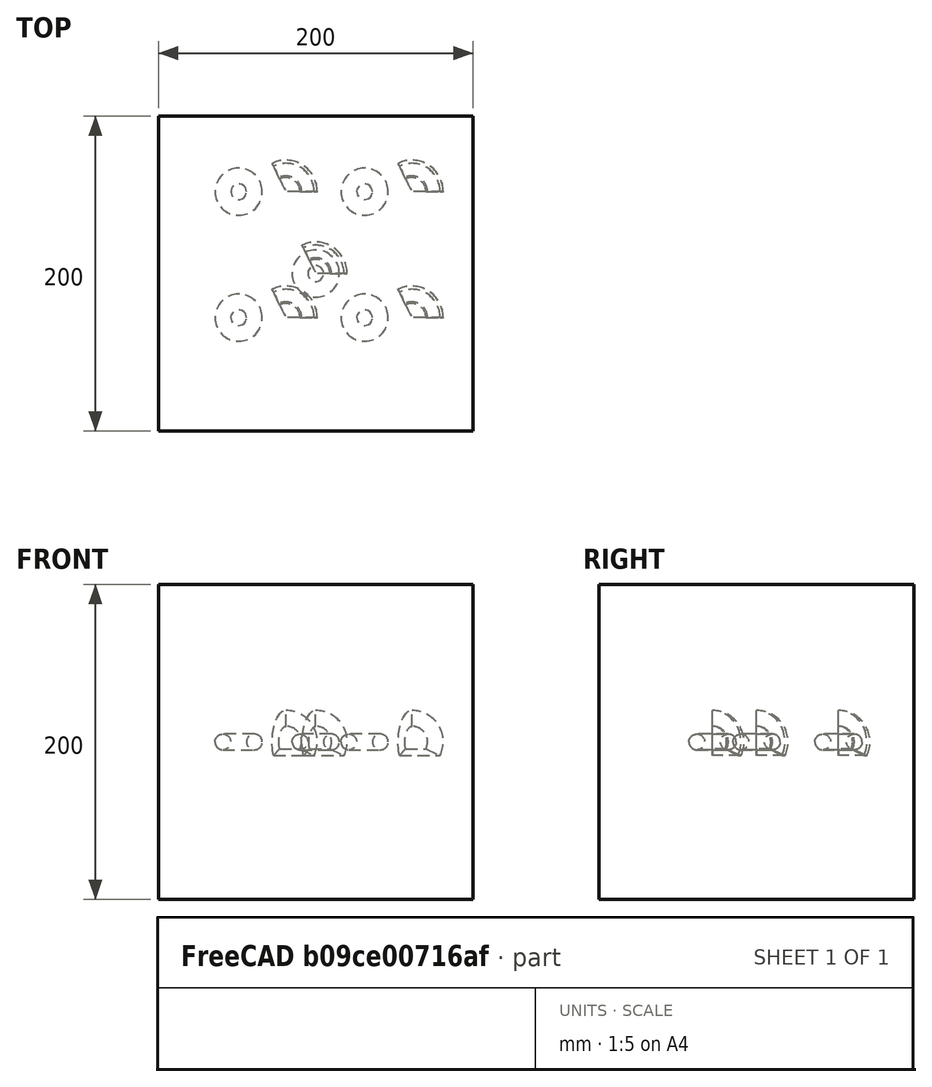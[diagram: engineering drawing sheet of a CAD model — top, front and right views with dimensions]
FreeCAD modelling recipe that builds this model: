
FCSTD DOCUMENT  (FreeCAD 1.0R39109 (Git))
Label: arrayTest-5
License: All rights reserved
LicenseURL: http://en.wikipedia.org/wiki/All_rights_reserved
objects: App::DocumentObjectGroupPython×1248, App::Part×5, Part::FeaturePython×4
note: 4 computed .brp shape members not serialized (recipe doc carries the construction recipe); baked Part::Feature solids carry a one-line shape summary decoded from their .brp

FEATURE [App::DocumentObjectGroupPython] HALFPI  # scripted group (container) (typed FeaturePython)
  name = HALFPI
  value = pi/2.
FEATURE [App::DocumentObjectGroupPython] PI  # scripted group (container) (typed FeaturePython)
  name = PI
  value = 1.*pi
FEATURE [App::DocumentObjectGroupPython] TWOPI  # scripted group (container) (typed FeaturePython)
  name = TWOPI
  value = 2.*pi
FEATURE [App::DocumentObjectGroupPython] Constants  # scripted group (container) (typed FeaturePython)
  Group = -> [HALFPI,PI,TWOPI]
FEATURE [App::DocumentObjectGroupPython] Variables  # scripted group (container) (typed FeaturePython)
FEATURE [App::DocumentObjectGroupPython] Quantities  # scripted group (container) (typed FeaturePython)
FEATURE [App::DocumentObjectGroupPython] Isotopes  # scripted group (container) (typed FeaturePython)
FEATURE [App::DocumentObjectGroupPython] Elements  # scripted group (container) (typed FeaturePython)
FEATURE [App::DocumentObjectGroupPython] G4Isotopes  # scripted group (container) (typed FeaturePython)
FEATURE [App::DocumentObjectGroupPython] H_element  # scripted group (container) (typed FeaturePython)
  Z = 1
  atom_value = 1.008
  formula = H
  name = H_element
FEATURE [App::DocumentObjectGroupPython] He_element  # scripted group (container) (typed FeaturePython)
  Z = 2
  atom_value = 4.0026
  formula = He
  name = He_element
FEATURE [App::DocumentObjectGroupPython] Li_element  # scripted group (container) (typed FeaturePython)
  Z = 3
  atom_value = 6.94
  formula = Li
  name = Li_element
FEATURE [App::DocumentObjectGroupPython] Be_element  # scripted group (container) (typed FeaturePython)
  Z = 4
  atom_value = 9.01218
  formula = Be
  name = Be_element
FEATURE [App::DocumentObjectGroupPython] B_element  # scripted group (container) (typed FeaturePython)
  Z = 5
  atom_value = 10.81
  formula = B
  name = B_element
FEATURE [App::DocumentObjectGroupPython] C_element  # scripted group (container) (typed FeaturePython)
  Z = 6
  atom_value = 12.011
  formula = C
  name = C_element
FEATURE [App::DocumentObjectGroupPython] N_element  # scripted group (container) (typed FeaturePython)
  Z = 7
  atom_value = 14.007
  formula = N
  name = N_element
FEATURE [App::DocumentObjectGroupPython] O_element  # scripted group (container) (typed FeaturePython)
  Z = 8
  atom_value = 15.999
  formula = O
  name = O_element
FEATURE [App::DocumentObjectGroupPython] F_element  # scripted group (container) (typed FeaturePython)
  Z = 9
  atom_value = 18.9984
  formula = F
  name = F_element
FEATURE [App::DocumentObjectGroupPython] Ne_element  # scripted group (container) (typed FeaturePython)
  Z = 10
  atom_value = 20.1797
  formula = Ne
  name = Ne_element
FEATURE [App::DocumentObjectGroupPython] Na_element  # scripted group (container) (typed FeaturePython)
  Z = 11
  atom_value = 22.9898
  formula = Na
  name = Na_element
FEATURE [App::DocumentObjectGroupPython] Mg_element  # scripted group (container) (typed FeaturePython)
  Z = 12
  atom_value = 24.305
  formula = Mg
  name = Mg_element
FEATURE [App::DocumentObjectGroupPython] Al_element  # scripted group (container) (typed FeaturePython)
  Z = 13
  atom_value = 26.9815
  formula = Al
  name = Al_element
FEATURE [App::DocumentObjectGroupPython] Si_element  # scripted group (container) (typed FeaturePython)
  Z = 14
  atom_value = 28.085
  formula = Si
  name = Si_element
FEATURE [App::DocumentObjectGroupPython] P_element  # scripted group (container) (typed FeaturePython)
  Z = 15
  atom_value = 30.9738
  formula = P
  name = P_element
FEATURE [App::DocumentObjectGroupPython] S_element  # scripted group (container) (typed FeaturePython)
  Z = 16
  atom_value = 32.06
  formula = S
  name = S_element
FEATURE [App::DocumentObjectGroupPython] Cl_element  # scripted group (container) (typed FeaturePython)
  Z = 17
  atom_value = 35.45
  formula = Cl
  name = Cl_element
FEATURE [App::DocumentObjectGroupPython] Ar_element  # scripted group (container) (typed FeaturePython)
  Z = 18
  atom_value = 39.95
  formula = Ar
  name = Ar_element
FEATURE [App::DocumentObjectGroupPython] K_element  # scripted group (container) (typed FeaturePython)
  Z = 19
  atom_value = 39.0983
  formula = K
  name = K_element
FEATURE [App::DocumentObjectGroupPython] Ca_element  # scripted group (container) (typed FeaturePython)
  Z = 20
  atom_value = 40.078
  formula = Ca
  name = Ca_element
FEATURE [App::DocumentObjectGroupPython] Sc_element  # scripted group (container) (typed FeaturePython)
  Z = 21
  atom_value = 44.9559
  formula = Sc
  name = Sc_element
FEATURE [App::DocumentObjectGroupPython] Ti_element  # scripted group (container) (typed FeaturePython)
  Z = 22
  atom_value = 47.867
  formula = Ti
  name = Ti_element
FEATURE [App::DocumentObjectGroupPython] V_element  # scripted group (container) (typed FeaturePython)
  Z = 23
  atom_value = 50.9415
  formula = V
  name = V_element
FEATURE [App::DocumentObjectGroupPython] Cr_element  # scripted group (container) (typed FeaturePython)
  Z = 24
  atom_value = 51.9961
  formula = Cr
  name = Cr_element
FEATURE [App::DocumentObjectGroupPython] Mn_element  # scripted group (container) (typed FeaturePython)
  Z = 25
  atom_value = 54.938
  formula = Mn
  name = Mn_element
FEATURE [App::DocumentObjectGroupPython] Fe_element  # scripted group (container) (typed FeaturePython)
  Z = 26
  atom_value = 55.845
  formula = Fe
  name = Fe_element
FEATURE [App::DocumentObjectGroupPython] Co_element  # scripted group (container) (typed FeaturePython)
  Z = 27
  atom_value = 58.9332
  formula = Co
  name = Co_element
FEATURE [App::DocumentObjectGroupPython] Ni_element  # scripted group (container) (typed FeaturePython)
  Z = 28
  atom_value = 58.6934
  formula = Ni
  name = Ni_element
FEATURE [App::DocumentObjectGroupPython] Cu_element  # scripted group (container) (typed FeaturePython)
  Z = 29
  atom_value = 63.546
  formula = Cu
  name = Cu_element
FEATURE [App::DocumentObjectGroupPython] Zn_element  # scripted group (container) (typed FeaturePython)
  Z = 30
  atom_value = 65.38
  formula = Zn
  name = Zn_element
FEATURE [App::DocumentObjectGroupPython] Ga_element  # scripted group (container) (typed FeaturePython)
  Z = 31
  atom_value = 69.723
  formula = Ga
  name = Ga_element
FEATURE [App::DocumentObjectGroupPython] Ge_element  # scripted group (container) (typed FeaturePython)
  Z = 32
  atom_value = 72.63
  formula = Ge
  name = Ge_element
FEATURE [App::DocumentObjectGroupPython] As_element  # scripted group (container) (typed FeaturePython)
  Z = 33
  atom_value = 74.9216
  formula = As
  name = As_element
FEATURE [App::DocumentObjectGroupPython] Se_element  # scripted group (container) (typed FeaturePython)
  Z = 34
  atom_value = 78.971
  formula = Se
  name = Se_element
FEATURE [App::DocumentObjectGroupPython] Br_element  # scripted group (container) (typed FeaturePython)
  Z = 35
  atom_value = 79.904
  formula = Br
  name = Br_element
FEATURE [App::DocumentObjectGroupPython] Kr_element  # scripted group (container) (typed FeaturePython)
  Z = 36
  atom_value = 83.798
  formula = Kr
  name = Kr_element
FEATURE [App::DocumentObjectGroupPython] Rb_element  # scripted group (container) (typed FeaturePython)
  Z = 37
  atom_value = 85.4678
  formula = Rb
  name = Rb_element
FEATURE [App::DocumentObjectGroupPython] Sr_element  # scripted group (container) (typed FeaturePython)
  Z = 38
  atom_value = 87.62
  formula = Sr
  name = Sr_element
FEATURE [App::DocumentObjectGroupPython] Y_element  # scripted group (container) (typed FeaturePython)
  Z = 39
  atom_value = 88.9058
  formula = Y
  name = Y_element
FEATURE [App::DocumentObjectGroupPython] Zr_element  # scripted group (container) (typed FeaturePython)
  Z = 40
  atom_value = 91.224
  formula = Zr
  name = Zr_element
FEATURE [App::DocumentObjectGroupPython] Nb_element  # scripted group (container) (typed FeaturePython)
  Z = 41
  atom_value = 92.9064
  formula = Nb
  name = Nb_element
FEATURE [App::DocumentObjectGroupPython] Mo_element  # scripted group (container) (typed FeaturePython)
  Z = 42
  atom_value = 95.95
  formula = Mo
  name = Mo_element
FEATURE [App::DocumentObjectGroupPython] Tc_element  # scripted group (container) (typed FeaturePython)
  Z = 43
  atom_value = 97
  formula = Tc
  name = Tc_element
FEATURE [App::DocumentObjectGroupPython] Ru_element  # scripted group (container) (typed FeaturePython)
  Z = 44
  atom_value = 101.07
  formula = Ru
  name = Ru_element
FEATURE [App::DocumentObjectGroupPython] Rh_element  # scripted group (container) (typed FeaturePython)
  Z = 45
  atom_value = 102.905
  formula = Rh
  name = Rh_element
FEATURE [App::DocumentObjectGroupPython] Pd_element  # scripted group (container) (typed FeaturePython)
  Z = 46
  atom_value = 106.42
  formula = Pd
  name = Pd_element
FEATURE [App::DocumentObjectGroupPython] Ag_element  # scripted group (container) (typed FeaturePython)
  Z = 47
  atom_value = 107.868
  formula = Ag
  name = Ag_element
FEATURE [App::DocumentObjectGroupPython] Cd_element  # scripted group (container) (typed FeaturePython)
  Z = 48
  atom_value = 112.414
  formula = Cd
  name = Cd_element
FEATURE [App::DocumentObjectGroupPython] In_element  # scripted group (container) (typed FeaturePython)
  Z = 49
  atom_value = 114.818
  formula = In
  name = In_element
FEATURE [App::DocumentObjectGroupPython] Sn_element  # scripted group (container) (typed FeaturePython)
  Z = 50
  atom_value = 118.71
  formula = Sn
  name = Sn_element
FEATURE [App::DocumentObjectGroupPython] Sb_element  # scripted group (container) (typed FeaturePython)
  Z = 51
  atom_value = 121.76
  formula = Sb
  name = Sb_element
FEATURE [App::DocumentObjectGroupPython] Te_element  # scripted group (container) (typed FeaturePython)
  Z = 52
  atom_value = 127.6
  formula = Te
  name = Te_element
FEATURE [App::DocumentObjectGroupPython] I_element  # scripted group (container) (typed FeaturePython)
  Z = 53
  atom_value = 126.904
  formula = I
  name = I_element
FEATURE [App::DocumentObjectGroupPython] Xe_element  # scripted group (container) (typed FeaturePython)
  Z = 54
  atom_value = 131.293
  formula = Xe
  name = Xe_element
FEATURE [App::DocumentObjectGroupPython] Cs_element  # scripted group (container) (typed FeaturePython)
  Z = 55
  atom_value = 132.905
  formula = Cs
  name = Cs_element
FEATURE [App::DocumentObjectGroupPython] Ba_element  # scripted group (container) (typed FeaturePython)
  Z = 56
  atom_value = 137.327
  formula = Ba
  name = Ba_element
FEATURE [App::DocumentObjectGroupPython] La_element  # scripted group (container) (typed FeaturePython)
  Z = 57
  atom_value = 138.905
  formula = La
  name = La_element
FEATURE [App::DocumentObjectGroupPython] Ce_element  # scripted group (container) (typed FeaturePython)
  Z = 58
  atom_value = 140.116
  formula = Ce
  name = Ce_element
FEATURE [App::DocumentObjectGroupPython] Pr_element  # scripted group (container) (typed FeaturePython)
  Z = 59
  atom_value = 140.908
  formula = Pr
  name = Pr_element
FEATURE [App::DocumentObjectGroupPython] Nd_element  # scripted group (container) (typed FeaturePython)
  Z = 60
  atom_value = 144.242
  formula = Nd
  name = Nd_element
FEATURE [App::DocumentObjectGroupPython] Pm_element  # scripted group (container) (typed FeaturePython)
  Z = 61
  atom_value = 145
  formula = Pm
  name = Pm_element
FEATURE [App::DocumentObjectGroupPython] Sm_element  # scripted group (container) (typed FeaturePython)
  Z = 62
  atom_value = 150.36
  formula = Sm
  name = Sm_element
FEATURE [App::DocumentObjectGroupPython] Eu_element  # scripted group (container) (typed FeaturePython)
  Z = 63
  atom_value = 151.964
  formula = Eu
  name = Eu_element
FEATURE [App::DocumentObjectGroupPython] Gd_element  # scripted group (container) (typed FeaturePython)
  Z = 64
  atom_value = 157.25
  formula = Gd
  name = Gd_element
FEATURE [App::DocumentObjectGroupPython] Tb_element  # scripted group (container) (typed FeaturePython)
  Z = 65
  atom_value = 158.925
  formula = Tb
  name = Tb_element
FEATURE [App::DocumentObjectGroupPython] Dy_element  # scripted group (container) (typed FeaturePython)
  Z = 66
  atom_value = 162.5
  formula = Dy
  name = Dy_element
FEATURE [App::DocumentObjectGroupPython] Ho_element  # scripted group (container) (typed FeaturePython)
  Z = 67
  atom_value = 164.93
  formula = Ho
  name = Ho_element
FEATURE [App::DocumentObjectGroupPython] Er_element  # scripted group (container) (typed FeaturePython)
  Z = 68
  atom_value = 167.259
  formula = Er
  name = Er_element
FEATURE [App::DocumentObjectGroupPython] Tm_element  # scripted group (container) (typed FeaturePython)
  Z = 69
  atom_value = 168.934
  formula = Tm
  name = Tm_element
FEATURE [App::DocumentObjectGroupPython] Yb_element  # scripted group (container) (typed FeaturePython)
  Z = 70
  atom_value = 173.045
  formula = Yb
  name = Yb_element
FEATURE [App::DocumentObjectGroupPython] Lu_element  # scripted group (container) (typed FeaturePython)
  Z = 71
  atom_value = 174.967
  formula = Lu
  name = Lu_element
FEATURE [App::DocumentObjectGroupPython] Hf_element  # scripted group (container) (typed FeaturePython)
  Z = 72
  atom_value = 178.49
  formula = Hf
  name = Hf_element
FEATURE [App::DocumentObjectGroupPython] Ta_element  # scripted group (container) (typed FeaturePython)
  Z = 73
  atom_value = 180.948
  formula = Ta
  name = Ta_element
FEATURE [App::DocumentObjectGroupPython] W_element  # scripted group (container) (typed FeaturePython)
  Z = 74
  atom_value = 183.84
  formula = W
  name = W_element
FEATURE [App::DocumentObjectGroupPython] Re_element  # scripted group (container) (typed FeaturePython)
  Z = 75
  atom_value = 186.207
  formula = Re
  name = Re_element
FEATURE [App::DocumentObjectGroupPython] Os_element  # scripted group (container) (typed FeaturePython)
  Z = 76
  atom_value = 190.23
  formula = Os
  name = Os_element
FEATURE [App::DocumentObjectGroupPython] Ir_element  # scripted group (container) (typed FeaturePython)
  Z = 77
  atom_value = 192.217
  formula = Ir
  name = Ir_element
FEATURE [App::DocumentObjectGroupPython] Pt_element  # scripted group (container) (typed FeaturePython)
  Z = 78
  atom_value = 195.084
  formula = Pt
  name = Pt_element
FEATURE [App::DocumentObjectGroupPython] Au_element  # scripted group (container) (typed FeaturePython)
  Z = 79
  atom_value = 196.967
  formula = Au
  name = Au_element
FEATURE [App::DocumentObjectGroupPython] Hg_element  # scripted group (container) (typed FeaturePython)
  Z = 80
  atom_value = 200.592
  formula = Hg
  name = Hg_element
FEATURE [App::DocumentObjectGroupPython] Tl_element  # scripted group (container) (typed FeaturePython)
  Z = 81
  atom_value = 204.38
  formula = Tl
  name = Tl_element
FEATURE [App::DocumentObjectGroupPython] Pb_element  # scripted group (container) (typed FeaturePython)
  Z = 82
  atom_value = 207.2
  formula = Pb
  name = Pb_element
FEATURE [App::DocumentObjectGroupPython] Bi_element  # scripted group (container) (typed FeaturePython)
  Z = 83
  atom_value = 208.98
  formula = Bi
  name = Bi_element
FEATURE [App::DocumentObjectGroupPython] Po_element  # scripted group (container) (typed FeaturePython)
  Z = 84
  atom_value = 209
  formula = Po
  name = Po_element
FEATURE [App::DocumentObjectGroupPython] At_element  # scripted group (container) (typed FeaturePython)
  Z = 85
  atom_value = 210
  formula = At
  name = At_element
FEATURE [App::DocumentObjectGroupPython] Rn_element  # scripted group (container) (typed FeaturePython)
  Z = 86
  atom_value = 222
  formula = Rn
  name = Rn_element
FEATURE [App::DocumentObjectGroupPython] Fr_element  # scripted group (container) (typed FeaturePython)
  Z = 87
  atom_value = 223
  formula = Fr
  name = Fr_element
FEATURE [App::DocumentObjectGroupPython] Ra_element  # scripted group (container) (typed FeaturePython)
  Z = 88
  atom_value = 226
  formula = Ra
  name = Ra_element
FEATURE [App::DocumentObjectGroupPython] Ac_element  # scripted group (container) (typed FeaturePython)
  Z = 89
  atom_value = 227
  formula = Ac
  name = Ac_element
FEATURE [App::DocumentObjectGroupPython] Th_element  # scripted group (container) (typed FeaturePython)
  Z = 90
  atom_value = 232.038
  formula = Th
  name = Th_element
FEATURE [App::DocumentObjectGroupPython] Pa_element  # scripted group (container) (typed FeaturePython)
  Z = 91
  atom_value = 231.036
  formula = Pa
  name = Pa_element
FEATURE [App::DocumentObjectGroupPython] U_element  # scripted group (container) (typed FeaturePython)
  Z = 92
  atom_value = 238.029
  formula = U
  name = U_element
FEATURE [App::DocumentObjectGroupPython] Np_element  # scripted group (container) (typed FeaturePython)
  Z = 93
  atom_value = 237
  formula = Np
  name = Np_element
FEATURE [App::DocumentObjectGroupPython] Pu_element  # scripted group (container) (typed FeaturePython)
  Z = 94
  atom_value = 244
  formula = Pu
  name = Pu_element
FEATURE [App::DocumentObjectGroupPython] Am_element  # scripted group (container) (typed FeaturePython)
  Z = 95
  atom_value = 243
  formula = Am
  name = Am_element
FEATURE [App::DocumentObjectGroupPython] Cm_element  # scripted group (container) (typed FeaturePython)
  Z = 96
  atom_value = 247
  formula = Cm
  name = Cm_element
FEATURE [App::DocumentObjectGroupPython] Bk_element  # scripted group (container) (typed FeaturePython)
  Z = 97
  atom_value = 247
  formula = Bk
  name = Bk_element
FEATURE [App::DocumentObjectGroupPython] Cf_element  # scripted group (container) (typed FeaturePython)
  Z = 98
  atom_value = 251
  formula = Cf
  name = Cf_element
FEATURE [App::DocumentObjectGroupPython] G4Elements  # scripted group (container) (typed FeaturePython)
  Group = -> [H_element,He_element,Li_element,Be_element,B_element,C_element,N_element,O_element,F_element,Ne_element,Na_element,Mg_element,Al_element,Si_element,P_element,S_element,Cl_element,Ar_element,K_element,Ca_element,Sc_element,Ti_element,V_element,Cr_element,Mn_element,Fe_element,Co_element,Ni_element,Cu_element,Zn_element,Ga_element,Ge_element,As_element,Se_element,Br_element,Kr_element,Rb_element,+61 more]
FEATURE [App::DocumentObjectGroupPython] H_element001  label="H_element : 0.101"  # scripted group (container) (typed FeaturePython)
  n = 0.101327
FEATURE [App::DocumentObjectGroupPython] C_element001  label="C_element : 0.775"  # scripted group (container) (typed FeaturePython)
  n = 0.7755
FEATURE [App::DocumentObjectGroupPython] N_element001  label="N_element : 0.035"  # scripted group (container) (typed FeaturePython)
  n = 0.035057
FEATURE [App::DocumentObjectGroupPython] O_element001  label="O_element : 0.052"  # scripted group (container) (typed FeaturePython)
  n = 0.0523159
FEATURE [App::DocumentObjectGroupPython] F_element001  label="F_element : 0.017"  # scripted group (container) (typed FeaturePython)
  n = 0.017422
FEATURE [App::DocumentObjectGroupPython] Ca_element001  label="Ca_element : 0.018"  # scripted group (container) (typed FeaturePython)
  n = 0.018378
FEATURE [App::DocumentObjectGroupPython] G4_A_150_TISSUE  label="G4_A-150_TISSUE"  # scripted group (container) (typed FeaturePython)
  Dunit = g/cm3
  Dvalue = 1.127
  Group = -> [H_element001,C_element001,N_element001,O_element001,F_element001,Ca_element001]
  conduct = 2
  density = 1
  expand = 3
  formula = G4_A-150_TISSUE
  name = G4_A-150_TISSUE
  specific = 4
FEATURE [App::DocumentObjectGroupPython] C_element002  label="C_element : 3"  # scripted group (container) (typed FeaturePython)
  n = 3
  ref = C_element
FEATURE [App::DocumentObjectGroupPython] H_element002  label="H_element : 6"  # scripted group (container) (typed FeaturePython)
  n = 6
  ref = H_element
FEATURE [App::DocumentObjectGroupPython] O_element002  label="O_element : 1"  # scripted group (container) (typed FeaturePython)
  n = 1
  ref = O_element
FEATURE [App::DocumentObjectGroupPython] G4_ACETONE  # scripted group (container) (typed FeaturePython)
  Dunit = g/cm3
  Dvalue = 0.7899
  Group = -> [C_element002,H_element002,O_element002]
  conduct = 2
  density = 1
  expand = 3
  formula = G4_ACETONE
  name = G4_ACETONE
  specific = 4
FEATURE [App::DocumentObjectGroupPython] C_element003  label="C_element : 2"  # scripted group (container) (typed FeaturePython)
  n = 2
  ref = C_element
FEATURE [App::DocumentObjectGroupPython] H_element003  label="H_element : 2"  # scripted group (container) (typed FeaturePython)
  n = 2
  ref = H_element
FEATURE [App::DocumentObjectGroupPython] G4_ACETYLENE  # scripted group (container) (typed FeaturePython)
  Dunit = g/cm3
  Dvalue = 0.0010967
  Group = -> [C_element003,H_element003]
  conduct = 2
  density = 1
  expand = 3
  formula = G4_ACETYLENE
  name = G4_ACETYLENE
  specific = 4
FEATURE [App::DocumentObjectGroupPython] C_element004  label="C_element : 5"  # scripted group (container) (typed FeaturePython)
  n = 5
  ref = C_element
FEATURE [App::DocumentObjectGroupPython] H_element004  label="H_element : 5"  # scripted group (container) (typed FeaturePython)
  n = 5
  ref = H_element
FEATURE [App::DocumentObjectGroupPython] N_element002  label="N_element : 5"  # scripted group (container) (typed FeaturePython)
  n = 5
  ref = N_element
FEATURE [App::DocumentObjectGroupPython] G4_ADENINE  # scripted group (container) (typed FeaturePython)
  Dunit = g/cm3
  Dvalue = 1.6
  Group = -> [C_element004,H_element004,N_element002]
  conduct = 2
  density = 1
  expand = 3
  formula = G4_ADENINE
  name = G4_ADENINE
  specific = 4
FEATURE [App::DocumentObjectGroupPython] H_element005  label="H_element : 0.114"  # scripted group (container) (typed FeaturePython)
  n = 0.114
FEATURE [App::DocumentObjectGroupPython] C_element005  label="C_element : 0.598"  # scripted group (container) (typed FeaturePython)
  n = 0.598
FEATURE [App::DocumentObjectGroupPython] N_element003  label="N_element : 0.007"  # scripted group (container) (typed FeaturePython)
  n = 0.007
FEATURE [App::DocumentObjectGroupPython] O_element003  label="O_element : 0.278"  # scripted group (container) (typed FeaturePython)
  n = 0.278
FEATURE [App::DocumentObjectGroupPython] Na_element001  label="Na_element : 0.001"  # scripted group (container) (typed FeaturePython)
  n = 0.001
FEATURE [App::DocumentObjectGroupPython] S_element001  label="S_element : 0.001"  # scripted group (container) (typed FeaturePython)
  n = 0.001
FEATURE [App::DocumentObjectGroupPython] Cl_element001  label="Cl_element : 0.001"  # scripted group (container) (typed FeaturePython)
  n = 0.001
FEATURE [App::DocumentObjectGroupPython] G4_ADIPOSE_TISSUE_ICRP  # scripted group (container) (typed FeaturePython)
  Dunit = g/cm3
  Dvalue = 0.95
  Group = -> [H_element005,C_element005,N_element003,O_element003,Na_element001,S_element001,Cl_element001]
  conduct = 2
  density = 1
  expand = 3
  formula = G4_ADIPOSE_TISSUE_ICRP
  name = G4_ADIPOSE_TISSUE_ICRP
  specific = 4
FEATURE [App::DocumentObjectGroupPython] C_element006  label="C_element : 0.000"  # scripted group (container) (typed FeaturePython)
  n = 0.000124
FEATURE [App::DocumentObjectGroupPython] N_element004  label="N_element : 0.755"  # scripted group (container) (typed FeaturePython)
  n = 0.755268
FEATURE [App::DocumentObjectGroupPython] O_element004  label="O_element : 0.232"  # scripted group (container) (typed FeaturePython)
  n = 0.231781
FEATURE [App::DocumentObjectGroupPython] Ar_element001  label="Ar_element : 0.013"  # scripted group (container) (typed FeaturePython)
  n = 0.012827
FEATURE [App::DocumentObjectGroupPython] G4_AIR  # scripted group (container) (typed FeaturePython)
  Dunit = g/cm3
  Dvalue = 0.00120479
  Group = -> [C_element006,N_element004,O_element004,Ar_element001]
  conduct = 2
  density = 1
  expand = 3
  formula = G4_AIR
  name = G4_AIR
  specific = 4
FEATURE [App::DocumentObjectGroupPython] C_element007  label="C_element : 006"  # scripted group (container) (typed FeaturePython)
  n = 3
  ref = C_element
FEATURE [App::DocumentObjectGroupPython] H_element006  label="H_element : 7"  # scripted group (container) (typed FeaturePython)
  n = 7
  ref = H_element
FEATURE [App::DocumentObjectGroupPython] N_element005  label="N_element : 1"  # scripted group (container) (typed FeaturePython)
  n = 1
  ref = N_element
FEATURE [App::DocumentObjectGroupPython] O_element005  label="O_element : 2"  # scripted group (container) (typed FeaturePython)
  n = 2
  ref = O_element
FEATURE [App::DocumentObjectGroupPython] G4_ALANINE  # scripted group (container) (typed FeaturePython)
  Dunit = g/cm3
  Dvalue = 1.42
  Group = -> [C_element007,H_element006,N_element005,O_element005]
  conduct = 2
  density = 1
  expand = 3
  formula = G4_ALANINE
  name = G4_ALANINE
  specific = 4
FEATURE [App::DocumentObjectGroupPython] Al_element001  label="Al_element : 2"  # scripted group (container) (typed FeaturePython)
  n = 2
  ref = Al_element
FEATURE [App::DocumentObjectGroupPython] O_element006  label="O_element : 3"  # scripted group (container) (typed FeaturePython)
  n = 3
  ref = O_element
FEATURE [App::DocumentObjectGroupPython] G4_ALUMINUM_OXIDE  # scripted group (container) (typed FeaturePython)
  Dunit = g/cm3
  Dvalue = 3.97
  Group = -> [Al_element001,O_element006]
  conduct = 2
  density = 1
  expand = 3
  formula = G4_ALUMINUM_OXIDE
  name = G4_ALUMINUM_OXIDE
  specific = 4
FEATURE [App::DocumentObjectGroupPython] H_element007  label="H_element : 0.106"  # scripted group (container) (typed FeaturePython)
  n = 0.10593
FEATURE [App::DocumentObjectGroupPython] C_element008  label="C_element : 0.789"  # scripted group (container) (typed FeaturePython)
  n = 0.788974
FEATURE [App::DocumentObjectGroupPython] O_element007  label="O_element : 0.105"  # scripted group (container) (typed FeaturePython)
  n = 0.105096
FEATURE [App::DocumentObjectGroupPython] G4_AMBER  # scripted group (container) (typed FeaturePython)
  Dunit = g/cm3
  Dvalue = 1.1
  Group = -> [H_element007,C_element008,O_element007]
  conduct = 2
  density = 1
  expand = 3
  formula = G4_AMBER
  name = G4_AMBER
  specific = 4
FEATURE [App::DocumentObjectGroupPython] N_element006  label="N_element : 006"  # scripted group (container) (typed FeaturePython)
  n = 1
  ref = N_element
FEATURE [App::DocumentObjectGroupPython] H_element008  label="H_element : 3"  # scripted group (container) (typed FeaturePython)
  n = 3
  ref = H_element
FEATURE [App::DocumentObjectGroupPython] G4_AMMONIA  # scripted group (container) (typed FeaturePython)
  Dunit = g/cm3
  Dvalue = 0.000826019
  Group = -> [N_element006,H_element008]
  conduct = 2
  density = 1
  expand = 3
  formula = G4_AMMONIA
  name = G4_AMMONIA
  specific = 4
FEATURE [App::DocumentObjectGroupPython] C_element009  label="C_element : 6"  # scripted group (container) (typed FeaturePython)
  n = 6
  ref = C_element
FEATURE [App::DocumentObjectGroupPython] H_element009  label="H_element : 008"  # scripted group (container) (typed FeaturePython)
  n = 7
  ref = H_element
FEATURE [App::DocumentObjectGroupPython] N_element007  label="N_element : 007"  # scripted group (container) (typed FeaturePython)
  n = 1
  ref = N_element
FEATURE [App::DocumentObjectGroupPython] G4_ANILINE  # scripted group (container) (typed FeaturePython)
  Dunit = g/cm3
  Dvalue = 1.0235
  Group = -> [C_element009,H_element009,N_element007]
  conduct = 2
  density = 1
  expand = 3
  formula = G4_ANILINE
  name = G4_ANILINE
  specific = 4
FEATURE [App::DocumentObjectGroupPython] C_element010  label="C_element : 14"  # scripted group (container) (typed FeaturePython)
  n = 14
  ref = C_element
FEATURE [App::DocumentObjectGroupPython] H_element010  label="H_element : 10"  # scripted group (container) (typed FeaturePython)
  n = 10
  ref = H_element
FEATURE [App::DocumentObjectGroupPython] G4_ANTHRACENE  # scripted group (container) (typed FeaturePython)
  Dunit = g/cm3
  Dvalue = 1.283
  Group = -> [C_element010,H_element010]
  conduct = 2
  density = 1
  expand = 3
  formula = G4_ANTHRACENE
  name = G4_ANTHRACENE
  specific = 4
FEATURE [App::DocumentObjectGroupPython] H_element011  label="H_element : 0.065"  # scripted group (container) (typed FeaturePython)
  n = 0.0654709
FEATURE [App::DocumentObjectGroupPython] C_element011  label="C_element : 0.537"  # scripted group (container) (typed FeaturePython)
  n = 0.536944
FEATURE [App::DocumentObjectGroupPython] N_element008  label="N_element : 0.021"  # scripted group (container) (typed FeaturePython)
  n = 0.0215
FEATURE [App::DocumentObjectGroupPython] O_element008  label="O_element : 0.032"  # scripted group (container) (typed FeaturePython)
  n = 0.032085
FEATURE [App::DocumentObjectGroupPython] F_element002  label="F_element : 0.167"  # scripted group (container) (typed FeaturePython)
  n = 0.167411
FEATURE [App::DocumentObjectGroupPython] Ca_element002  label="Ca_element : 0.177"  # scripted group (container) (typed FeaturePython)
  n = 0.176589
FEATURE [App::DocumentObjectGroupPython] G4_B_100_BONE  label="G4_B-100_BONE"  # scripted group (container) (typed FeaturePython)
  Dunit = g/cm3
  Dvalue = 1.45
  Group = -> [H_element011,C_element011,N_element008,O_element008,F_element002,Ca_element002]
  conduct = 2
  density = 1
  expand = 3
  formula = G4_B-100_BONE
  name = G4_B-100_BONE
  specific = 4
FEATURE [App::DocumentObjectGroupPython] H_element012  label="H_element : 0.057"  # scripted group (container) (typed FeaturePython)
  n = 0.057441
FEATURE [App::DocumentObjectGroupPython] C_element012  label="C_element : 0.790"  # scripted group (container) (typed FeaturePython)
  n = 0.774591
FEATURE [App::DocumentObjectGroupPython] O_element009  label="O_element : 0.168"  # scripted group (container) (typed FeaturePython)
  n = 0.167968
FEATURE [App::DocumentObjectGroupPython] G4_BAKELITE  # scripted group (container) (typed FeaturePython)
  Dunit = g/cm3
  Dvalue = 1.25
  Group = -> [H_element012,C_element012,O_element009]
  conduct = 2
  density = 1
  expand = 3
  formula = G4_BAKELITE
  name = G4_BAKELITE
  specific = 4
FEATURE [App::DocumentObjectGroupPython] Ba_element001  label="Ba_element : 1"  # scripted group (container) (typed FeaturePython)
  n = 1
  ref = Ba_element
FEATURE [App::DocumentObjectGroupPython] F_element003  label="F_element : 2"  # scripted group (container) (typed FeaturePython)
  n = 2
  ref = F_element
FEATURE [App::DocumentObjectGroupPython] G4_BARIUM_FLUORIDE  # scripted group (container) (typed FeaturePython)
  Dunit = g/cm3
  Dvalue = 4.89
  Group = -> [Ba_element001,F_element003]
  conduct = 2
  density = 1
  expand = 3
  formula = G4_BARIUM_FLUORIDE
  name = G4_BARIUM_FLUORIDE
  specific = 4
FEATURE [App::DocumentObjectGroupPython] Ba_element002  label="Ba_element : 002"  # scripted group (container) (typed FeaturePython)
  n = 1
  ref = Ba_element
FEATURE [App::DocumentObjectGroupPython] S_element002  label="S_element : 1"  # scripted group (container) (typed FeaturePython)
  n = 1
  ref = S_element
FEATURE [App::DocumentObjectGroupPython] O_element010  label="O_element : 4"  # scripted group (container) (typed FeaturePython)
  n = 4
  ref = O_element
FEATURE [App::DocumentObjectGroupPython] G4_BARIUM_SULFATE  # scripted group (container) (typed FeaturePython)
  Dunit = g/cm3
  Dvalue = 4.5
  Group = -> [Ba_element002,S_element002,O_element010]
  conduct = 2
  density = 1
  expand = 3
  formula = G4_BARIUM_SULFATE
  name = G4_BARIUM_SULFATE
  specific = 4
FEATURE [App::DocumentObjectGroupPython] C_element013  label="C_element : 007"  # scripted group (container) (typed FeaturePython)
  n = 6
  ref = C_element
FEATURE [App::DocumentObjectGroupPython] H_element013  label="H_element : 009"  # scripted group (container) (typed FeaturePython)
  n = 6
  ref = H_element
FEATURE [App::DocumentObjectGroupPython] G4_BENZENE  # scripted group (container) (typed FeaturePython)
  Dunit = g/cm3
  Dvalue = 0.87865
  Group = -> [C_element013,H_element013]
  conduct = 2
  density = 1
  expand = 3
  formula = G4_BENZENE
  name = G4_BENZENE
  specific = 4
FEATURE [App::DocumentObjectGroupPython] Be_element001  label="Be_element : 1"  # scripted group (container) (typed FeaturePython)
  n = 1
  ref = Be_element
FEATURE [App::DocumentObjectGroupPython] O_element011  label="O_element : 005"  # scripted group (container) (typed FeaturePython)
  n = 1
  ref = O_element
FEATURE [App::DocumentObjectGroupPython] G4_BERYLLIUM_OXIDE  # scripted group (container) (typed FeaturePython)
  Dunit = g/cm3
  Dvalue = 3.01
  Group = -> [Be_element001,O_element011]
  conduct = 2
  density = 1
  expand = 3
  formula = G4_BERYLLIUM_OXIDE
  name = G4_BERYLLIUM_OXIDE
  specific = 4
FEATURE [App::DocumentObjectGroupPython] Bi_element001  label="Bi_element : 4"  # scripted group (container) (typed FeaturePython)
  n = 4
  ref = Bi_element
FEATURE [App::DocumentObjectGroupPython] Ge_element001  label="Ge_element : 3"  # scripted group (container) (typed FeaturePython)
  n = 3
  ref = Ge_element
FEATURE [App::DocumentObjectGroupPython] O_element012  label="O_element : 12"  # scripted group (container) (typed FeaturePython)
  n = 12
  ref = O_element
FEATURE [App::DocumentObjectGroupPython] G4_BGO  # scripted group (container) (typed FeaturePython)
  Dunit = g/cm3
  Dvalue = 7.13
  Group = -> [Bi_element001,Ge_element001,O_element012]
  conduct = 2
  density = 1
  expand = 3
  formula = G4_BGO
  name = G4_BGO
  specific = 4
FEATURE [App::DocumentObjectGroupPython] H_element014  label="H_element : 0.102"  # scripted group (container) (typed FeaturePython)
  n = 0.102
FEATURE [App::DocumentObjectGroupPython] C_element014  label="C_element : 0.110"  # scripted group (container) (typed FeaturePython)
  n = 0.11
FEATURE [App::DocumentObjectGroupPython] N_element009  label="N_element : 0.033"  # scripted group (container) (typed FeaturePython)
  n = 0.033
FEATURE [App::DocumentObjectGroupPython] O_element013  label="O_element : 0.745"  # scripted group (container) (typed FeaturePython)
  n = 0.745
FEATURE [App::DocumentObjectGroupPython] Na_element002  label="Na_element : 0.002"  # scripted group (container) (typed FeaturePython)
  n = 0.001
FEATURE [App::DocumentObjectGroupPython] P_element001  label="P_element : 0.001"  # scripted group (container) (typed FeaturePython)
  n = 0.001
FEATURE [App::DocumentObjectGroupPython] S_element003  label="S_element : 0.002"  # scripted group (container) (typed FeaturePython)
  n = 0.002
FEATURE [App::DocumentObjectGroupPython] Cl_element002  label="Cl_element : 0.003"  # scripted group (container) (typed FeaturePython)
  n = 0.003
FEATURE [App::DocumentObjectGroupPython] K_element001  label="K_element : 0.002"  # scripted group (container) (typed FeaturePython)
  n = 0.002
FEATURE [App::DocumentObjectGroupPython] Fe_element001  label="Fe_element : 0.001"  # scripted group (container) (typed FeaturePython)
  n = 0.001
FEATURE [App::DocumentObjectGroupPython] G4_BLOOD_ICRP  # scripted group (container) (typed FeaturePython)
  Dunit = g/cm3
  Dvalue = 1.06
  Group = -> [H_element014,C_element014,N_element009,O_element013,Na_element002,P_element001,S_element003,Cl_element002,K_element001,Fe_element001]
  conduct = 2
  density = 1
  expand = 3
  formula = G4_BLOOD_ICRP
  name = G4_BLOOD_ICRP
  specific = 4
FEATURE [App::DocumentObjectGroupPython] H_element015  label="H_element : 0.064"  # scripted group (container) (typed FeaturePython)
  n = 0.064
FEATURE [App::DocumentObjectGroupPython] C_element015  label="C_element : 0.278"  # scripted group (container) (typed FeaturePython)
  n = 0.278
FEATURE [App::DocumentObjectGroupPython] N_element010  label="N_element : 0.027"  # scripted group (container) (typed FeaturePython)
  n = 0.027
FEATURE [App::DocumentObjectGroupPython] O_element014  label="O_element : 0.410"  # scripted group (container) (typed FeaturePython)
  n = 0.41
FEATURE [App::DocumentObjectGroupPython] Mg_element001  label="Mg_element : 0.002"  # scripted group (container) (typed FeaturePython)
  n = 0.002
FEATURE [App::DocumentObjectGroupPython] P_element002  label="P_element : 0.070"  # scripted group (container) (typed FeaturePython)
  n = 0.07
FEATURE [App::DocumentObjectGroupPython] S_element004  label="S_element : 0.003"  # scripted group (container) (typed FeaturePython)
  n = 0.002
FEATURE [App::DocumentObjectGroupPython] Ca_element003  label="Ca_element : 0.147"  # scripted group (container) (typed FeaturePython)
  n = 0.147
FEATURE [App::DocumentObjectGroupPython] G4_BONE_COMPACT_ICRU  # scripted group (container) (typed FeaturePython)
  Dunit = g/cm3
  Dvalue = 1.85
  Group = -> [H_element015,C_element015,N_element010,O_element014,Mg_element001,P_element002,S_element004,Ca_element003]
  conduct = 2
  density = 1
  expand = 3
  formula = G4_BONE_COMPACT_ICRU
  name = G4_BONE_COMPACT_ICRU
  specific = 4
FEATURE [App::DocumentObjectGroupPython] H_element016  label="H_element : 0.034"  # scripted group (container) (typed FeaturePython)
  n = 0.034
FEATURE [App::DocumentObjectGroupPython] C_element016  label="C_element : 0.155"  # scripted group (container) (typed FeaturePython)
  n = 0.155
FEATURE [App::DocumentObjectGroupPython] N_element011  label="N_element : 0.042"  # scripted group (container) (typed FeaturePython)
  n = 0.042
FEATURE [App::DocumentObjectGroupPython] O_element015  label="O_element : 0.435"  # scripted group (container) (typed FeaturePython)
  n = 0.435
FEATURE [App::DocumentObjectGroupPython] Na_element003  label="Na_element : 0.003"  # scripted group (container) (typed FeaturePython)
  n = 0.001
FEATURE [App::DocumentObjectGroupPython] Mg_element002  label="Mg_element : 0.003"  # scripted group (container) (typed FeaturePython)
  n = 0.002
FEATURE [App::DocumentObjectGroupPython] P_element003  label="P_element : 0.103"  # scripted group (container) (typed FeaturePython)
  n = 0.103
FEATURE [App::DocumentObjectGroupPython] S_element005  label="S_element : 0.004"  # scripted group (container) (typed FeaturePython)
  n = 0.003
FEATURE [App::DocumentObjectGroupPython] Ca_element004  label="Ca_element : 0.225"  # scripted group (container) (typed FeaturePython)
  n = 0.225
FEATURE [App::DocumentObjectGroupPython] G4_BONE_CORTICAL_ICRP  # scripted group (container) (typed FeaturePython)
  Dunit = g/cm3
  Dvalue = 1.92
  Group = -> [H_element016,C_element016,N_element011,O_element015,Na_element003,Mg_element002,P_element003,S_element005,Ca_element004]
  conduct = 2
  density = 1
  expand = 3
  formula = G4_BONE_CORTICAL_ICRP
  name = G4_BONE_CORTICAL_ICRP
  specific = 4
FEATURE [App::DocumentObjectGroupPython] B_element001  label="B_element : 4"  # scripted group (container) (typed FeaturePython)
  n = 4
  ref = B_element
FEATURE [App::DocumentObjectGroupPython] C_element017  label="C_element : 1"  # scripted group (container) (typed FeaturePython)
  n = 1
  ref = C_element
FEATURE [App::DocumentObjectGroupPython] G4_BORON_CARBIDE  # scripted group (container) (typed FeaturePython)
  Dunit = g/cm3
  Dvalue = 2.52
  Group = -> [B_element001,C_element017]
  conduct = 2
  density = 1
  expand = 3
  formula = G4_BORON_CARBIDE
  name = G4_BORON_CARBIDE
  specific = 4
FEATURE [App::DocumentObjectGroupPython] B_element002  label="B_element : 2"  # scripted group (container) (typed FeaturePython)
  n = 2
  ref = B_element
FEATURE [App::DocumentObjectGroupPython] O_element016  label="O_element : 006"  # scripted group (container) (typed FeaturePython)
  n = 3
  ref = O_element
FEATURE [App::DocumentObjectGroupPython] G4_BORON_OXIDE  # scripted group (container) (typed FeaturePython)
  Dunit = g/cm3
  Dvalue = 1.812
  Group = -> [B_element002,O_element016]
  conduct = 2
  density = 1
  expand = 3
  formula = G4_BORON_OXIDE
  name = G4_BORON_OXIDE
  specific = 4
FEATURE [App::DocumentObjectGroupPython] H_element017  label="H_element : 0.107"  # scripted group (container) (typed FeaturePython)
  n = 0.107
FEATURE [App::DocumentObjectGroupPython] C_element018  label="C_element : 0.145"  # scripted group (container) (typed FeaturePython)
  n = 0.145
FEATURE [App::DocumentObjectGroupPython] N_element012  label="N_element : 0.022"  # scripted group (container) (typed FeaturePython)
  n = 0.022
FEATURE [App::DocumentObjectGroupPython] O_element017  label="O_element : 0.712"  # scripted group (container) (typed FeaturePython)
  n = 0.712
FEATURE [App::DocumentObjectGroupPython] Na_element004  label="Na_element : 0.004"  # scripted group (container) (typed FeaturePython)
  n = 0.002
FEATURE [App::DocumentObjectGroupPython] P_element004  label="P_element : 0.004"  # scripted group (container) (typed FeaturePython)
  n = 0.004
FEATURE [App::DocumentObjectGroupPython] S_element006  label="S_element : 0.005"  # scripted group (container) (typed FeaturePython)
  n = 0.002
FEATURE [App::DocumentObjectGroupPython] Cl_element003  label="Cl_element : 0.004"  # scripted group (container) (typed FeaturePython)
  n = 0.003
FEATURE [App::DocumentObjectGroupPython] K_element002  label="K_element : 0.003"  # scripted group (container) (typed FeaturePython)
  n = 0.003
FEATURE [App::DocumentObjectGroupPython] G4_BRAIN_ICRP  # scripted group (container) (typed FeaturePython)
  Dunit = g/cm3
  Dvalue = 1.04
  Group = -> [H_element017,C_element018,N_element012,O_element017,Na_element004,P_element004,S_element006,Cl_element003,K_element002]
  conduct = 2
  density = 1
  expand = 3
  formula = G4_BRAIN_ICRP
  name = G4_BRAIN_ICRP
  specific = 4
FEATURE [App::DocumentObjectGroupPython] C_element019  label="C_element : 4"  # scripted group (container) (typed FeaturePython)
  n = 4
  ref = C_element
FEATURE [App::DocumentObjectGroupPython] H_element018  label="H_element : 010"  # scripted group (container) (typed FeaturePython)
  n = 10
  ref = H_element
FEATURE [App::DocumentObjectGroupPython] G4_BUTANE  # scripted group (container) (typed FeaturePython)
  Dunit = g/cm3
  Dvalue = 0.00249343
  Group = -> [C_element019,H_element018]
  conduct = 2
  density = 1
  expand = 3
  formula = G4_BUTANE
  name = G4_BUTANE
  specific = 4
FEATURE [App::DocumentObjectGroupPython] C_element020  label="C_element : 008"  # scripted group (container) (typed FeaturePython)
  n = 4
  ref = C_element
FEATURE [App::DocumentObjectGroupPython] H_element019  label="H_element : 011"  # scripted group (container) (typed FeaturePython)
  n = 10
  ref = H_element
FEATURE [App::DocumentObjectGroupPython] O_element018  label="O_element : 007"  # scripted group (container) (typed FeaturePython)
  n = 1
  ref = O_element
FEATURE [App::DocumentObjectGroupPython] G4_N_BUTYL_ALCOHOL  label="G4_N-BUTYL_ALCOHOL"  # scripted group (container) (typed FeaturePython)
  Dunit = g/cm3
  Dvalue = 0.8098
  Group = -> [C_element020,H_element019,O_element018]
  conduct = 2
  density = 1
  expand = 3
  formula = G4_N-BUTYL_ALCOHOL
  name = G4_N-BUTYL_ALCOHOL
  specific = 4
FEATURE [App::DocumentObjectGroupPython] H_element020  label="H_element : 0.025"  # scripted group (container) (typed FeaturePython)
  n = 0.02468
FEATURE [App::DocumentObjectGroupPython] C_element021  label="C_element : 0.502"  # scripted group (container) (typed FeaturePython)
  n = 0.501611
FEATURE [App::DocumentObjectGroupPython] O_element019  label="O_element : 0.005"  # scripted group (container) (typed FeaturePython)
  n = 0.004527
FEATURE [App::DocumentObjectGroupPython] F_element004  label="F_element : 0.465"  # scripted group (container) (typed FeaturePython)
  n = 0.465209
FEATURE [App::DocumentObjectGroupPython] Si_element001  label="Si_element : 0.004"  # scripted group (container) (typed FeaturePython)
  n = 0.003973
FEATURE [App::DocumentObjectGroupPython] G4_C_552  label="G4_C-552"  # scripted group (container) (typed FeaturePython)
  Dunit = g/cm3
  Dvalue = 1.76
  Group = -> [H_element020,C_element021,O_element019,F_element004,Si_element001]
  conduct = 2
  density = 1
  expand = 3
  formula = G4_C-552
  name = G4_C-552
  specific = 4
FEATURE [App::DocumentObjectGroupPython] Cd_element001  label="Cd_element : 1"  # scripted group (container) (typed FeaturePython)
  n = 1
  ref = Cd_element
FEATURE [App::DocumentObjectGroupPython] Te_element001  label="Te_element : 1"  # scripted group (container) (typed FeaturePython)
  n = 1
  ref = Te_element
FEATURE [App::DocumentObjectGroupPython] G4_CADMIUM_TELLURIDE  # scripted group (container) (typed FeaturePython)
  Dunit = g/cm3
  Dvalue = 6.2
  Group = -> [Cd_element001,Te_element001]
  conduct = 2
  density = 1
  expand = 3
  formula = G4_CADMIUM_TELLURIDE
  name = G4_CADMIUM_TELLURIDE
  specific = 4
FEATURE [App::DocumentObjectGroupPython] Cd_element002  label="Cd_element : 002"  # scripted group (container) (typed FeaturePython)
  n = 1
  ref = Cd_element
FEATURE [App::DocumentObjectGroupPython] W_element001  label="W_element : 1"  # scripted group (container) (typed FeaturePython)
  n = 1
  ref = W_element
FEATURE [App::DocumentObjectGroupPython] O_element020  label="O_element : 008"  # scripted group (container) (typed FeaturePython)
  n = 4
  ref = O_element
FEATURE [App::DocumentObjectGroupPython] G4_CADMIUM_TUNGSTATE  # scripted group (container) (typed FeaturePython)
  Dunit = g/cm3
  Dvalue = 7.9
  Group = -> [Cd_element002,W_element001,O_element020]
  conduct = 2
  density = 1
  expand = 3
  formula = G4_CADMIUM_TUNGSTATE
  name = G4_CADMIUM_TUNGSTATE
  specific = 4
FEATURE [App::DocumentObjectGroupPython] Ca_element005  label="Ca_element : 1"  # scripted group (container) (typed FeaturePython)
  n = 1
  ref = Ca_element
FEATURE [App::DocumentObjectGroupPython] C_element022  label="C_element : 009"  # scripted group (container) (typed FeaturePython)
  n = 1
  ref = C_element
FEATURE [App::DocumentObjectGroupPython] O_element021  label="O_element : 009"  # scripted group (container) (typed FeaturePython)
  n = 3
  ref = O_element
FEATURE [App::DocumentObjectGroupPython] G4_CALCIUM_CARBONATE  # scripted group (container) (typed FeaturePython)
  Dunit = g/cm3
  Dvalue = 2.8
  Group = -> [Ca_element005,C_element022,O_element021]
  conduct = 2
  density = 1
  expand = 3
  formula = G4_CALCIUM_CARBONATE
  name = G4_CALCIUM_CARBONATE
  specific = 4
FEATURE [App::DocumentObjectGroupPython] Ca_element006  label="Ca_element : 002"  # scripted group (container) (typed FeaturePython)
  n = 1
  ref = Ca_element
FEATURE [App::DocumentObjectGroupPython] F_element005  label="F_element : 003"  # scripted group (container) (typed FeaturePython)
  n = 2
  ref = F_element
FEATURE [App::DocumentObjectGroupPython] G4_CALCIUM_FLUORIDE  # scripted group (container) (typed FeaturePython)
  Dunit = g/cm3
  Dvalue = 3.18
  Group = -> [Ca_element006,F_element005]
  conduct = 2
  density = 1
  expand = 3
  formula = G4_CALCIUM_FLUORIDE
  name = G4_CALCIUM_FLUORIDE
  specific = 4
FEATURE [App::DocumentObjectGroupPython] Ca_element007  label="Ca_element : 003"  # scripted group (container) (typed FeaturePython)
  n = 1
  ref = Ca_element
FEATURE [App::DocumentObjectGroupPython] O_element022  label="O_element : 010"  # scripted group (container) (typed FeaturePython)
  n = 1
  ref = O_element
FEATURE [App::DocumentObjectGroupPython] G4_CALCIUM_OXIDE  # scripted group (container) (typed FeaturePython)
  Dunit = g/cm3
  Dvalue = 3.3
  Group = -> [Ca_element007,O_element022]
  conduct = 2
  density = 1
  expand = 3
  formula = G4_CALCIUM_OXIDE
  name = G4_CALCIUM_OXIDE
  specific = 4
FEATURE [App::DocumentObjectGroupPython] Ca_element008  label="Ca_element : 004"  # scripted group (container) (typed FeaturePython)
  n = 1
  ref = Ca_element
FEATURE [App::DocumentObjectGroupPython] S_element007  label="S_element : 002"  # scripted group (container) (typed FeaturePython)
  n = 1
  ref = S_element
FEATURE [App::DocumentObjectGroupPython] O_element023  label="O_element : 011"  # scripted group (container) (typed FeaturePython)
  n = 4
  ref = O_element
FEATURE [App::DocumentObjectGroupPython] G4_CALCIUM_SULFATE  # scripted group (container) (typed FeaturePython)
  Dunit = g/cm3
  Dvalue = 2.96
  Group = -> [Ca_element008,S_element007,O_element023]
  conduct = 2
  density = 1
  expand = 3
  formula = G4_CALCIUM_SULFATE
  name = G4_CALCIUM_SULFATE
  specific = 4
FEATURE [App::DocumentObjectGroupPython] Ca_element009  label="Ca_element : 005"  # scripted group (container) (typed FeaturePython)
  n = 1
  ref = Ca_element
FEATURE [App::DocumentObjectGroupPython] W_element002  label="W_element : 002"  # scripted group (container) (typed FeaturePython)
  n = 1
  ref = W_element
FEATURE [App::DocumentObjectGroupPython] O_element024  label="O_element : 012"  # scripted group (container) (typed FeaturePython)
  n = 4
  ref = O_element
FEATURE [App::DocumentObjectGroupPython] G4_CALCIUM_TUNGSTATE  # scripted group (container) (typed FeaturePython)
  Dunit = g/cm3
  Dvalue = 6.062
  Group = -> [Ca_element009,W_element002,O_element024]
  conduct = 2
  density = 1
  expand = 3
  formula = G4_CALCIUM_TUNGSTATE
  name = G4_CALCIUM_TUNGSTATE
  specific = 4
FEATURE [App::DocumentObjectGroupPython] C_element023  label="C_element : 010"  # scripted group (container) (typed FeaturePython)
  n = 1
  ref = C_element
FEATURE [App::DocumentObjectGroupPython] O_element025  label="O_element : 013"  # scripted group (container) (typed FeaturePython)
  n = 2
  ref = O_element
FEATURE [App::DocumentObjectGroupPython] G4_CARBON_DIOXIDE  # scripted group (container) (typed FeaturePython)
  Dunit = g/cm3
  Dvalue = 0.00184212
  Group = -> [C_element023,O_element025]
  conduct = 2
  density = 1
  expand = 3
  formula = G4_CARBON_DIOXIDE
  name = G4_CARBON_DIOXIDE
  specific = 4
FEATURE [App::DocumentObjectGroupPython] C_element024  label="C_element : 011"  # scripted group (container) (typed FeaturePython)
  n = 1
  ref = C_element
FEATURE [App::DocumentObjectGroupPython] Cl_element004  label="Cl_element : 4"  # scripted group (container) (typed FeaturePython)
  n = 4
  ref = Cl_element
FEATURE [App::DocumentObjectGroupPython] G4_CARBON_TETRACHLORIDE  # scripted group (container) (typed FeaturePython)
  Dunit = g/cm3
  Dvalue = 1.594
  Group = -> [C_element024,Cl_element004]
  conduct = 2
  density = 1
  expand = 3
  formula = G4_CARBON_TETRACHLORIDE
  name = G4_CARBON_TETRACHLORIDE
  specific = 4
FEATURE [App::DocumentObjectGroupPython] C_element025  label="C_element : 012"  # scripted group (container) (typed FeaturePython)
  n = 6
  ref = C_element
FEATURE [App::DocumentObjectGroupPython] H_element021  label="H_element : 012"  # scripted group (container) (typed FeaturePython)
  n = 10
  ref = H_element
FEATURE [App::DocumentObjectGroupPython] O_element026  label="O_element : 5"  # scripted group (container) (typed FeaturePython)
  n = 5
  ref = O_element
FEATURE [App::DocumentObjectGroupPython] G4_CELLULOSE_CELLOPHANE  # scripted group (container) (typed FeaturePython)
  Dunit = g/cm3
  Dvalue = 1.42
  Group = -> [C_element025,H_element021,O_element026]
  conduct = 2
  density = 1
  expand = 3
  formula = G4_CELLULOSE_CELLOPHANE
  name = G4_CELLULOSE_CELLOPHANE
  specific = 4
FEATURE [App::DocumentObjectGroupPython] H_element022  label="H_element : 0.067"  # scripted group (container) (typed FeaturePython)
  n = 0.067125
FEATURE [App::DocumentObjectGroupPython] C_element026  label="C_element : 0.545"  # scripted group (container) (typed FeaturePython)
  n = 0.545403
FEATURE [App::DocumentObjectGroupPython] O_element027  label="O_element : 0.387"  # scripted group (container) (typed FeaturePython)
  n = 0.387472
FEATURE [App::DocumentObjectGroupPython] G4_CELLULOSE_BUTYRATE  # scripted group (container) (typed FeaturePython)
  Dunit = g/cm3
  Dvalue = 1.2
  Group = -> [H_element022,C_element026,O_element027]
  conduct = 2
  density = 1
  expand = 3
  formula = G4_CELLULOSE_BUTYRATE
  name = G4_CELLULOSE_BUTYRATE
  specific = 4
FEATURE [App::DocumentObjectGroupPython] H_element023  label="H_element : 0.029"  # scripted group (container) (typed FeaturePython)
  n = 0.029216
FEATURE [App::DocumentObjectGroupPython] C_element027  label="C_element : 0.271"  # scripted group (container) (typed FeaturePython)
  n = 0.271296
FEATURE [App::DocumentObjectGroupPython] N_element013  label="N_element : 0.121"  # scripted group (container) (typed FeaturePython)
  n = 0.121276
FEATURE [App::DocumentObjectGroupPython] O_element028  label="O_element : 0.578"  # scripted group (container) (typed FeaturePython)
  n = 0.578212
FEATURE [App::DocumentObjectGroupPython] G4_CELLULOSE_NITRATE  # scripted group (container) (typed FeaturePython)
  Dunit = g/cm3
  Dvalue = 1.49
  Group = -> [H_element023,C_element027,N_element013,O_element028]
  conduct = 2
  density = 1
  expand = 3
  formula = G4_CELLULOSE_NITRATE
  name = G4_CELLULOSE_NITRATE
  specific = 4
FEATURE [App::DocumentObjectGroupPython] H_element024  label="H_element : 0.108"  # scripted group (container) (typed FeaturePython)
  n = 0.107596
FEATURE [App::DocumentObjectGroupPython] N_element014  label="N_element : 0.001"  # scripted group (container) (typed FeaturePython)
  n = 0.0008
FEATURE [App::DocumentObjectGroupPython] O_element029  label="O_element : 0.875"  # scripted group (container) (typed FeaturePython)
  n = 0.874976
FEATURE [App::DocumentObjectGroupPython] S_element008  label="S_element : 0.015"  # scripted group (container) (typed FeaturePython)
  n = 0.014627
FEATURE [App::DocumentObjectGroupPython] Ce_element001  label="Ce_element : 0.002"  # scripted group (container) (typed FeaturePython)
  n = 0.002001
FEATURE [App::DocumentObjectGroupPython] G4_CERIC_SULFATE  # scripted group (container) (typed FeaturePython)
  Dunit = g/cm3
  Dvalue = 1.03
  Group = -> [H_element024,N_element014,O_element029,S_element008,Ce_element001]
  conduct = 2
  density = 1
  expand = 3
  formula = G4_CERIC_SULFATE
  name = G4_CERIC_SULFATE
  specific = 4
FEATURE [App::DocumentObjectGroupPython] Cs_element001  label="Cs_element : 1"  # scripted group (container) (typed FeaturePython)
  n = 1
  ref = Cs_element
FEATURE [App::DocumentObjectGroupPython] F_element006  label="F_element : 1"  # scripted group (container) (typed FeaturePython)
  n = 1
  ref = F_element
FEATURE [App::DocumentObjectGroupPython] G4_CESIUM_FLUORIDE  # scripted group (container) (typed FeaturePython)
  Dunit = g/cm3
  Dvalue = 4.115
  Group = -> [Cs_element001,F_element006]
  conduct = 2
  density = 1
  expand = 3
  formula = G4_CESIUM_FLUORIDE
  name = G4_CESIUM_FLUORIDE
  specific = 4
FEATURE [App::DocumentObjectGroupPython] Cs_element002  label="Cs_element : 002"  # scripted group (container) (typed FeaturePython)
  n = 1
  ref = Cs_element
FEATURE [App::DocumentObjectGroupPython] I_element001  label="I_element : 1"  # scripted group (container) (typed FeaturePython)
  n = 1
  ref = I_element
FEATURE [App::DocumentObjectGroupPython] G4_CESIUM_IODIDE  # scripted group (container) (typed FeaturePython)
  Dunit = g/cm3
  Dvalue = 4.51
  Group = -> [Cs_element002,I_element001]
  conduct = 2
  density = 1
  expand = 3
  formula = G4_CESIUM_IODIDE
  name = G4_CESIUM_IODIDE
  specific = 4
FEATURE [App::DocumentObjectGroupPython] C_element028  label="C_element : 013"  # scripted group (container) (typed FeaturePython)
  n = 6
  ref = C_element
FEATURE [App::DocumentObjectGroupPython] H_element025  label="H_element : 013"  # scripted group (container) (typed FeaturePython)
  n = 5
  ref = H_element
FEATURE [App::DocumentObjectGroupPython] Cl_element005  label="Cl_element : 1"  # scripted group (container) (typed FeaturePython)
  n = 1
  ref = Cl_element
FEATURE [App::DocumentObjectGroupPython] G4_CHLOROBENZENE  # scripted group (container) (typed FeaturePython)
  Dunit = g/cm3
  Dvalue = 1.1058
  Group = -> [C_element028,H_element025,Cl_element005]
  conduct = 2
  density = 1
  expand = 3
  formula = G4_CHLOROBENZENE
  name = G4_CHLOROBENZENE
  specific = 4
FEATURE [App::DocumentObjectGroupPython] C_element029  label="C_element : 014"  # scripted group (container) (typed FeaturePython)
  n = 1
  ref = C_element
FEATURE [App::DocumentObjectGroupPython] H_element026  label="H_element : 1"  # scripted group (container) (typed FeaturePython)
  n = 1
  ref = H_element
FEATURE [App::DocumentObjectGroupPython] Cl_element006  label="Cl_element : 3"  # scripted group (container) (typed FeaturePython)
  n = 3
  ref = Cl_element
FEATURE [App::DocumentObjectGroupPython] G4_CHLOROFORM  # scripted group (container) (typed FeaturePython)
  Dunit = g/cm3
  Dvalue = 1.4832
  Group = -> [C_element029,H_element026,Cl_element006]
  conduct = 2
  density = 1
  expand = 3
  formula = G4_CHLOROFORM
  name = G4_CHLOROFORM
  specific = 4
FEATURE [App::DocumentObjectGroupPython] H_element027  label="H_element : 0.010"  # scripted group (container) (typed FeaturePython)
  n = 0.01
FEATURE [App::DocumentObjectGroupPython] C_element030  label="C_element : 0.001"  # scripted group (container) (typed FeaturePython)
  n = 0.001
FEATURE [App::DocumentObjectGroupPython] O_element030  label="O_element : 0.529"  # scripted group (container) (typed FeaturePython)
  n = 0.529107
FEATURE [App::DocumentObjectGroupPython] Na_element005  label="Na_element : 0.016"  # scripted group (container) (typed FeaturePython)
  n = 0.016
FEATURE [App::DocumentObjectGroupPython] Mg_element003  label="Mg_element : 0.004"  # scripted group (container) (typed FeaturePython)
  n = 0.002
FEATURE [App::DocumentObjectGroupPython] Al_element002  label="Al_element : 0.034"  # scripted group (container) (typed FeaturePython)
  n = 0.033872
FEATURE [App::DocumentObjectGroupPython] Si_element002  label="Si_element : 0.337"  # scripted group (container) (typed FeaturePython)
  n = 0.337021
FEATURE [App::DocumentObjectGroupPython] K_element003  label="K_element : 0.013"  # scripted group (container) (typed FeaturePython)
  n = 0.013
FEATURE [App::DocumentObjectGroupPython] Ca_element010  label="Ca_element : 0.044"  # scripted group (container) (typed FeaturePython)
  n = 0.044
FEATURE [App::DocumentObjectGroupPython] Fe_element002  label="Fe_element : 0.014"  # scripted group (container) (typed FeaturePython)
  n = 0.014
FEATURE [App::DocumentObjectGroupPython] G4_CONCRETE  # scripted group (container) (typed FeaturePython)
  Dunit = g/cm3
  Dvalue = 2.3
  Group = -> [H_element027,C_element030,O_element030,Na_element005,Mg_element003,Al_element002,Si_element002,K_element003,Ca_element010,Fe_element002]
  conduct = 2
  density = 1
  expand = 3
  formula = G4_CONCRETE
  name = G4_CONCRETE
  specific = 4
FEATURE [App::DocumentObjectGroupPython] C_element031  label="C_element : 015"  # scripted group (container) (typed FeaturePython)
  n = 6
  ref = C_element
FEATURE [App::DocumentObjectGroupPython] H_element028  label="H_element : 12"  # scripted group (container) (typed FeaturePython)
  n = 12
  ref = H_element
FEATURE [App::DocumentObjectGroupPython] G4_CYCLOHEXANE  # scripted group (container) (typed FeaturePython)
  Dunit = g/cm3
  Dvalue = 0.779
  Group = -> [C_element031,H_element028]
  conduct = 2
  density = 1
  expand = 3
  formula = G4_CYCLOHEXANE
  name = G4_CYCLOHEXANE
  specific = 4
FEATURE [App::DocumentObjectGroupPython] C_element032  label="C_element : 016"  # scripted group (container) (typed FeaturePython)
  n = 6
  ref = C_element
FEATURE [App::DocumentObjectGroupPython] H_element029  label="H_element : 4"  # scripted group (container) (typed FeaturePython)
  n = 4
  ref = H_element
FEATURE [App::DocumentObjectGroupPython] Cl_element007  label="Cl_element : 2"  # scripted group (container) (typed FeaturePython)
  n = 2
  ref = Cl_element
FEATURE [App::DocumentObjectGroupPython] G4_1_2_DICHLOROBENZENE  label="G4_1.2-DICHLOROBENZENE"  # scripted group (container) (typed FeaturePython)
  Dunit = g/cm3
  Dvalue = 1.3048
  Group = -> [C_element032,H_element029,Cl_element007]
  conduct = 2
  density = 1
  expand = 3
  formula = G4_1.2-DICHLOROBENZENE
  name = G4_1.2-DICHLOROBENZENE
  specific = 4
FEATURE [App::DocumentObjectGroupPython] C_element033  label="C_element : 017"  # scripted group (container) (typed FeaturePython)
  n = 4
  ref = C_element
FEATURE [App::DocumentObjectGroupPython] H_element030  label="H_element : 8"  # scripted group (container) (typed FeaturePython)
  n = 8
  ref = H_element
FEATURE [App::DocumentObjectGroupPython] O_element031  label="O_element : 014"  # scripted group (container) (typed FeaturePython)
  n = 1
  ref = O_element
FEATURE [App::DocumentObjectGroupPython] Cl_element008  label="Cl_element : 005"  # scripted group (container) (typed FeaturePython)
  n = 2
  ref = Cl_element
FEATURE [App::DocumentObjectGroupPython] G4_DICHLORODIETHYL_ETHER  # scripted group (container) (typed FeaturePython)
  Dunit = g/cm3
  Dvalue = 1.2199
  Group = -> [C_element033,H_element030,O_element031,Cl_element008]
  conduct = 2
  density = 1
  expand = 3
  formula = G4_DICHLORODIETHYL_ETHER
  name = G4_DICHLORODIETHYL_ETHER
  specific = 4
FEATURE [App::DocumentObjectGroupPython] C_element034  label="C_element : 018"  # scripted group (container) (typed FeaturePython)
  n = 2
  ref = C_element
FEATURE [App::DocumentObjectGroupPython] H_element031  label="H_element : 014"  # scripted group (container) (typed FeaturePython)
  n = 4
  ref = H_element
FEATURE [App::DocumentObjectGroupPython] Cl_element009  label="Cl_element : 006"  # scripted group (container) (typed FeaturePython)
  n = 2
  ref = Cl_element
FEATURE [App::DocumentObjectGroupPython] G4_1_2_DICHLOROETHANE  label="G4_1.2-DICHLOROETHANE"  # scripted group (container) (typed FeaturePython)
  Dunit = g/cm3
  Dvalue = 1.2351
  Group = -> [C_element034,H_element031,Cl_element009]
  conduct = 2
  density = 1
  expand = 3
  formula = G4_1.2-DICHLOROETHANE
  name = G4_1.2-DICHLOROETHANE
  specific = 4
FEATURE [App::DocumentObjectGroupPython] C_element035  label="C_element : 019"  # scripted group (container) (typed FeaturePython)
  n = 4
  ref = C_element
FEATURE [App::DocumentObjectGroupPython] H_element032  label="H_element : 015"  # scripted group (container) (typed FeaturePython)
  n = 10
  ref = H_element
FEATURE [App::DocumentObjectGroupPython] O_element032  label="O_element : 015"  # scripted group (container) (typed FeaturePython)
  n = 1
  ref = O_element
FEATURE [App::DocumentObjectGroupPython] G4_DIETHYL_ETHER  # scripted group (container) (typed FeaturePython)
  Dunit = g/cm3
  Dvalue = 0.71378
  Group = -> [C_element035,H_element032,O_element032]
  conduct = 2
  density = 1
  expand = 3
  formula = G4_DIETHYL_ETHER
  name = G4_DIETHYL_ETHER
  specific = 4
FEATURE [App::DocumentObjectGroupPython] C_element036  label="C_element : 020"  # scripted group (container) (typed FeaturePython)
  n = 3
  ref = C_element
FEATURE [App::DocumentObjectGroupPython] H_element033  label="H_element : 016"  # scripted group (container) (typed FeaturePython)
  n = 7
  ref = H_element
FEATURE [App::DocumentObjectGroupPython] N_element015  label="N_element : 008"  # scripted group (container) (typed FeaturePython)
  n = 1
  ref = N_element
FEATURE [App::DocumentObjectGroupPython] O_element033  label="O_element : 016"  # scripted group (container) (typed FeaturePython)
  n = 1
  ref = O_element
FEATURE [App::DocumentObjectGroupPython] G4_N_N_DIMETHYL_FORMAMIDE  label="G4_N.N-DIMETHYL_FORMAMIDE"  # scripted group (container) (typed FeaturePython)
  Dunit = g/cm3
  Dvalue = 0.9487
  Group = -> [C_element036,H_element033,N_element015,O_element033]
  conduct = 2
  density = 1
  expand = 3
  formula = G4_N.N-DIMETHYL_FORMAMIDE
  name = G4_N.N-DIMETHYL_FORMAMIDE
  specific = 4
FEATURE [App::DocumentObjectGroupPython] C_element037  label="C_element : 021"  # scripted group (container) (typed FeaturePython)
  n = 2
  ref = C_element
FEATURE [App::DocumentObjectGroupPython] H_element034  label="H_element : 017"  # scripted group (container) (typed FeaturePython)
  n = 6
  ref = H_element
FEATURE [App::DocumentObjectGroupPython] O_element034  label="O_element : 017"  # scripted group (container) (typed FeaturePython)
  n = 1
  ref = O_element
FEATURE [App::DocumentObjectGroupPython] S_element009  label="S_element : 003"  # scripted group (container) (typed FeaturePython)
  n = 1
  ref = S_element
FEATURE [App::DocumentObjectGroupPython] G4_DIMETHYL_SULFOXIDE  # scripted group (container) (typed FeaturePython)
  Dunit = g/cm3
  Dvalue = 1.1014
  Group = -> [C_element037,H_element034,O_element034,S_element009]
  conduct = 2
  density = 1
  expand = 3
  formula = G4_DIMETHYL_SULFOXIDE
  name = G4_DIMETHYL_SULFOXIDE
  specific = 4
FEATURE [App::DocumentObjectGroupPython] C_element038  label="C_element : 022"  # scripted group (container) (typed FeaturePython)
  n = 2
  ref = C_element
FEATURE [App::DocumentObjectGroupPython] H_element035  label="H_element : 018"  # scripted group (container) (typed FeaturePython)
  n = 6
  ref = H_element
FEATURE [App::DocumentObjectGroupPython] G4_ETHANE  # scripted group (container) (typed FeaturePython)
  Dunit = g/cm3
  Dvalue = 0.00125324
  Group = -> [C_element038,H_element035]
  conduct = 2
  density = 1
  expand = 3
  formula = G4_ETHANE
  name = G4_ETHANE
  specific = 4
FEATURE [App::DocumentObjectGroupPython] C_element039  label="C_element : 023"  # scripted group (container) (typed FeaturePython)
  n = 2
  ref = C_element
FEATURE [App::DocumentObjectGroupPython] H_element036  label="H_element : 019"  # scripted group (container) (typed FeaturePython)
  n = 6
  ref = H_element
FEATURE [App::DocumentObjectGroupPython] O_element035  label="O_element : 018"  # scripted group (container) (typed FeaturePython)
  n = 1
  ref = O_element
FEATURE [App::DocumentObjectGroupPython] G4_ETHYL_ALCOHOL  # scripted group (container) (typed FeaturePython)
  Dunit = g/cm3
  Dvalue = 0.7893
  Group = -> [C_element039,H_element036,O_element035]
  conduct = 2
  density = 1
  expand = 3
  formula = G4_ETHYL_ALCOHOL
  name = G4_ETHYL_ALCOHOL
  specific = 4
FEATURE [App::DocumentObjectGroupPython] H_element037  label="H_element : 0.090"  # scripted group (container) (typed FeaturePython)
  n = 0.090027
FEATURE [App::DocumentObjectGroupPython] C_element040  label="C_element : 0.585"  # scripted group (container) (typed FeaturePython)
  n = 0.585182
FEATURE [App::DocumentObjectGroupPython] O_element036  label="O_element : 0.325"  # scripted group (container) (typed FeaturePython)
  n = 0.324791
FEATURE [App::DocumentObjectGroupPython] G4_ETHYL_CELLULOSE  # scripted group (container) (typed FeaturePython)
  Dunit = g/cm3
  Dvalue = 1.13
  Group = -> [H_element037,C_element040,O_element036]
  conduct = 2
  density = 1
  expand = 3
  formula = G4_ETHYL_CELLULOSE
  name = G4_ETHYL_CELLULOSE
  specific = 4
FEATURE [App::DocumentObjectGroupPython] C_element041  label="C_element : 024"  # scripted group (container) (typed FeaturePython)
  n = 2
  ref = C_element
FEATURE [App::DocumentObjectGroupPython] H_element038  label="H_element : 020"  # scripted group (container) (typed FeaturePython)
  n = 4
  ref = H_element
FEATURE [App::DocumentObjectGroupPython] G4_ETHYLENE  # scripted group (container) (typed FeaturePython)
  Dunit = g/cm3
  Dvalue = 0.00117497
  Group = -> [C_element041,H_element038]
  conduct = 2
  density = 1
  expand = 3
  formula = G4_ETHYLENE
  name = G4_ETHYLENE
  specific = 4
FEATURE [App::DocumentObjectGroupPython] H_element039  label="H_element : 0.096"  # scripted group (container) (typed FeaturePython)
  n = 0.096
FEATURE [App::DocumentObjectGroupPython] C_element042  label="C_element : 0.195"  # scripted group (container) (typed FeaturePython)
  n = 0.195
FEATURE [App::DocumentObjectGroupPython] N_element016  label="N_element : 0.057"  # scripted group (container) (typed FeaturePython)
  n = 0.057
FEATURE [App::DocumentObjectGroupPython] O_element037  label="O_element : 0.646"  # scripted group (container) (typed FeaturePython)
  n = 0.646
FEATURE [App::DocumentObjectGroupPython] Na_element006  label="Na_element : 0.017"  # scripted group (container) (typed FeaturePython)
  n = 0.001
FEATURE [App::DocumentObjectGroupPython] P_element005  label="P_element : 0.104"  # scripted group (container) (typed FeaturePython)
  n = 0.001
FEATURE [App::DocumentObjectGroupPython] S_element010  label="S_element : 0.016"  # scripted group (container) (typed FeaturePython)
  n = 0.003
FEATURE [App::DocumentObjectGroupPython] Cl_element010  label="Cl_element : 0.005"  # scripted group (container) (typed FeaturePython)
  n = 0.001
FEATURE [App::DocumentObjectGroupPython] G4_EYE_LENS_ICRP  # scripted group (container) (typed FeaturePython)
  Dunit = g/cm3
  Dvalue = 1.07
  Group = -> [H_element039,C_element042,N_element016,O_element037,Na_element006,P_element005,S_element010,Cl_element010]
  conduct = 2
  density = 1
  expand = 3
  formula = G4_EYE_LENS_ICRP
  name = G4_EYE_LENS_ICRP
  specific = 4
FEATURE [App::DocumentObjectGroupPython] Fe_element003  label="Fe_element : 2"  # scripted group (container) (typed FeaturePython)
  n = 2
  ref = Fe_element
FEATURE [App::DocumentObjectGroupPython] O_element038  label="O_element : 019"  # scripted group (container) (typed FeaturePython)
  n = 3
  ref = O_element
FEATURE [App::DocumentObjectGroupPython] G4_FERRIC_OXIDE  # scripted group (container) (typed FeaturePython)
  Dunit = g/cm3
  Dvalue = 5.2
  Group = -> [Fe_element003,O_element038]
  conduct = 2
  density = 1
  expand = 3
  formula = G4_FERRIC_OXIDE
  name = G4_FERRIC_OXIDE
  specific = 4
FEATURE [App::DocumentObjectGroupPython] Fe_element004  label="Fe_element : 1"  # scripted group (container) (typed FeaturePython)
  n = 1
  ref = Fe_element
FEATURE [App::DocumentObjectGroupPython] B_element003  label="B_element : 1"  # scripted group (container) (typed FeaturePython)
  n = 1
  ref = B_element
FEATURE [App::DocumentObjectGroupPython] G4_FERROBORIDE  # scripted group (container) (typed FeaturePython)
  Dunit = g/cm3
  Dvalue = 7.15
  Group = -> [Fe_element004,B_element003]
  conduct = 2
  density = 1
  expand = 3
  formula = G4_FERROBORIDE
  name = G4_FERROBORIDE
  specific = 4
FEATURE [App::DocumentObjectGroupPython] Fe_element005  label="Fe_element : 003"  # scripted group (container) (typed FeaturePython)
  n = 1
  ref = Fe_element
FEATURE [App::DocumentObjectGroupPython] O_element039  label="O_element : 020"  # scripted group (container) (typed FeaturePython)
  n = 1
  ref = O_element
FEATURE [App::DocumentObjectGroupPython] G4_FERROUS_OXIDE  # scripted group (container) (typed FeaturePython)
  Dunit = g/cm3
  Dvalue = 5.7
  Group = -> [Fe_element005,O_element039]
  conduct = 2
  density = 1
  expand = 3
  formula = G4_FERROUS_OXIDE
  name = G4_FERROUS_OXIDE
  specific = 4
FEATURE [App::DocumentObjectGroupPython] H_element040  label="H_element : 0.115"  # scripted group (container) (typed FeaturePython)
  n = 0.108259
FEATURE [App::DocumentObjectGroupPython] N_element017  label="N_element : 0.000"  # scripted group (container) (typed FeaturePython)
  n = 2.7e-05
FEATURE [App::DocumentObjectGroupPython] O_element040  label="O_element : 0.879"  # scripted group (container) (typed FeaturePython)
  n = 0.878636
FEATURE [App::DocumentObjectGroupPython] Na_element007  label="Na_element : 0.000"  # scripted group (container) (typed FeaturePython)
  n = 2.2e-05
FEATURE [App::DocumentObjectGroupPython] S_element011  label="S_element : 0.013"  # scripted group (container) (typed FeaturePython)
  n = 0.012968
FEATURE [App::DocumentObjectGroupPython] Cl_element011  label="Cl_element : 0.000"  # scripted group (container) (typed FeaturePython)
  n = 3.4e-05
FEATURE [App::DocumentObjectGroupPython] Fe_element006  label="Fe_element : 0.000"  # scripted group (container) (typed FeaturePython)
  n = 5.4e-05
FEATURE [App::DocumentObjectGroupPython] G4_FERROUS_SULFATE  # scripted group (container) (typed FeaturePython)
  Dunit = g/cm3
  Dvalue = 1.024
  Group = -> [H_element040,N_element017,O_element040,Na_element007,S_element011,Cl_element011,Fe_element006]
  conduct = 2
  density = 1
  expand = 3
  formula = G4_FERROUS_SULFATE
  name = G4_FERROUS_SULFATE
  specific = 4
FEATURE [App::DocumentObjectGroupPython] C_element043  label="C_element : 0.099"  # scripted group (container) (typed FeaturePython)
  n = 0.099335
FEATURE [App::DocumentObjectGroupPython] F_element007  label="F_element : 0.314"  # scripted group (container) (typed FeaturePython)
  n = 0.314247
FEATURE [App::DocumentObjectGroupPython] Cl_element012  label="Cl_element : 0.586"  # scripted group (container) (typed FeaturePython)
  n = 0.586418
FEATURE [App::DocumentObjectGroupPython] G4_FREON_12  label="G4_FREON-12"  # scripted group (container) (typed FeaturePython)
  Dunit = g/cm3
  Dvalue = 1.12
  Group = -> [C_element043,F_element007,Cl_element012]
  conduct = 2
  density = 1
  expand = 3
  formula = G4_FREON-12
  name = G4_FREON-12
  specific = 4
FEATURE [App::DocumentObjectGroupPython] C_element044  label="C_element : 0.057"  # scripted group (container) (typed FeaturePython)
  n = 0.057245
FEATURE [App::DocumentObjectGroupPython] F_element008  label="F_element : 0.181"  # scripted group (container) (typed FeaturePython)
  n = 0.181096
FEATURE [App::DocumentObjectGroupPython] Br_element001  label="Br_element : 0.762"  # scripted group (container) (typed FeaturePython)
  n = 0.761659
FEATURE [App::DocumentObjectGroupPython] G4_FREON_12B2  label="G4_FREON-12B2"  # scripted group (container) (typed FeaturePython)
  Dunit = g/cm3
  Dvalue = 1.8
  Group = -> [C_element044,F_element008,Br_element001]
  conduct = 2
  density = 1
  expand = 3
  formula = G4_FREON-12B2
  name = G4_FREON-12B2
  specific = 4
FEATURE [App::DocumentObjectGroupPython] C_element045  label="C_element : 0.115"  # scripted group (container) (typed FeaturePython)
  n = 0.114983
FEATURE [App::DocumentObjectGroupPython] F_element009  label="F_element : 0.546"  # scripted group (container) (typed FeaturePython)
  n = 0.545621
FEATURE [App::DocumentObjectGroupPython] Cl_element013  label="Cl_element : 0.339"  # scripted group (container) (typed FeaturePython)
  n = 0.339396
FEATURE [App::DocumentObjectGroupPython] G4_FREON_13  label="G4_FREON-13"  # scripted group (container) (typed FeaturePython)
  Dunit = g/cm3
  Dvalue = 0.95
  Group = -> [C_element045,F_element009,Cl_element013]
  conduct = 2
  density = 1
  expand = 3
  formula = G4_FREON-13
  name = G4_FREON-13
  specific = 4
FEATURE [App::DocumentObjectGroupPython] C_element046  label="C_element : 025"  # scripted group (container) (typed FeaturePython)
  n = 1
  ref = C_element
FEATURE [App::DocumentObjectGroupPython] F_element010  label="F_element : 3"  # scripted group (container) (typed FeaturePython)
  n = 3
  ref = F_element
FEATURE [App::DocumentObjectGroupPython] Br_element002  label="Br_element : 1"  # scripted group (container) (typed FeaturePython)
  n = 1
  ref = Br_element
FEATURE [App::DocumentObjectGroupPython] G4_FREON_13B1  label="G4_FREON-13B1"  # scripted group (container) (typed FeaturePython)
  Dunit = g/cm3
  Dvalue = 1.5
  Group = -> [C_element046,F_element010,Br_element002]
  conduct = 2
  density = 1
  expand = 3
  formula = G4_FREON-13B1
  name = G4_FREON-13B1
  specific = 4
FEATURE [App::DocumentObjectGroupPython] C_element047  label="C_element : 0.061"  # scripted group (container) (typed FeaturePython)
  n = 0.061309
FEATURE [App::DocumentObjectGroupPython] F_element011  label="F_element : 0.291"  # scripted group (container) (typed FeaturePython)
  n = 0.290924
FEATURE [App::DocumentObjectGroupPython] I_element002  label="I_element : 0.648"  # scripted group (container) (typed FeaturePython)
  n = 0.647767
FEATURE [App::DocumentObjectGroupPython] G4_FREON_13I1  label="G4_FREON-13I1"  # scripted group (container) (typed FeaturePython)
  Dunit = g/cm3
  Dvalue = 1.8
  Group = -> [C_element047,F_element011,I_element002]
  conduct = 2
  density = 1
  expand = 3
  formula = G4_FREON-13I1
  name = G4_FREON-13I1
  specific = 4
FEATURE [App::DocumentObjectGroupPython] Gd_element001  label="Gd_element : 2"  # scripted group (container) (typed FeaturePython)
  n = 2
  ref = Gd_element
FEATURE [App::DocumentObjectGroupPython] O_element041  label="O_element : 021"  # scripted group (container) (typed FeaturePython)
  n = 2
  ref = O_element
FEATURE [App::DocumentObjectGroupPython] S_element012  label="S_element : 004"  # scripted group (container) (typed FeaturePython)
  n = 1
  ref = S_element
FEATURE [App::DocumentObjectGroupPython] G4_GADOLINIUM_OXYSULFIDE  # scripted group (container) (typed FeaturePython)
  Dunit = g/cm3
  Dvalue = 7.44
  Group = -> [Gd_element001,O_element041,S_element012]
  conduct = 2
  density = 1
  expand = 3
  formula = G4_GADOLINIUM_OXYSULFIDE
  name = G4_GADOLINIUM_OXYSULFIDE
  specific = 4
FEATURE [App::DocumentObjectGroupPython] Ga_element001  label="Ga_element : 1"  # scripted group (container) (typed FeaturePython)
  n = 1
  ref = Ga_element
FEATURE [App::DocumentObjectGroupPython] As_element001  label="As_element : 1"  # scripted group (container) (typed FeaturePython)
  n = 1
  ref = As_element
FEATURE [App::DocumentObjectGroupPython] G4_GALLIUM_ARSENIDE  # scripted group (container) (typed FeaturePython)
  Dunit = g/cm3
  Dvalue = 5.31
  Group = -> [Ga_element001,As_element001]
  conduct = 2
  density = 1
  expand = 3
  formula = G4_GALLIUM_ARSENIDE
  name = G4_GALLIUM_ARSENIDE
  specific = 4
FEATURE [App::DocumentObjectGroupPython] H_element041  label="H_element : 0.081"  # scripted group (container) (typed FeaturePython)
  n = 0.08118
FEATURE [App::DocumentObjectGroupPython] C_element048  label="C_element : 0.416"  # scripted group (container) (typed FeaturePython)
  n = 0.41606
FEATURE [App::DocumentObjectGroupPython] N_element018  label="N_element : 0.111"  # scripted group (container) (typed FeaturePython)
  n = 0.11124
FEATURE [App::DocumentObjectGroupPython] O_element042  label="O_element : 0.381"  # scripted group (container) (typed FeaturePython)
  n = 0.38064
FEATURE [App::DocumentObjectGroupPython] S_element013  label="S_element : 0.011"  # scripted group (container) (typed FeaturePython)
  n = 0.01088
FEATURE [App::DocumentObjectGroupPython] G4_GEL_PHOTO_EMULSION  # scripted group (container) (typed FeaturePython)
  Dunit = g/cm3
  Dvalue = 1.2914
  Group = -> [H_element041,C_element048,N_element018,O_element042,S_element013]
  conduct = 2
  density = 1
  expand = 3
  formula = G4_GEL_PHOTO_EMULSION
  name = G4_GEL_PHOTO_EMULSION
  specific = 4
FEATURE [App::DocumentObjectGroupPython] B_element004  label="B_element : 0.040"  # scripted group (container) (typed FeaturePython)
  n = 0.0400639
FEATURE [App::DocumentObjectGroupPython] O_element043  label="O_element : 0.540"  # scripted group (container) (typed FeaturePython)
  n = 0.539561
FEATURE [App::DocumentObjectGroupPython] Na_element008  label="Na_element : 0.028"  # scripted group (container) (typed FeaturePython)
  n = 0.0281909
FEATURE [App::DocumentObjectGroupPython] Al_element003  label="Al_element : 0.012"  # scripted group (container) (typed FeaturePython)
  n = 0.011644
FEATURE [App::DocumentObjectGroupPython] Si_element003  label="Si_element : 0.377"  # scripted group (container) (typed FeaturePython)
  n = 0.377219
FEATURE [App::DocumentObjectGroupPython] K_element004  label="K_element : 0.014"  # scripted group (container) (typed FeaturePython)
  n = 0.00332099
FEATURE [App::DocumentObjectGroupPython] G4_Pyrex_Glass  # scripted group (container) (typed FeaturePython)
  Dunit = g/cm3
  Dvalue = 2.23
  Group = -> [B_element004,O_element043,Na_element008,Al_element003,Si_element003,K_element004]
  conduct = 2
  density = 1
  expand = 3
  formula = G4_Pyrex_Glass
  name = G4_Pyrex_Glass
  specific = 4
FEATURE [App::DocumentObjectGroupPython] O_element044  label="O_element : 0.156"  # scripted group (container) (typed FeaturePython)
  n = 0.156453
FEATURE [App::DocumentObjectGroupPython] Si_element004  label="Si_element : 0.081"  # scripted group (container) (typed FeaturePython)
  n = 0.080866
FEATURE [App::DocumentObjectGroupPython] Ti_element001  label="Ti_element : 0.008"  # scripted group (container) (typed FeaturePython)
  n = 0.008092
FEATURE [App::DocumentObjectGroupPython] As_element002  label="As_element : 0.003"  # scripted group (container) (typed FeaturePython)
  n = 0.002651
FEATURE [App::DocumentObjectGroupPython] Pb_element001  label="Pb_element : 0.752"  # scripted group (container) (typed FeaturePython)
  n = 0.751938
FEATURE [App::DocumentObjectGroupPython] G4_GLASS_LEAD  # scripted group (container) (typed FeaturePython)
  Dunit = g/cm3
  Dvalue = 6.22
  Group = -> [O_element044,Si_element004,Ti_element001,As_element002,Pb_element001]
  conduct = 2
  density = 1
  expand = 3
  formula = G4_GLASS_LEAD
  name = G4_GLASS_LEAD
  specific = 4
FEATURE [App::DocumentObjectGroupPython] O_element045  label="O_element : 0.460"  # scripted group (container) (typed FeaturePython)
  n = 0.4598
FEATURE [App::DocumentObjectGroupPython] Na_element009  label="Na_element : 0.096"  # scripted group (container) (typed FeaturePython)
  n = 0.0964411
FEATURE [App::DocumentObjectGroupPython] Si_element005  label="Si_element : 0.378"  # scripted group (container) (typed FeaturePython)
  n = 0.336553
FEATURE [App::DocumentObjectGroupPython] Ca_element011  label="Ca_element : 0.107"  # scripted group (container) (typed FeaturePython)
  n = 0.107205
FEATURE [App::DocumentObjectGroupPython] G4_GLASS_PLATE  # scripted group (container) (typed FeaturePython)
  Dunit = g/cm3
  Dvalue = 2.4
  Group = -> [O_element045,Na_element009,Si_element005,Ca_element011]
  conduct = 2
  density = 1
  expand = 3
  formula = G4_GLASS_PLATE
  name = G4_GLASS_PLATE
  specific = 4
FEATURE [App::DocumentObjectGroupPython] C_element049  label="C_element : 026"  # scripted group (container) (typed FeaturePython)
  n = 5
  ref = C_element
FEATURE [App::DocumentObjectGroupPython] H_element042  label="H_element : 021"  # scripted group (container) (typed FeaturePython)
  n = 10
  ref = H_element
FEATURE [App::DocumentObjectGroupPython] N_element019  label="N_element : 2"  # scripted group (container) (typed FeaturePython)
  n = 2
  ref = N_element
FEATURE [App::DocumentObjectGroupPython] O_element046  label="O_element : 022"  # scripted group (container) (typed FeaturePython)
  n = 3
  ref = O_element
FEATURE [App::DocumentObjectGroupPython] G4_GLUTAMINE  # scripted group (container) (typed FeaturePython)
  Dunit = g/cm3
  Dvalue = 1.46
  Group = -> [C_element049,H_element042,N_element019,O_element046]
  conduct = 2
  density = 1
  expand = 3
  formula = G4_GLUTAMINE
  name = G4_GLUTAMINE
  specific = 4
FEATURE [App::DocumentObjectGroupPython] C_element050  label="C_element : 027"  # scripted group (container) (typed FeaturePython)
  n = 3
  ref = C_element
FEATURE [App::DocumentObjectGroupPython] H_element043  label="H_element : 022"  # scripted group (container) (typed FeaturePython)
  n = 8
  ref = H_element
FEATURE [App::DocumentObjectGroupPython] O_element047  label="O_element : 023"  # scripted group (container) (typed FeaturePython)
  n = 3
  ref = O_element
FEATURE [App::DocumentObjectGroupPython] G4_GLYCEROL  # scripted group (container) (typed FeaturePython)
  Dunit = g/cm3
  Dvalue = 1.2613
  Group = -> [C_element050,H_element043,O_element047]
  conduct = 2
  density = 1
  expand = 3
  formula = G4_GLYCEROL
  name = G4_GLYCEROL
  specific = 4
FEATURE [App::DocumentObjectGroupPython] C_element051  label="C_element : 028"  # scripted group (container) (typed FeaturePython)
  n = 5
  ref = C_element
FEATURE [App::DocumentObjectGroupPython] H_element044  label="H_element : 023"  # scripted group (container) (typed FeaturePython)
  n = 5
  ref = H_element
FEATURE [App::DocumentObjectGroupPython] N_element020  label="N_element : 009"  # scripted group (container) (typed FeaturePython)
  n = 5
  ref = N_element
FEATURE [App::DocumentObjectGroupPython] O_element048  label="O_element : 024"  # scripted group (container) (typed FeaturePython)
  n = 1
  ref = O_element
FEATURE [App::DocumentObjectGroupPython] G4_GUANINE  # scripted group (container) (typed FeaturePython)
  Dunit = g/cm3
  Dvalue = 2.2
  Group = -> [C_element051,H_element044,N_element020,O_element048]
  conduct = 2
  density = 1
  expand = 3
  formula = G4_GUANINE
  name = G4_GUANINE
  specific = 4
FEATURE [App::DocumentObjectGroupPython] Ca_element012  label="Ca_element : 006"  # scripted group (container) (typed FeaturePython)
  n = 1
  ref = Ca_element
FEATURE [App::DocumentObjectGroupPython] S_element014  label="S_element : 005"  # scripted group (container) (typed FeaturePython)
  n = 1
  ref = S_element
FEATURE [App::DocumentObjectGroupPython] O_element049  label="O_element : 6"  # scripted group (container) (typed FeaturePython)
  n = 6
  ref = O_element
FEATURE [App::DocumentObjectGroupPython] H_element045  label="H_element : 024"  # scripted group (container) (typed FeaturePython)
  n = 4
  ref = H_element
FEATURE [App::DocumentObjectGroupPython] G4_GYPSUM  # scripted group (container) (typed FeaturePython)
  Dunit = g/cm3
  Dvalue = 2.32
  Group = -> [Ca_element012,S_element014,O_element049,H_element045]
  conduct = 2
  density = 1
  expand = 3
  formula = G4_GYPSUM
  name = G4_GYPSUM
  specific = 4
FEATURE [App::DocumentObjectGroupPython] C_element052  label="C_element : 7"  # scripted group (container) (typed FeaturePython)
  n = 7
  ref = C_element
FEATURE [App::DocumentObjectGroupPython] H_element046  label="H_element : 16"  # scripted group (container) (typed FeaturePython)
  n = 16
  ref = H_element
FEATURE [App::DocumentObjectGroupPython] G4_N_HEPTANE  label="G4_N-HEPTANE"  # scripted group (container) (typed FeaturePython)
  Dunit = g/cm3
  Dvalue = 0.68376
  Group = -> [C_element052,H_element046]
  conduct = 2
  density = 1
  expand = 3
  formula = G4_N-HEPTANE
  name = G4_N-HEPTANE
  specific = 4
FEATURE [App::DocumentObjectGroupPython] C_element053  label="C_element : 029"  # scripted group (container) (typed FeaturePython)
  n = 6
  ref = C_element
FEATURE [App::DocumentObjectGroupPython] H_element047  label="H_element : 14"  # scripted group (container) (typed FeaturePython)
  n = 14
  ref = H_element
FEATURE [App::DocumentObjectGroupPython] G4_N_HEXANE  label="G4_N-HEXANE"  # scripted group (container) (typed FeaturePython)
  Dunit = g/cm3
  Dvalue = 0.6603
  Group = -> [C_element053,H_element047]
  conduct = 2
  density = 1
  expand = 3
  formula = G4_N-HEXANE
  name = G4_N-HEXANE
  specific = 4
FEATURE [App::DocumentObjectGroupPython] C_element054  label="C_element : 22"  # scripted group (container) (typed FeaturePython)
  n = 22
  ref = C_element
FEATURE [App::DocumentObjectGroupPython] H_element048  label="H_element : 025"  # scripted group (container) (typed FeaturePython)
  n = 10
  ref = H_element
FEATURE [App::DocumentObjectGroupPython] N_element021  label="N_element : 010"  # scripted group (container) (typed FeaturePython)
  n = 2
  ref = N_element
FEATURE [App::DocumentObjectGroupPython] O_element050  label="O_element : 025"  # scripted group (container) (typed FeaturePython)
  n = 5
  ref = O_element
FEATURE [App::DocumentObjectGroupPython] G4_KAPTON  # scripted group (container) (typed FeaturePython)
  Dunit = g/cm3
  Dvalue = 1.42
  Group = -> [C_element054,H_element048,N_element021,O_element050]
  conduct = 2
  density = 1
  expand = 3
  formula = G4_KAPTON
  name = G4_KAPTON
  specific = 4
FEATURE [App::DocumentObjectGroupPython] La_element001  label="La_element : 1"  # scripted group (container) (typed FeaturePython)
  n = 1
  ref = La_element
FEATURE [App::DocumentObjectGroupPython] Br_element003  label="Br_element : 002"  # scripted group (container) (typed FeaturePython)
  n = 1
  ref = Br_element
FEATURE [App::DocumentObjectGroupPython] O_element051  label="O_element : 026"  # scripted group (container) (typed FeaturePython)
  n = 1
  ref = O_element
FEATURE [App::DocumentObjectGroupPython] G4_LANTHANUM_OXYBROMIDE  # scripted group (container) (typed FeaturePython)
  Dunit = g/cm3
  Dvalue = 6.28
  Group = -> [La_element001,Br_element003,O_element051]
  conduct = 2
  density = 1
  expand = 3
  formula = G4_LANTHANUM_OXYBROMIDE
  name = G4_LANTHANUM_OXYBROMIDE
  specific = 4
FEATURE [App::DocumentObjectGroupPython] La_element002  label="La_element : 2"  # scripted group (container) (typed FeaturePython)
  n = 2
  ref = La_element
FEATURE [App::DocumentObjectGroupPython] O_element052  label="O_element : 027"  # scripted group (container) (typed FeaturePython)
  n = 2
  ref = O_element
FEATURE [App::DocumentObjectGroupPython] S_element015  label="S_element : 006"  # scripted group (container) (typed FeaturePython)
  n = 1
  ref = S_element
FEATURE [App::DocumentObjectGroupPython] G4_LANTHANUM_OXYSULFIDE  # scripted group (container) (typed FeaturePython)
  Dunit = g/cm3
  Dvalue = 5.86
  Group = -> [La_element002,O_element052,S_element015]
  conduct = 2
  density = 1
  expand = 3
  formula = G4_LANTHANUM_OXYSULFIDE
  name = G4_LANTHANUM_OXYSULFIDE
  specific = 4
FEATURE [App::DocumentObjectGroupPython] O_element053  label="O_element : 0.072"  # scripted group (container) (typed FeaturePython)
  n = 0.071682
FEATURE [App::DocumentObjectGroupPython] Pb_element002  label="Pb_element : 0.928"  # scripted group (container) (typed FeaturePython)
  n = 0.928318
FEATURE [App::DocumentObjectGroupPython] G4_LEAD_OXIDE  # scripted group (container) (typed FeaturePython)
  Dunit = g/cm3
  Dvalue = 9.53
  Group = -> [O_element053,Pb_element002]
  conduct = 2
  density = 1
  expand = 3
  formula = G4_LEAD_OXIDE
  name = G4_LEAD_OXIDE
  specific = 4
FEATURE [App::DocumentObjectGroupPython] Li_element001  label="Li_element : 1"  # scripted group (container) (typed FeaturePython)
  n = 1
  ref = Li_element
FEATURE [App::DocumentObjectGroupPython] N_element022  label="N_element : 011"  # scripted group (container) (typed FeaturePython)
  n = 1
  ref = N_element
FEATURE [App::DocumentObjectGroupPython] H_element049  label="H_element : 026"  # scripted group (container) (typed FeaturePython)
  n = 2
  ref = H_element
FEATURE [App::DocumentObjectGroupPython] G4_LITHIUM_AMIDE  # scripted group (container) (typed FeaturePython)
  Dunit = g/cm3
  Dvalue = 1.178
  Group = -> [Li_element001,N_element022,H_element049]
  conduct = 2
  density = 1
  expand = 3
  formula = G4_LITHIUM_AMIDE
  name = G4_LITHIUM_AMIDE
  specific = 4
FEATURE [App::DocumentObjectGroupPython] Li_element002  label="Li_element : 2"  # scripted group (container) (typed FeaturePython)
  n = 2
  ref = Li_element
FEATURE [App::DocumentObjectGroupPython] C_element055  label="C_element : 030"  # scripted group (container) (typed FeaturePython)
  n = 1
  ref = C_element
FEATURE [App::DocumentObjectGroupPython] O_element054  label="O_element : 028"  # scripted group (container) (typed FeaturePython)
  n = 3
  ref = O_element
FEATURE [App::DocumentObjectGroupPython] G4_LITHIUM_CARBONATE  # scripted group (container) (typed FeaturePython)
  Dunit = g/cm3
  Dvalue = 2.11
  Group = -> [Li_element002,C_element055,O_element054]
  conduct = 2
  density = 1
  expand = 3
  formula = G4_LITHIUM_CARBONATE
  name = G4_LITHIUM_CARBONATE
  specific = 4
FEATURE [App::DocumentObjectGroupPython] Li_element003  label="Li_element : 003"  # scripted group (container) (typed FeaturePython)
  n = 1
  ref = Li_element
FEATURE [App::DocumentObjectGroupPython] F_element012  label="F_element : 004"  # scripted group (container) (typed FeaturePython)
  n = 1
  ref = F_element
FEATURE [App::DocumentObjectGroupPython] G4_LITHIUM_FLUORIDE  # scripted group (container) (typed FeaturePython)
  Dunit = g/cm3
  Dvalue = 2.635
  Group = -> [Li_element003,F_element012]
  conduct = 2
  density = 1
  expand = 3
  formula = G4_LITHIUM_FLUORIDE
  name = G4_LITHIUM_FLUORIDE
  specific = 4
FEATURE [App::DocumentObjectGroupPython] Li_element004  label="Li_element : 004"  # scripted group (container) (typed FeaturePython)
  n = 1
  ref = Li_element
FEATURE [App::DocumentObjectGroupPython] H_element050  label="H_element : 027"  # scripted group (container) (typed FeaturePython)
  n = 1
  ref = H_element
FEATURE [App::DocumentObjectGroupPython] G4_LITHIUM_HYDRIDE  # scripted group (container) (typed FeaturePython)
  Dunit = g/cm3
  Dvalue = 0.82
  Group = -> [Li_element004,H_element050]
  conduct = 2
  density = 1
  expand = 3
  formula = G4_LITHIUM_HYDRIDE
  name = G4_LITHIUM_HYDRIDE
  specific = 4
FEATURE [App::DocumentObjectGroupPython] Li_element005  label="Li_element : 005"  # scripted group (container) (typed FeaturePython)
  n = 1
  ref = Li_element
FEATURE [App::DocumentObjectGroupPython] I_element003  label="I_element : 002"  # scripted group (container) (typed FeaturePython)
  n = 1
  ref = I_element
FEATURE [App::DocumentObjectGroupPython] G4_LITHIUM_IODIDE  # scripted group (container) (typed FeaturePython)
  Dunit = g/cm3
  Dvalue = 3.494
  Group = -> [Li_element005,I_element003]
  conduct = 2
  density = 1
  expand = 3
  formula = G4_LITHIUM_IODIDE
  name = G4_LITHIUM_IODIDE
  specific = 4
FEATURE [App::DocumentObjectGroupPython] Li_element006  label="Li_element : 006"  # scripted group (container) (typed FeaturePython)
  n = 2
  ref = Li_element
FEATURE [App::DocumentObjectGroupPython] O_element055  label="O_element : 029"  # scripted group (container) (typed FeaturePython)
  n = 1
  ref = O_element
FEATURE [App::DocumentObjectGroupPython] G4_LITHIUM_OXIDE  # scripted group (container) (typed FeaturePython)
  Dunit = g/cm3
  Dvalue = 2.013
  Group = -> [Li_element006,O_element055]
  conduct = 2
  density = 1
  expand = 3
  formula = G4_LITHIUM_OXIDE
  name = G4_LITHIUM_OXIDE
  specific = 4
FEATURE [App::DocumentObjectGroupPython] Li_element007  label="Li_element : 007"  # scripted group (container) (typed FeaturePython)
  n = 2
  ref = Li_element
FEATURE [App::DocumentObjectGroupPython] B_element005  label="B_element : 005"  # scripted group (container) (typed FeaturePython)
  n = 4
  ref = B_element
FEATURE [App::DocumentObjectGroupPython] O_element056  label="O_element : 7"  # scripted group (container) (typed FeaturePython)
  n = 7
  ref = O_element
FEATURE [App::DocumentObjectGroupPython] G4_LITHIUM_TETRABORATE  # scripted group (container) (typed FeaturePython)
  Dunit = g/cm3
  Dvalue = 2.44
  Group = -> [Li_element007,B_element005,O_element056]
  conduct = 2
  density = 1
  expand = 3
  formula = G4_LITHIUM_TETRABORATE
  name = G4_LITHIUM_TETRABORATE
  specific = 4
FEATURE [App::DocumentObjectGroupPython] H_element051  label="H_element : 0.105"  # scripted group (container) (typed FeaturePython)
  n = 0.105
FEATURE [App::DocumentObjectGroupPython] C_element056  label="C_element : 0.083"  # scripted group (container) (typed FeaturePython)
  n = 0.083
FEATURE [App::DocumentObjectGroupPython] N_element023  label="N_element : 0.023"  # scripted group (container) (typed FeaturePython)
  n = 0.023
FEATURE [App::DocumentObjectGroupPython] O_element057  label="O_element : 0.779"  # scripted group (container) (typed FeaturePython)
  n = 0.779
FEATURE [App::DocumentObjectGroupPython] Na_element010  label="Na_element : 0.097"  # scripted group (container) (typed FeaturePython)
  n = 0.002
FEATURE [App::DocumentObjectGroupPython] P_element006  label="P_element : 0.105"  # scripted group (container) (typed FeaturePython)
  n = 0.001
FEATURE [App::DocumentObjectGroupPython] S_element016  label="S_element : 0.017"  # scripted group (container) (typed FeaturePython)
  n = 0.002
FEATURE [App::DocumentObjectGroupPython] Cl_element014  label="Cl_element : 0.587"  # scripted group (container) (typed FeaturePython)
  n = 0.003
FEATURE [App::DocumentObjectGroupPython] K_element005  label="K_element : 0.015"  # scripted group (container) (typed FeaturePython)
  n = 0.002
FEATURE [App::DocumentObjectGroupPython] G4_LUNG_ICRP  # scripted group (container) (typed FeaturePython)
  Dunit = g/cm3
  Dvalue = 1.04
  Group = -> [H_element051,C_element056,N_element023,O_element057,Na_element010,P_element006,S_element016,Cl_element014,K_element005]
  conduct = 2
  density = 1
  expand = 3
  formula = G4_LUNG_ICRP
  name = G4_LUNG_ICRP
  specific = 4
FEATURE [App::DocumentObjectGroupPython] H_element052  label="H_element : 0.116"  # scripted group (container) (typed FeaturePython)
  n = 0.114318
FEATURE [App::DocumentObjectGroupPython] C_element057  label="C_element : 0.656"  # scripted group (container) (typed FeaturePython)
  n = 0.655824
FEATURE [App::DocumentObjectGroupPython] O_element058  label="O_element : 0.092"  # scripted group (container) (typed FeaturePython)
  n = 0.0921831
FEATURE [App::DocumentObjectGroupPython] Mg_element004  label="Mg_element : 0.135"  # scripted group (container) (typed FeaturePython)
  n = 0.134792
FEATURE [App::DocumentObjectGroupPython] Ca_element013  label="Ca_element : 0.003"  # scripted group (container) (typed FeaturePython)
  n = 0.002883
FEATURE [App::DocumentObjectGroupPython] G4_M3_WAX  # scripted group (container) (typed FeaturePython)
  Dunit = g/cm3
  Dvalue = 1.05
  Group = -> [H_element052,C_element057,O_element058,Mg_element004,Ca_element013]
  conduct = 2
  density = 1
  expand = 3
  formula = G4_M3_WAX
  name = G4_M3_WAX
  specific = 4
FEATURE [App::DocumentObjectGroupPython] Mg_element005  label="Mg_element : 1"  # scripted group (container) (typed FeaturePython)
  n = 1
  ref = Mg_element
FEATURE [App::DocumentObjectGroupPython] C_element058  label="C_element : 031"  # scripted group (container) (typed FeaturePython)
  n = 1
  ref = C_element
FEATURE [App::DocumentObjectGroupPython] O_element059  label="O_element : 030"  # scripted group (container) (typed FeaturePython)
  n = 3
  ref = O_element
FEATURE [App::DocumentObjectGroupPython] G4_MAGNESIUM_CARBONATE  # scripted group (container) (typed FeaturePython)
  Dunit = g/cm3
  Dvalue = 2.958
  Group = -> [Mg_element005,C_element058,O_element059]
  conduct = 2
  density = 1
  expand = 3
  formula = G4_MAGNESIUM_CARBONATE
  name = G4_MAGNESIUM_CARBONATE
  specific = 4
FEATURE [App::DocumentObjectGroupPython] Mg_element006  label="Mg_element : 002"  # scripted group (container) (typed FeaturePython)
  n = 1
  ref = Mg_element
FEATURE [App::DocumentObjectGroupPython] F_element013  label="F_element : 005"  # scripted group (container) (typed FeaturePython)
  n = 2
  ref = F_element
FEATURE [App::DocumentObjectGroupPython] G4_MAGNESIUM_FLUORIDE  # scripted group (container) (typed FeaturePython)
  Dunit = g/cm3
  Dvalue = 3
  Group = -> [Mg_element006,F_element013]
  conduct = 2
  density = 1
  expand = 3
  formula = G4_MAGNESIUM_FLUORIDE
  name = G4_MAGNESIUM_FLUORIDE
  specific = 4
FEATURE [App::DocumentObjectGroupPython] Mg_element007  label="Mg_element : 003"  # scripted group (container) (typed FeaturePython)
  n = 1
  ref = Mg_element
FEATURE [App::DocumentObjectGroupPython] O_element060  label="O_element : 031"  # scripted group (container) (typed FeaturePython)
  n = 1
  ref = O_element
FEATURE [App::DocumentObjectGroupPython] G4_MAGNESIUM_OXIDE  # scripted group (container) (typed FeaturePython)
  Dunit = g/cm3
  Dvalue = 3.58
  Group = -> [Mg_element007,O_element060]
  conduct = 2
  density = 1
  expand = 3
  formula = G4_MAGNESIUM_OXIDE
  name = G4_MAGNESIUM_OXIDE
  specific = 4
FEATURE [App::DocumentObjectGroupPython] Mg_element008  label="Mg_element : 004"  # scripted group (container) (typed FeaturePython)
  n = 1
  ref = Mg_element
FEATURE [App::DocumentObjectGroupPython] B_element006  label="B_element : 006"  # scripted group (container) (typed FeaturePython)
  n = 4
  ref = B_element
FEATURE [App::DocumentObjectGroupPython] O_element061  label="O_element : 032"  # scripted group (container) (typed FeaturePython)
  n = 7
  ref = O_element
FEATURE [App::DocumentObjectGroupPython] G4_MAGNESIUM_TETRABORATE  # scripted group (container) (typed FeaturePython)
  Dunit = g/cm3
  Dvalue = 2.53
  Group = -> [Mg_element008,B_element006,O_element061]
  conduct = 2
  density = 1
  expand = 3
  formula = G4_MAGNESIUM_TETRABORATE
  name = G4_MAGNESIUM_TETRABORATE
  specific = 4
FEATURE [App::DocumentObjectGroupPython] Hg_element001  label="Hg_element : 1"  # scripted group (container) (typed FeaturePython)
  n = 1
  ref = Hg_element
FEATURE [App::DocumentObjectGroupPython] I_element004  label="I_element : 2"  # scripted group (container) (typed FeaturePython)
  n = 2
  ref = I_element
FEATURE [App::DocumentObjectGroupPython] G4_MERCURIC_IODIDE  # scripted group (container) (typed FeaturePython)
  Dunit = g/cm3
  Dvalue = 6.36
  Group = -> [Hg_element001,I_element004]
  conduct = 2
  density = 1
  expand = 3
  formula = G4_MERCURIC_IODIDE
  name = G4_MERCURIC_IODIDE
  specific = 4
FEATURE [App::DocumentObjectGroupPython] C_element059  label="C_element : 032"  # scripted group (container) (typed FeaturePython)
  n = 1
  ref = C_element
FEATURE [App::DocumentObjectGroupPython] H_element053  label="H_element : 028"  # scripted group (container) (typed FeaturePython)
  n = 4
  ref = H_element
FEATURE [App::DocumentObjectGroupPython] G4_METHANE  # scripted group (container) (typed FeaturePython)
  Dunit = g/cm3
  Dvalue = 0.000667151
  Group = -> [C_element059,H_element053]
  conduct = 2
  density = 1
  expand = 3
  formula = G4_METHANE
  name = G4_METHANE
  specific = 4
FEATURE [App::DocumentObjectGroupPython] C_element060  label="C_element : 033"  # scripted group (container) (typed FeaturePython)
  n = 1
  ref = C_element
FEATURE [App::DocumentObjectGroupPython] H_element054  label="H_element : 029"  # scripted group (container) (typed FeaturePython)
  n = 4
  ref = H_element
FEATURE [App::DocumentObjectGroupPython] O_element062  label="O_element : 033"  # scripted group (container) (typed FeaturePython)
  n = 1
  ref = O_element
FEATURE [App::DocumentObjectGroupPython] G4_METHANOL  # scripted group (container) (typed FeaturePython)
  Dunit = g/cm3
  Dvalue = 0.7914
  Group = -> [C_element060,H_element054,O_element062]
  conduct = 2
  density = 1
  expand = 3
  formula = G4_METHANOL
  name = G4_METHANOL
  specific = 4
FEATURE [App::DocumentObjectGroupPython] H_element055  label="H_element : 0.134"  # scripted group (container) (typed FeaturePython)
  n = 0.13404
FEATURE [App::DocumentObjectGroupPython] C_element061  label="C_element : 0.778"  # scripted group (container) (typed FeaturePython)
  n = 0.77796
FEATURE [App::DocumentObjectGroupPython] O_element063  label="O_element : 0.035"  # scripted group (container) (typed FeaturePython)
  n = 0.03502
FEATURE [App::DocumentObjectGroupPython] Mg_element009  label="Mg_element : 0.039"  # scripted group (container) (typed FeaturePython)
  n = 0.038594
FEATURE [App::DocumentObjectGroupPython] Ti_element002  label="Ti_element : 0.014"  # scripted group (container) (typed FeaturePython)
  n = 0.014386
FEATURE [App::DocumentObjectGroupPython] G4_MIX_D_WAX  # scripted group (container) (typed FeaturePython)
  Dunit = g/cm3
  Dvalue = 0.99
  Group = -> [H_element055,C_element061,O_element063,Mg_element009,Ti_element002]
  conduct = 2
  density = 1
  expand = 3
  formula = G4_MIX_D_WAX
  name = G4_MIX_D_WAX
  specific = 4
FEATURE [App::DocumentObjectGroupPython] H_element056  label="H_element : 0.135"  # scripted group (container) (typed FeaturePython)
  n = 0.081192
FEATURE [App::DocumentObjectGroupPython] C_element062  label="C_element : 0.583"  # scripted group (container) (typed FeaturePython)
  n = 0.583442
FEATURE [App::DocumentObjectGroupPython] N_element024  label="N_element : 0.018"  # scripted group (container) (typed FeaturePython)
  n = 0.017798
FEATURE [App::DocumentObjectGroupPython] O_element064  label="O_element : 0.186"  # scripted group (container) (typed FeaturePython)
  n = 0.186381
FEATURE [App::DocumentObjectGroupPython] Mg_element010  label="Mg_element : 0.130"  # scripted group (container) (typed FeaturePython)
  n = 0.130287
FEATURE [App::DocumentObjectGroupPython] Cl_element015  label="Cl_element : 0.588"  # scripted group (container) (typed FeaturePython)
  n = 0.0009
FEATURE [App::DocumentObjectGroupPython] G4_MS20_TISSUE  # scripted group (container) (typed FeaturePython)
  Dunit = g/cm3
  Dvalue = 1
  Group = -> [H_element056,C_element062,N_element024,O_element064,Mg_element010,Cl_element015]
  conduct = 2
  density = 1
  expand = 3
  formula = G4_MS20_TISSUE
  name = G4_MS20_TISSUE
  specific = 4
FEATURE [App::DocumentObjectGroupPython] H_element057  label="H_element : 0.136"  # scripted group (container) (typed FeaturePython)
  n = 0.102
FEATURE [App::DocumentObjectGroupPython] C_element063  label="C_element : 0.143"  # scripted group (container) (typed FeaturePython)
  n = 0.143
FEATURE [App::DocumentObjectGroupPython] N_element025  label="N_element : 0.034"  # scripted group (container) (typed FeaturePython)
  n = 0.034
FEATURE [App::DocumentObjectGroupPython] O_element065  label="O_element : 0.710"  # scripted group (container) (typed FeaturePython)
  n = 0.71
FEATURE [App::DocumentObjectGroupPython] Na_element011  label="Na_element : 0.098"  # scripted group (container) (typed FeaturePython)
  n = 0.001
FEATURE [App::DocumentObjectGroupPython] P_element007  label="P_element : 0.002"  # scripted group (container) (typed FeaturePython)
  n = 0.002
FEATURE [App::DocumentObjectGroupPython] S_element017  label="S_element : 0.018"  # scripted group (container) (typed FeaturePython)
  n = 0.003
FEATURE [App::DocumentObjectGroupPython] Cl_element016  label="Cl_element : 0.589"  # scripted group (container) (typed FeaturePython)
  n = 0.001
FEATURE [App::DocumentObjectGroupPython] K_element006  label="K_element : 0.004"  # scripted group (container) (typed FeaturePython)
  n = 0.004
FEATURE [App::DocumentObjectGroupPython] G4_MUSCLE_SKELETAL_ICRP  # scripted group (container) (typed FeaturePython)
  Dunit = g/cm3
  Dvalue = 1.05
  Group = -> [H_element057,C_element063,N_element025,O_element065,Na_element011,P_element007,S_element017,Cl_element016,K_element006]
  conduct = 2
  density = 1
  expand = 3
  formula = G4_MUSCLE_SKELETAL_ICRP
  name = G4_MUSCLE_SKELETAL_ICRP
  specific = 4
FEATURE [App::DocumentObjectGroupPython] H_element058  label="H_element : 0.137"  # scripted group (container) (typed FeaturePython)
  n = 0.102102
FEATURE [App::DocumentObjectGroupPython] C_element064  label="C_element : 0.123"  # scripted group (container) (typed FeaturePython)
  n = 0.123123
FEATURE [App::DocumentObjectGroupPython] N_element026  label="N_element : 0.756"  # scripted group (container) (typed FeaturePython)
  n = 0.035035
FEATURE [App::DocumentObjectGroupPython] O_element066  label="O_element : 0.730"  # scripted group (container) (typed FeaturePython)
  n = 0.72973
FEATURE [App::DocumentObjectGroupPython] Na_element012  label="Na_element : 0.099"  # scripted group (container) (typed FeaturePython)
  n = 0.001001
FEATURE [App::DocumentObjectGroupPython] P_element008  label="P_element : 0.106"  # scripted group (container) (typed FeaturePython)
  n = 0.002002
FEATURE [App::DocumentObjectGroupPython] S_element018  label="S_element : 0.019"  # scripted group (container) (typed FeaturePython)
  n = 0.004004
FEATURE [App::DocumentObjectGroupPython] K_element007  label="K_element : 0.016"  # scripted group (container) (typed FeaturePython)
  n = 0.003003
FEATURE [App::DocumentObjectGroupPython] G4_MUSCLE_STRIATED_ICRU  # scripted group (container) (typed FeaturePython)
  Dunit = g/cm3
  Dvalue = 1.04
  Group = -> [H_element058,C_element064,N_element026,O_element066,Na_element012,P_element008,S_element018,K_element007]
  conduct = 2
  density = 1
  expand = 3
  formula = G4_MUSCLE_STRIATED_ICRU
  name = G4_MUSCLE_STRIATED_ICRU
  specific = 4
FEATURE [App::DocumentObjectGroupPython] H_element059  label="H_element : 0.098"  # scripted group (container) (typed FeaturePython)
  n = 0.0982341
FEATURE [App::DocumentObjectGroupPython] C_element065  label="C_element : 0.156"  # scripted group (container) (typed FeaturePython)
  n = 0.156214
FEATURE [App::DocumentObjectGroupPython] N_element027  label="N_element : 0.757"  # scripted group (container) (typed FeaturePython)
  n = 0.035451
FEATURE [App::DocumentObjectGroupPython] O_element067  label="O_element : 0.880"  # scripted group (container) (typed FeaturePython)
  n = 0.710101
FEATURE [App::DocumentObjectGroupPython] G4_MUSCLE_WITH_SUCROSE  # scripted group (container) (typed FeaturePython)
  Dunit = g/cm3
  Dvalue = 1.11
  Group = -> [H_element059,C_element065,N_element027,O_element067]
  conduct = 2
  density = 1
  expand = 3
  formula = G4_MUSCLE_WITH_SUCROSE
  name = G4_MUSCLE_WITH_SUCROSE
  specific = 4
FEATURE [App::DocumentObjectGroupPython] H_element060  label="H_element : 0.138"  # scripted group (container) (typed FeaturePython)
  n = 0.101969
FEATURE [App::DocumentObjectGroupPython] C_element066  label="C_element : 0.120"  # scripted group (container) (typed FeaturePython)
  n = 0.120058
FEATURE [App::DocumentObjectGroupPython] N_element028  label="N_element : 0.758"  # scripted group (container) (typed FeaturePython)
  n = 0.035451
FEATURE [App::DocumentObjectGroupPython] O_element068  label="O_element : 0.743"  # scripted group (container) (typed FeaturePython)
  n = 0.742522
FEATURE [App::DocumentObjectGroupPython] G4_MUSCLE_WITHOUT_SUCROSE  # scripted group (container) (typed FeaturePython)
  Dunit = g/cm3
  Dvalue = 1.07
  Group = -> [H_element060,C_element066,N_element028,O_element068]
  conduct = 2
  density = 1
  expand = 3
  formula = G4_MUSCLE_WITHOUT_SUCROSE
  name = G4_MUSCLE_WITHOUT_SUCROSE
  specific = 4
FEATURE [App::DocumentObjectGroupPython] C_element067  label="C_element : 10"  # scripted group (container) (typed FeaturePython)
  n = 10
  ref = C_element
FEATURE [App::DocumentObjectGroupPython] H_element061  label="H_element : 030"  # scripted group (container) (typed FeaturePython)
  n = 8
  ref = H_element
FEATURE [App::DocumentObjectGroupPython] G4_NAPHTHALENE  # scripted group (container) (typed FeaturePython)
  Dunit = g/cm3
  Dvalue = 1.145
  Group = -> [C_element067,H_element061]
  conduct = 2
  density = 1
  expand = 3
  formula = G4_NAPHTHALENE
  name = G4_NAPHTHALENE
  specific = 4
FEATURE [App::DocumentObjectGroupPython] C_element068  label="C_element : 034"  # scripted group (container) (typed FeaturePython)
  n = 6
  ref = C_element
FEATURE [App::DocumentObjectGroupPython] H_element062  label="H_element : 031"  # scripted group (container) (typed FeaturePython)
  n = 5
  ref = H_element
FEATURE [App::DocumentObjectGroupPython] N_element029  label="N_element : 012"  # scripted group (container) (typed FeaturePython)
  n = 1
  ref = N_element
FEATURE [App::DocumentObjectGroupPython] O_element069  label="O_element : 034"  # scripted group (container) (typed FeaturePython)
  n = 2
  ref = O_element
FEATURE [App::DocumentObjectGroupPython] G4_NITROBENZENE  # scripted group (container) (typed FeaturePython)
  Dunit = g/cm3
  Dvalue = 1.19867
  Group = -> [C_element068,H_element062,N_element029,O_element069]
  conduct = 2
  density = 1
  expand = 3
  formula = G4_NITROBENZENE
  name = G4_NITROBENZENE
  specific = 4
FEATURE [App::DocumentObjectGroupPython] N_element030  label="N_element : 013"  # scripted group (container) (typed FeaturePython)
  n = 2
  ref = N_element
FEATURE [App::DocumentObjectGroupPython] O_element070  label="O_element : 035"  # scripted group (container) (typed FeaturePython)
  n = 1
  ref = O_element
FEATURE [App::DocumentObjectGroupPython] G4_NITROUS_OXIDE  # scripted group (container) (typed FeaturePython)
  Dunit = g/cm3
  Dvalue = 0.00183094
  Group = -> [N_element030,O_element070]
  conduct = 2
  density = 1
  expand = 3
  formula = G4_NITROUS_OXIDE
  name = G4_NITROUS_OXIDE
  specific = 4
FEATURE [App::DocumentObjectGroupPython] H_element063  label="H_element : 0.104"  # scripted group (container) (typed FeaturePython)
  n = 0.103509
FEATURE [App::DocumentObjectGroupPython] C_element069  label="C_element : 0.648"  # scripted group (container) (typed FeaturePython)
  n = 0.648416
FEATURE [App::DocumentObjectGroupPython] N_element031  label="N_element : 0.100"  # scripted group (container) (typed FeaturePython)
  n = 0.0995361
FEATURE [App::DocumentObjectGroupPython] O_element071  label="O_element : 0.149"  # scripted group (container) (typed FeaturePython)
  n = 0.148539
FEATURE [App::DocumentObjectGroupPython] G4_NYLON_8062  label="G4_NYLON-8062"  # scripted group (container) (typed FeaturePython)
  Dunit = g/cm3
  Dvalue = 1.08
  Group = -> [H_element063,C_element069,N_element031,O_element071]
  conduct = 2
  density = 1
  expand = 3
  formula = G4_NYLON-8062
  name = G4_NYLON-8062
  specific = 4
FEATURE [App::DocumentObjectGroupPython] C_element070  label="C_element : 035"  # scripted group (container) (typed FeaturePython)
  n = 6
  ref = C_element
FEATURE [App::DocumentObjectGroupPython] H_element064  label="H_element : 11"  # scripted group (container) (typed FeaturePython)
  n = 11
  ref = H_element
FEATURE [App::DocumentObjectGroupPython] N_element032  label="N_element : 014"  # scripted group (container) (typed FeaturePython)
  n = 1
  ref = N_element
FEATURE [App::DocumentObjectGroupPython] O_element072  label="O_element : 036"  # scripted group (container) (typed FeaturePython)
  n = 1
  ref = O_element
FEATURE [App::DocumentObjectGroupPython] G4_NYLON_6_6  label="G4_NYLON-6-6"  # scripted group (container) (typed FeaturePython)
  Dunit = g/cm3
  Dvalue = 1.14
  Group = -> [C_element070,H_element064,N_element032,O_element072]
  conduct = 2
  density = 1
  expand = 3
  formula = G4_NYLON-6-6
  name = G4_NYLON-6-6
  specific = 4
FEATURE [App::DocumentObjectGroupPython] H_element065  label="H_element : 0.139"  # scripted group (container) (typed FeaturePython)
  n = 0.107062
FEATURE [App::DocumentObjectGroupPython] C_element071  label="C_element : 0.680"  # scripted group (container) (typed FeaturePython)
  n = 0.680449
FEATURE [App::DocumentObjectGroupPython] N_element033  label="N_element : 0.099"  # scripted group (container) (typed FeaturePython)
  n = 0.099189
FEATURE [App::DocumentObjectGroupPython] O_element073  label="O_element : 0.113"  # scripted group (container) (typed FeaturePython)
  n = 0.1133
FEATURE [App::DocumentObjectGroupPython] G4_NYLON_6_10  label="G4_NYLON-6-10"  # scripted group (container) (typed FeaturePython)
  Dunit = g/cm3
  Dvalue = 1.14
  Group = -> [H_element065,C_element071,N_element033,O_element073]
  conduct = 2
  density = 1
  expand = 3
  formula = G4_NYLON-6-10
  name = G4_NYLON-6-10
  specific = 4
FEATURE [App::DocumentObjectGroupPython] H_element066  label="H_element : 0.140"  # scripted group (container) (typed FeaturePython)
  n = 0.115476
FEATURE [App::DocumentObjectGroupPython] C_element072  label="C_element : 0.721"  # scripted group (container) (typed FeaturePython)
  n = 0.720818
FEATURE [App::DocumentObjectGroupPython] N_element034  label="N_element : 0.076"  # scripted group (container) (typed FeaturePython)
  n = 0.0764169
FEATURE [App::DocumentObjectGroupPython] O_element074  label="O_element : 0.087"  # scripted group (container) (typed FeaturePython)
  n = 0.0872889
FEATURE [App::DocumentObjectGroupPython] G4_NYLON_11_RILSAN  label="G4_NYLON-11_RILSAN"  # scripted group (container) (typed FeaturePython)
  Dunit = g/cm3
  Dvalue = 1.425
  Group = -> [H_element066,C_element072,N_element034,O_element074]
  conduct = 2
  density = 1
  expand = 3
  formula = G4_NYLON-11_RILSAN
  name = G4_NYLON-11_RILSAN
  specific = 4
FEATURE [App::DocumentObjectGroupPython] C_element073  label="C_element : 8"  # scripted group (container) (typed FeaturePython)
  n = 8
  ref = C_element
FEATURE [App::DocumentObjectGroupPython] H_element067  label="H_element : 18"  # scripted group (container) (typed FeaturePython)
  n = 18
  ref = H_element
FEATURE [App::DocumentObjectGroupPython] G4_OCTANE  # scripted group (container) (typed FeaturePython)
  Dunit = g/cm3
  Dvalue = 0.7026
  Group = -> [C_element073,H_element067]
  conduct = 2
  density = 1
  expand = 3
  formula = G4_OCTANE
  name = G4_OCTANE
  specific = 4
FEATURE [App::DocumentObjectGroupPython] C_element074  label="C_element : 25"  # scripted group (container) (typed FeaturePython)
  n = 25
  ref = C_element
FEATURE [App::DocumentObjectGroupPython] H_element068  label="H_element : 52"  # scripted group (container) (typed FeaturePython)
  n = 52
  ref = H_element
FEATURE [App::DocumentObjectGroupPython] G4_PARAFFIN  # scripted group (container) (typed FeaturePython)
  Dunit = g/cm3
  Dvalue = 0.93
  Group = -> [C_element074,H_element068]
  conduct = 2
  density = 1
  expand = 3
  formula = G4_PARAFFIN
  name = G4_PARAFFIN
  specific = 4
FEATURE [App::DocumentObjectGroupPython] C_element075  label="C_element : 036"  # scripted group (container) (typed FeaturePython)
  n = 5
  ref = C_element
FEATURE [App::DocumentObjectGroupPython] H_element069  label="H_element : 032"  # scripted group (container) (typed FeaturePython)
  n = 12
  ref = H_element
FEATURE [App::DocumentObjectGroupPython] G4_N_PENTANE  label="G4_N-PENTANE"  # scripted group (container) (typed FeaturePython)
  Dunit = g/cm3
  Dvalue = 0.6262
  Group = -> [C_element075,H_element069]
  conduct = 2
  density = 1
  expand = 3
  formula = G4_N-PENTANE
  name = G4_N-PENTANE
  specific = 4
FEATURE [App::DocumentObjectGroupPython] H_element070  label="H_element : 0.014"  # scripted group (container) (typed FeaturePython)
  n = 0.0141
FEATURE [App::DocumentObjectGroupPython] C_element076  label="C_element : 0.072"  # scripted group (container) (typed FeaturePython)
  n = 0.072261
FEATURE [App::DocumentObjectGroupPython] N_element035  label="N_element : 0.019"  # scripted group (container) (typed FeaturePython)
  n = 0.01932
FEATURE [App::DocumentObjectGroupPython] O_element075  label="O_element : 0.066"  # scripted group (container) (typed FeaturePython)
  n = 0.066101
FEATURE [App::DocumentObjectGroupPython] S_element019  label="S_element : 0.020"  # scripted group (container) (typed FeaturePython)
  n = 0.00189
FEATURE [App::DocumentObjectGroupPython] Br_element004  label="Br_element : 0.349"  # scripted group (container) (typed FeaturePython)
  n = 0.349103
FEATURE [App::DocumentObjectGroupPython] Ag_element001  label="Ag_element : 0.474"  # scripted group (container) (typed FeaturePython)
  n = 0.474105
FEATURE [App::DocumentObjectGroupPython] I_element005  label="I_element : 0.003"  # scripted group (container) (typed FeaturePython)
  n = 0.00312
FEATURE [App::DocumentObjectGroupPython] G4_PHOTO_EMULSION  # scripted group (container) (typed FeaturePython)
  Dunit = g/cm3
  Dvalue = 3.815
  Group = -> [H_element070,C_element076,N_element035,O_element075,S_element019,Br_element004,Ag_element001,I_element005]
  conduct = 2
  density = 1
  expand = 3
  formula = G4_PHOTO_EMULSION
  name = G4_PHOTO_EMULSION
  specific = 4
FEATURE [App::DocumentObjectGroupPython] C_element077  label="C_element : 9"  # scripted group (container) (typed FeaturePython)
  n = 9
  ref = C_element
FEATURE [App::DocumentObjectGroupPython] H_element071  label="H_element : 033"  # scripted group (container) (typed FeaturePython)
  n = 10
  ref = H_element
FEATURE [App::DocumentObjectGroupPython] G4_PLASTIC_SC_VINYLTOLUENE  # scripted group (container) (typed FeaturePython)
  Dunit = g/cm3
  Dvalue = 1.032
  Group = -> [C_element077,H_element071]
  conduct = 2
  density = 1
  expand = 3
  formula = G4_PLASTIC_SC_VINYLTOLUENE
  name = G4_PLASTIC_SC_VINYLTOLUENE
  specific = 4
FEATURE [App::DocumentObjectGroupPython] Pu_element001  label="Pu_element : 1"  # scripted group (container) (typed FeaturePython)
  n = 1
  ref = Pu_element
FEATURE [App::DocumentObjectGroupPython] O_element076  label="O_element : 037"  # scripted group (container) (typed FeaturePython)
  n = 2
  ref = O_element
FEATURE [App::DocumentObjectGroupPython] G4_PLUTONIUM_DIOXIDE  # scripted group (container) (typed FeaturePython)
  Dunit = g/cm3
  Dvalue = 11.46
  Group = -> [Pu_element001,O_element076]
  conduct = 2
  density = 1
  expand = 3
  formula = G4_PLUTONIUM_DIOXIDE
  name = G4_PLUTONIUM_DIOXIDE
  specific = 4
FEATURE [App::DocumentObjectGroupPython] C_element078  label="C_element : 037"  # scripted group (container) (typed FeaturePython)
  n = 3
  ref = C_element
FEATURE [App::DocumentObjectGroupPython] H_element072  label="H_element : 034"  # scripted group (container) (typed FeaturePython)
  n = 3
  ref = H_element
FEATURE [App::DocumentObjectGroupPython] N_element036  label="N_element : 015"  # scripted group (container) (typed FeaturePython)
  n = 1
  ref = N_element
FEATURE [App::DocumentObjectGroupPython] G4_POLYACRYLONITRILE  # scripted group (container) (typed FeaturePython)
  Dunit = g/cm3
  Dvalue = 1.17
  Group = -> [C_element078,H_element072,N_element036]
  conduct = 2
  density = 1
  expand = 3
  formula = G4_POLYACRYLONITRILE
  name = G4_POLYACRYLONITRILE
  specific = 4
FEATURE [App::DocumentObjectGroupPython] C_element079  label="C_element : 16"  # scripted group (container) (typed FeaturePython)
  n = 16
  ref = C_element
FEATURE [App::DocumentObjectGroupPython] H_element073  label="H_element : 035"  # scripted group (container) (typed FeaturePython)
  n = 14
  ref = H_element
FEATURE [App::DocumentObjectGroupPython] O_element077  label="O_element : 038"  # scripted group (container) (typed FeaturePython)
  n = 3
  ref = O_element
FEATURE [App::DocumentObjectGroupPython] G4_POLYCARBONATE  # scripted group (container) (typed FeaturePython)
  Dunit = g/cm3
  Dvalue = 1.2
  Group = -> [C_element079,H_element073,O_element077]
  conduct = 2
  density = 1
  expand = 3
  formula = G4_POLYCARBONATE
  name = G4_POLYCARBONATE
  specific = 4
FEATURE [App::DocumentObjectGroupPython] C_element080  label="C_element : 038"  # scripted group (container) (typed FeaturePython)
  n = 8
  ref = C_element
FEATURE [App::DocumentObjectGroupPython] H_element074  label="H_element : 036"  # scripted group (container) (typed FeaturePython)
  n = 7
  ref = H_element
FEATURE [App::DocumentObjectGroupPython] Cl_element017  label="Cl_element : 007"  # scripted group (container) (typed FeaturePython)
  n = 1
  ref = Cl_element
FEATURE [App::DocumentObjectGroupPython] G4_POLYCHLOROSTYRENE  # scripted group (container) (typed FeaturePython)
  Dunit = g/cm3
  Dvalue = 1.3
  Group = -> [C_element080,H_element074,Cl_element017]
  conduct = 2
  density = 1
  expand = 3
  formula = G4_POLYCHLOROSTYRENE
  name = G4_POLYCHLOROSTYRENE
  specific = 4
FEATURE [App::DocumentObjectGroupPython] C_element081  label="C_element : 039"  # scripted group (container) (typed FeaturePython)
  n = 1
  ref = C_element
FEATURE [App::DocumentObjectGroupPython] H_element075  label="H_element : 037"  # scripted group (container) (typed FeaturePython)
  n = 2
  ref = H_element
FEATURE [App::DocumentObjectGroupPython] G4_POLYETHYLENE  # scripted group (container) (typed FeaturePython)
  Dunit = g/cm3
  Dvalue = 0.94
  Group = -> [C_element081,H_element075]
  conduct = 2
  density = 1
  expand = 3
  formula = G4_POLYETHYLENE
  name = G4_POLYETHYLENE
  specific = 4
FEATURE [App::DocumentObjectGroupPython] C_element082  label="C_element : 040"  # scripted group (container) (typed FeaturePython)
  n = 10
  ref = C_element
FEATURE [App::DocumentObjectGroupPython] H_element076  label="H_element : 038"  # scripted group (container) (typed FeaturePython)
  n = 8
  ref = H_element
FEATURE [App::DocumentObjectGroupPython] O_element078  label="O_element : 039"  # scripted group (container) (typed FeaturePython)
  n = 4
  ref = O_element
FEATURE [App::DocumentObjectGroupPython] G4_MYLAR  # scripted group (container) (typed FeaturePython)
  Dunit = g/cm3
  Dvalue = 1.4
  Group = -> [C_element082,H_element076,O_element078]
  conduct = 2
  density = 1
  expand = 3
  formula = G4_MYLAR
  name = G4_MYLAR
  specific = 4
FEATURE [App::DocumentObjectGroupPython] C_element083  label="C_element : 041"  # scripted group (container) (typed FeaturePython)
  n = 5
  ref = C_element
FEATURE [App::DocumentObjectGroupPython] H_element077  label="H_element : 039"  # scripted group (container) (typed FeaturePython)
  n = 8
  ref = H_element
FEATURE [App::DocumentObjectGroupPython] O_element079  label="O_element : 040"  # scripted group (container) (typed FeaturePython)
  n = 2
  ref = O_element
FEATURE [App::DocumentObjectGroupPython] G4_PLEXIGLASS  # scripted group (container) (typed FeaturePython)
  Dunit = g/cm3
  Dvalue = 1.19
  Group = -> [C_element083,H_element077,O_element079]
  conduct = 2
  density = 1
  expand = 3
  formula = G4_PLEXIGLASS
  name = G4_PLEXIGLASS
  specific = 4
FEATURE [App::DocumentObjectGroupPython] C_element084  label="C_element : 042"  # scripted group (container) (typed FeaturePython)
  n = 1
  ref = C_element
FEATURE [App::DocumentObjectGroupPython] H_element078  label="H_element : 040"  # scripted group (container) (typed FeaturePython)
  n = 2
  ref = H_element
FEATURE [App::DocumentObjectGroupPython] O_element080  label="O_element : 041"  # scripted group (container) (typed FeaturePython)
  n = 1
  ref = O_element
FEATURE [App::DocumentObjectGroupPython] G4_POLYOXYMETHYLENE  # scripted group (container) (typed FeaturePython)
  Dunit = g/cm3
  Dvalue = 1.425
  Group = -> [C_element084,H_element078,O_element080]
  conduct = 2
  density = 1
  expand = 3
  formula = G4_POLYOXYMETHYLENE
  name = G4_POLYOXYMETHYLENE
  specific = 4
FEATURE [App::DocumentObjectGroupPython] C_element085  label="C_element : 043"  # scripted group (container) (typed FeaturePython)
  n = 2
  ref = C_element
FEATURE [App::DocumentObjectGroupPython] H_element079  label="H_element : 041"  # scripted group (container) (typed FeaturePython)
  n = 4
  ref = H_element
FEATURE [App::DocumentObjectGroupPython] G4_POLYPROPYLENE  # scripted group (container) (typed FeaturePython)
  Dunit = g/cm3
  Dvalue = 0.9
  Group = -> [C_element085,H_element079]
  conduct = 2
  density = 1
  expand = 3
  formula = G4_POLYPROPYLENE
  name = G4_POLYPROPYLENE
  specific = 4
FEATURE [App::DocumentObjectGroupPython] C_element086  label="C_element : 044"  # scripted group (container) (typed FeaturePython)
  n = 8
  ref = C_element
FEATURE [App::DocumentObjectGroupPython] H_element080  label="H_element : 042"  # scripted group (container) (typed FeaturePython)
  n = 8
  ref = H_element
FEATURE [App::DocumentObjectGroupPython] G4_POLYSTYRENE  # scripted group (container) (typed FeaturePython)
  Dunit = g/cm3
  Dvalue = 1.06
  Group = -> [C_element086,H_element080]
  conduct = 2
  density = 1
  expand = 3
  formula = G4_POLYSTYRENE
  name = G4_POLYSTYRENE
  specific = 4
FEATURE [App::DocumentObjectGroupPython] C_element087  label="C_element : 045"  # scripted group (container) (typed FeaturePython)
  n = 2
  ref = C_element
FEATURE [App::DocumentObjectGroupPython] F_element014  label="F_element : 4"  # scripted group (container) (typed FeaturePython)
  n = 4
  ref = F_element
FEATURE [App::DocumentObjectGroupPython] G4_TEFLON  # scripted group (container) (typed FeaturePython)
  Dunit = g/cm3
  Dvalue = 2.2
  Group = -> [C_element087,F_element014]
  conduct = 2
  density = 1
  expand = 3
  formula = G4_TEFLON
  name = G4_TEFLON
  specific = 4
FEATURE [App::DocumentObjectGroupPython] C_element088  label="C_element : 046"  # scripted group (container) (typed FeaturePython)
  n = 2
  ref = C_element
FEATURE [App::DocumentObjectGroupPython] F_element015  label="F_element : 006"  # scripted group (container) (typed FeaturePython)
  n = 3
  ref = F_element
FEATURE [App::DocumentObjectGroupPython] Cl_element018  label="Cl_element : 008"  # scripted group (container) (typed FeaturePython)
  n = 1
  ref = Cl_element
FEATURE [App::DocumentObjectGroupPython] G4_POLYTRIFLUOROCHLOROETHYLENE  # scripted group (container) (typed FeaturePython)
  Dunit = g/cm3
  Dvalue = 2.1
  Group = -> [C_element088,F_element015,Cl_element018]
  conduct = 2
  density = 1
  expand = 3
  formula = G4_POLYTRIFLUOROCHLOROETHYLENE
  name = G4_POLYTRIFLUOROCHLOROETHYLENE
  specific = 4
FEATURE [App::DocumentObjectGroupPython] C_element089  label="C_element : 047"  # scripted group (container) (typed FeaturePython)
  n = 4
  ref = C_element
FEATURE [App::DocumentObjectGroupPython] H_element081  label="H_element : 043"  # scripted group (container) (typed FeaturePython)
  n = 6
  ref = H_element
FEATURE [App::DocumentObjectGroupPython] O_element081  label="O_element : 042"  # scripted group (container) (typed FeaturePython)
  n = 2
  ref = O_element
FEATURE [App::DocumentObjectGroupPython] G4_POLYVINYL_ACETATE  # scripted group (container) (typed FeaturePython)
  Dunit = g/cm3
  Dvalue = 1.19
  Group = -> [C_element089,H_element081,O_element081]
  conduct = 2
  density = 1
  expand = 3
  formula = G4_POLYVINYL_ACETATE
  name = G4_POLYVINYL_ACETATE
  specific = 4
FEATURE [App::DocumentObjectGroupPython] C_element090  label="C_element : 048"  # scripted group (container) (typed FeaturePython)
  n = 2
  ref = C_element
FEATURE [App::DocumentObjectGroupPython] H_element082  label="H_element : 044"  # scripted group (container) (typed FeaturePython)
  n = 4
  ref = H_element
FEATURE [App::DocumentObjectGroupPython] O_element082  label="O_element : 043"  # scripted group (container) (typed FeaturePython)
  n = 1
  ref = O_element
FEATURE [App::DocumentObjectGroupPython] G4_POLYVINYL_ALCOHOL  # scripted group (container) (typed FeaturePython)
  Dunit = g/cm3
  Dvalue = 1.3
  Group = -> [C_element090,H_element082,O_element082]
  conduct = 2
  density = 1
  expand = 3
  formula = G4_POLYVINYL_ALCOHOL
  name = G4_POLYVINYL_ALCOHOL
  specific = 4
FEATURE [App::DocumentObjectGroupPython] C_element091  label="C_element : 049"  # scripted group (container) (typed FeaturePython)
  n = 8
  ref = C_element
FEATURE [App::DocumentObjectGroupPython] H_element083  label="H_element : 045"  # scripted group (container) (typed FeaturePython)
  n = 14
  ref = H_element
FEATURE [App::DocumentObjectGroupPython] O_element083  label="O_element : 044"  # scripted group (container) (typed FeaturePython)
  n = 2
  ref = O_element
FEATURE [App::DocumentObjectGroupPython] G4_POLYVINYL_BUTYRAL  # scripted group (container) (typed FeaturePython)
  Dunit = g/cm3
  Dvalue = 1.12
  Group = -> [C_element091,H_element083,O_element083]
  conduct = 2
  density = 1
  expand = 3
  formula = G4_POLYVINYL_BUTYRAL
  name = G4_POLYVINYL_BUTYRAL
  specific = 4
FEATURE [App::DocumentObjectGroupPython] C_element092  label="C_element : 050"  # scripted group (container) (typed FeaturePython)
  n = 2
  ref = C_element
FEATURE [App::DocumentObjectGroupPython] H_element084  label="H_element : 046"  # scripted group (container) (typed FeaturePython)
  n = 3
  ref = H_element
FEATURE [App::DocumentObjectGroupPython] Cl_element019  label="Cl_element : 009"  # scripted group (container) (typed FeaturePython)
  n = 1
  ref = Cl_element
FEATURE [App::DocumentObjectGroupPython] G4_POLYVINYL_CHLORIDE  # scripted group (container) (typed FeaturePython)
  Dunit = g/cm3
  Dvalue = 1.3
  Group = -> [C_element092,H_element084,Cl_element019]
  conduct = 2
  density = 1
  expand = 3
  formula = G4_POLYVINYL_CHLORIDE
  name = G4_POLYVINYL_CHLORIDE
  specific = 4
FEATURE [App::DocumentObjectGroupPython] C_element093  label="C_element : 051"  # scripted group (container) (typed FeaturePython)
  n = 2
  ref = C_element
FEATURE [App::DocumentObjectGroupPython] H_element085  label="H_element : 047"  # scripted group (container) (typed FeaturePython)
  n = 2
  ref = H_element
FEATURE [App::DocumentObjectGroupPython] Cl_element020  label="Cl_element : 010"  # scripted group (container) (typed FeaturePython)
  n = 2
  ref = Cl_element
FEATURE [App::DocumentObjectGroupPython] G4_POLYVINYLIDENE_CHLORIDE  # scripted group (container) (typed FeaturePython)
  Dunit = g/cm3
  Dvalue = 1.7
  Group = -> [C_element093,H_element085,Cl_element020]
  conduct = 2
  density = 1
  expand = 3
  formula = G4_POLYVINYLIDENE_CHLORIDE
  name = G4_POLYVINYLIDENE_CHLORIDE
  specific = 4
FEATURE [App::DocumentObjectGroupPython] C_element094  label="C_element : 052"  # scripted group (container) (typed FeaturePython)
  n = 2
  ref = C_element
FEATURE [App::DocumentObjectGroupPython] H_element086  label="H_element : 048"  # scripted group (container) (typed FeaturePython)
  n = 2
  ref = H_element
FEATURE [App::DocumentObjectGroupPython] F_element016  label="F_element : 007"  # scripted group (container) (typed FeaturePython)
  n = 2
  ref = F_element
FEATURE [App::DocumentObjectGroupPython] G4_POLYVINYLIDENE_FLUORIDE  # scripted group (container) (typed FeaturePython)
  Dunit = g/cm3
  Dvalue = 1.76
  Group = -> [C_element094,H_element086,F_element016]
  conduct = 2
  density = 1
  expand = 3
  formula = G4_POLYVINYLIDENE_FLUORIDE
  name = G4_POLYVINYLIDENE_FLUORIDE
  specific = 4
FEATURE [App::DocumentObjectGroupPython] C_element095  label="C_element : 053"  # scripted group (container) (typed FeaturePython)
  n = 6
  ref = C_element
FEATURE [App::DocumentObjectGroupPython] H_element087  label="H_element : 9"  # scripted group (container) (typed FeaturePython)
  n = 9
  ref = H_element
FEATURE [App::DocumentObjectGroupPython] N_element037  label="N_element : 016"  # scripted group (container) (typed FeaturePython)
  n = 1
  ref = N_element
FEATURE [App::DocumentObjectGroupPython] O_element084  label="O_element : 045"  # scripted group (container) (typed FeaturePython)
  n = 1
  ref = O_element
FEATURE [App::DocumentObjectGroupPython] G4_POLYVINYL_PYRROLIDONE  # scripted group (container) (typed FeaturePython)
  Dunit = g/cm3
  Dvalue = 1.25
  Group = -> [C_element095,H_element087,N_element037,O_element084]
  conduct = 2
  density = 1
  expand = 3
  formula = G4_POLYVINYL_PYRROLIDONE
  name = G4_POLYVINYL_PYRROLIDONE
  specific = 4
FEATURE [App::DocumentObjectGroupPython] K_element008  label="K_element : 1"  # scripted group (container) (typed FeaturePython)
  n = 1
  ref = K_element
FEATURE [App::DocumentObjectGroupPython] I_element006  label="I_element : 003"  # scripted group (container) (typed FeaturePython)
  n = 1
  ref = I_element
FEATURE [App::DocumentObjectGroupPython] G4_POTASSIUM_IODIDE  # scripted group (container) (typed FeaturePython)
  Dunit = g/cm3
  Dvalue = 3.13
  Group = -> [K_element008,I_element006]
  conduct = 2
  density = 1
  expand = 3
  formula = G4_POTASSIUM_IODIDE
  name = G4_POTASSIUM_IODIDE
  specific = 4
FEATURE [App::DocumentObjectGroupPython] K_element009  label="K_element : 2"  # scripted group (container) (typed FeaturePython)
  n = 2
  ref = K_element
FEATURE [App::DocumentObjectGroupPython] O_element085  label="O_element : 046"  # scripted group (container) (typed FeaturePython)
  n = 1
  ref = O_element
FEATURE [App::DocumentObjectGroupPython] G4_POTASSIUM_OXIDE  # scripted group (container) (typed FeaturePython)
  Dunit = g/cm3
  Dvalue = 2.32
  Group = -> [K_element009,O_element085]
  conduct = 2
  density = 1
  expand = 3
  formula = G4_POTASSIUM_OXIDE
  name = G4_POTASSIUM_OXIDE
  specific = 4
FEATURE [App::DocumentObjectGroupPython] C_element096  label="C_element : 054"  # scripted group (container) (typed FeaturePython)
  n = 3
  ref = C_element
FEATURE [App::DocumentObjectGroupPython] H_element088  label="H_element : 049"  # scripted group (container) (typed FeaturePython)
  n = 8
  ref = H_element
FEATURE [App::DocumentObjectGroupPython] G4_PROPANE  # scripted group (container) (typed FeaturePython)
  Dunit = g/cm3
  Dvalue = 0.00187939
  Group = -> [C_element096,H_element088]
  conduct = 2
  density = 1
  expand = 3
  formula = G4_PROPANE
  name = G4_PROPANE
  specific = 4
FEATURE [App::DocumentObjectGroupPython] C_element097  label="C_element : 055"  # scripted group (container) (typed FeaturePython)
  n = 3
  ref = C_element
FEATURE [App::DocumentObjectGroupPython] H_element089  label="H_element : 050"  # scripted group (container) (typed FeaturePython)
  n = 8
  ref = H_element
FEATURE [App::DocumentObjectGroupPython] G4_lPROPANE  # scripted group (container) (typed FeaturePython)
  Dunit = g/cm3
  Dvalue = 0.43
  Group = -> [C_element097,H_element089]
  conduct = 2
  density = 1
  expand = 3
  formula = G4_lPROPANE
  name = G4_lPROPANE
  specific = 4
FEATURE [App::DocumentObjectGroupPython] C_element098  label="C_element : 056"  # scripted group (container) (typed FeaturePython)
  n = 3
  ref = C_element
FEATURE [App::DocumentObjectGroupPython] H_element090  label="H_element : 051"  # scripted group (container) (typed FeaturePython)
  n = 8
  ref = H_element
FEATURE [App::DocumentObjectGroupPython] O_element086  label="O_element : 047"  # scripted group (container) (typed FeaturePython)
  n = 1
  ref = O_element
FEATURE [App::DocumentObjectGroupPython] G4_N_PROPYL_ALCOHOL  label="G4_N-PROPYL_ALCOHOL"  # scripted group (container) (typed FeaturePython)
  Dunit = g/cm3
  Dvalue = 0.8035
  Group = -> [C_element098,H_element090,O_element086]
  conduct = 2
  density = 1
  expand = 3
  formula = G4_N-PROPYL_ALCOHOL
  name = G4_N-PROPYL_ALCOHOL
  specific = 4
FEATURE [App::DocumentObjectGroupPython] C_element099  label="C_element : 057"  # scripted group (container) (typed FeaturePython)
  n = 5
  ref = C_element
FEATURE [App::DocumentObjectGroupPython] H_element091  label="H_element : 052"  # scripted group (container) (typed FeaturePython)
  n = 5
  ref = H_element
FEATURE [App::DocumentObjectGroupPython] N_element038  label="N_element : 017"  # scripted group (container) (typed FeaturePython)
  n = 1
  ref = N_element
FEATURE [App::DocumentObjectGroupPython] G4_PYRIDINE  # scripted group (container) (typed FeaturePython)
  Dunit = g/cm3
  Dvalue = 0.9819
  Group = -> [C_element099,H_element091,N_element038]
  conduct = 2
  density = 1
  expand = 3
  formula = G4_PYRIDINE
  name = G4_PYRIDINE
  specific = 4
FEATURE [App::DocumentObjectGroupPython] H_element092  label="H_element : 0.144"  # scripted group (container) (typed FeaturePython)
  n = 0.143711
FEATURE [App::DocumentObjectGroupPython] C_element100  label="C_element : 0.856"  # scripted group (container) (typed FeaturePython)
  n = 0.856289
FEATURE [App::DocumentObjectGroupPython] G4_RUBBER_BUTYL  # scripted group (container) (typed FeaturePython)
  Dunit = g/cm3
  Dvalue = 0.92
  Group = -> [H_element092,C_element100]
  conduct = 2
  density = 1
  expand = 3
  formula = G4_RUBBER_BUTYL
  name = G4_RUBBER_BUTYL
  specific = 4
FEATURE [App::DocumentObjectGroupPython] H_element093  label="H_element : 0.118"  # scripted group (container) (typed FeaturePython)
  n = 0.118371
FEATURE [App::DocumentObjectGroupPython] C_element101  label="C_element : 0.882"  # scripted group (container) (typed FeaturePython)
  n = 0.881629
FEATURE [App::DocumentObjectGroupPython] G4_RUBBER_NATURAL  # scripted group (container) (typed FeaturePython)
  Dunit = g/cm3
  Dvalue = 0.92
  Group = -> [H_element093,C_element101]
  conduct = 2
  density = 1
  expand = 3
  formula = G4_RUBBER_NATURAL
  name = G4_RUBBER_NATURAL
  specific = 4
FEATURE [App::DocumentObjectGroupPython] H_element094  label="H_element : 0.145"  # scripted group (container) (typed FeaturePython)
  n = 0.05692
FEATURE [App::DocumentObjectGroupPython] C_element102  label="C_element : 0.543"  # scripted group (container) (typed FeaturePython)
  n = 0.542646
FEATURE [App::DocumentObjectGroupPython] Cl_element021  label="Cl_element : 0.400"  # scripted group (container) (typed FeaturePython)
  n = 0.400434
FEATURE [App::DocumentObjectGroupPython] G4_RUBBER_NEOPRENE  # scripted group (container) (typed FeaturePython)
  Dunit = g/cm3
  Dvalue = 1.23
  Group = -> [H_element094,C_element102,Cl_element021]
  conduct = 2
  density = 1
  expand = 3
  formula = G4_RUBBER_NEOPRENE
  name = G4_RUBBER_NEOPRENE
  specific = 4
FEATURE [App::DocumentObjectGroupPython] Si_element006  label="Si_element : 1"  # scripted group (container) (typed FeaturePython)
  n = 1
  ref = Si_element
FEATURE [App::DocumentObjectGroupPython] O_element087  label="O_element : 048"  # scripted group (container) (typed FeaturePython)
  n = 2
  ref = O_element
FEATURE [App::DocumentObjectGroupPython] G4_SILICON_DIOXIDE  # scripted group (container) (typed FeaturePython)
  Dunit = g/cm3
  Dvalue = 2.32
  Group = -> [Si_element006,O_element087]
  conduct = 2
  density = 1
  expand = 3
  formula = G4_SILICON_DIOXIDE
  name = G4_SILICON_DIOXIDE
  specific = 4
FEATURE [App::DocumentObjectGroupPython] Ag_element002  label="Ag_element : 1"  # scripted group (container) (typed FeaturePython)
  n = 1
  ref = Ag_element
FEATURE [App::DocumentObjectGroupPython] Br_element005  label="Br_element : 003"  # scripted group (container) (typed FeaturePython)
  n = 1
  ref = Br_element
FEATURE [App::DocumentObjectGroupPython] G4_SILVER_BROMIDE  # scripted group (container) (typed FeaturePython)
  Dunit = g/cm3
  Dvalue = 6.473
  Group = -> [Ag_element002,Br_element005]
  conduct = 2
  density = 1
  expand = 3
  formula = G4_SILVER_BROMIDE
  name = G4_SILVER_BROMIDE
  specific = 4
FEATURE [App::DocumentObjectGroupPython] Ag_element003  label="Ag_element : 002"  # scripted group (container) (typed FeaturePython)
  n = 1
  ref = Ag_element
FEATURE [App::DocumentObjectGroupPython] Cl_element022  label="Cl_element : 011"  # scripted group (container) (typed FeaturePython)
  n = 1
  ref = Cl_element
FEATURE [App::DocumentObjectGroupPython] G4_SILVER_CHLORIDE  # scripted group (container) (typed FeaturePython)
  Dunit = g/cm3
  Dvalue = 5.56
  Group = -> [Ag_element003,Cl_element022]
  conduct = 2
  density = 1
  expand = 3
  formula = G4_SILVER_CHLORIDE
  name = G4_SILVER_CHLORIDE
  specific = 4
FEATURE [App::DocumentObjectGroupPython] Br_element006  label="Br_element : 0.423"  # scripted group (container) (typed FeaturePython)
  n = 0.422895
FEATURE [App::DocumentObjectGroupPython] Ag_element004  label="Ag_element : 0.574"  # scripted group (container) (typed FeaturePython)
  n = 0.573748
FEATURE [App::DocumentObjectGroupPython] I_element007  label="I_element : 0.649"  # scripted group (container) (typed FeaturePython)
  n = 0.003357
FEATURE [App::DocumentObjectGroupPython] G4_SILVER_HALIDES  # scripted group (container) (typed FeaturePython)
  Dunit = g/cm3
  Dvalue = 6.47
  Group = -> [Br_element006,Ag_element004,I_element007]
  conduct = 2
  density = 1
  expand = 3
  formula = G4_SILVER_HALIDES
  name = G4_SILVER_HALIDES
  specific = 4
FEATURE [App::DocumentObjectGroupPython] Ag_element005  label="Ag_element : 003"  # scripted group (container) (typed FeaturePython)
  n = 1
  ref = Ag_element
FEATURE [App::DocumentObjectGroupPython] I_element008  label="I_element : 004"  # scripted group (container) (typed FeaturePython)
  n = 1
  ref = I_element
FEATURE [App::DocumentObjectGroupPython] G4_SILVER_IODIDE  # scripted group (container) (typed FeaturePython)
  Dunit = g/cm3
  Dvalue = 6.01
  Group = -> [Ag_element005,I_element008]
  conduct = 2
  density = 1
  expand = 3
  formula = G4_SILVER_IODIDE
  name = G4_SILVER_IODIDE
  specific = 4
FEATURE [App::DocumentObjectGroupPython] H_element095  label="H_element : 0.100"  # scripted group (container) (typed FeaturePython)
  n = 0.1
FEATURE [App::DocumentObjectGroupPython] C_element103  label="C_element : 0.204"  # scripted group (container) (typed FeaturePython)
  n = 0.204
FEATURE [App::DocumentObjectGroupPython] N_element039  label="N_element : 0.759"  # scripted group (container) (typed FeaturePython)
  n = 0.042
FEATURE [App::DocumentObjectGroupPython] O_element088  label="O_element : 0.645"  # scripted group (container) (typed FeaturePython)
  n = 0.645
FEATURE [App::DocumentObjectGroupPython] Na_element013  label="Na_element : 0.100"  # scripted group (container) (typed FeaturePython)
  n = 0.002
FEATURE [App::DocumentObjectGroupPython] P_element009  label="P_element : 0.107"  # scripted group (container) (typed FeaturePython)
  n = 0.001
FEATURE [App::DocumentObjectGroupPython] S_element020  label="S_element : 0.021"  # scripted group (container) (typed FeaturePython)
  n = 0.002
FEATURE [App::DocumentObjectGroupPython] Cl_element023  label="Cl_element : 0.590"  # scripted group (container) (typed FeaturePython)
  n = 0.003
FEATURE [App::DocumentObjectGroupPython] K_element010  label="K_element : 0.001"  # scripted group (container) (typed FeaturePython)
  n = 0.001
FEATURE [App::DocumentObjectGroupPython] G4_SKIN_ICRP  # scripted group (container) (typed FeaturePython)
  Dunit = g/cm3
  Dvalue = 1.09
  Group = -> [H_element095,C_element103,N_element039,O_element088,Na_element013,P_element009,S_element020,Cl_element023,K_element010]
  conduct = 2
  density = 1
  expand = 3
  formula = G4_SKIN_ICRP
  name = G4_SKIN_ICRP
  specific = 4
FEATURE [App::DocumentObjectGroupPython] Na_element014  label="Na_element : 2"  # scripted group (container) (typed FeaturePython)
  n = 2
  ref = Na_element
FEATURE [App::DocumentObjectGroupPython] C_element104  label="C_element : 058"  # scripted group (container) (typed FeaturePython)
  n = 1
  ref = C_element
FEATURE [App::DocumentObjectGroupPython] O_element089  label="O_element : 049"  # scripted group (container) (typed FeaturePython)
  n = 3
  ref = O_element
FEATURE [App::DocumentObjectGroupPython] G4_SODIUM_CARBONATE  # scripted group (container) (typed FeaturePython)
  Dunit = g/cm3
  Dvalue = 2.532
  Group = -> [Na_element014,C_element104,O_element089]
  conduct = 2
  density = 1
  expand = 3
  formula = G4_SODIUM_CARBONATE
  name = G4_SODIUM_CARBONATE
  specific = 4
FEATURE [App::DocumentObjectGroupPython] Na_element015  label="Na_element : 1"  # scripted group (container) (typed FeaturePython)
  n = 1
  ref = Na_element
FEATURE [App::DocumentObjectGroupPython] I_element009  label="I_element : 005"  # scripted group (container) (typed FeaturePython)
  n = 1
  ref = I_element
FEATURE [App::DocumentObjectGroupPython] G4_SODIUM_IODIDE  # scripted group (container) (typed FeaturePython)
  Dunit = g/cm3
  Dvalue = 3.667
  Group = -> [Na_element015,I_element009]
  conduct = 2
  density = 1
  expand = 3
  formula = G4_SODIUM_IODIDE
  name = G4_SODIUM_IODIDE
  specific = 4
FEATURE [App::DocumentObjectGroupPython] Na_element016  label="Na_element : 003"  # scripted group (container) (typed FeaturePython)
  n = 2
  ref = Na_element
FEATURE [App::DocumentObjectGroupPython] O_element090  label="O_element : 050"  # scripted group (container) (typed FeaturePython)
  n = 1
  ref = O_element
FEATURE [App::DocumentObjectGroupPython] G4_SODIUM_MONOXIDE  # scripted group (container) (typed FeaturePython)
  Dunit = g/cm3
  Dvalue = 2.27
  Group = -> [Na_element016,O_element090]
  conduct = 2
  density = 1
  expand = 3
  formula = G4_SODIUM_MONOXIDE
  name = G4_SODIUM_MONOXIDE
  specific = 4
FEATURE [App::DocumentObjectGroupPython] Na_element017  label="Na_element : 004"  # scripted group (container) (typed FeaturePython)
  n = 1
  ref = Na_element
FEATURE [App::DocumentObjectGroupPython] N_element040  label="N_element : 018"  # scripted group (container) (typed FeaturePython)
  n = 1
  ref = N_element
FEATURE [App::DocumentObjectGroupPython] O_element091  label="O_element : 051"  # scripted group (container) (typed FeaturePython)
  n = 3
  ref = O_element
FEATURE [App::DocumentObjectGroupPython] G4_SODIUM_NITRATE  # scripted group (container) (typed FeaturePython)
  Dunit = g/cm3
  Dvalue = 2.261
  Group = -> [Na_element017,N_element040,O_element091]
  conduct = 2
  density = 1
  expand = 3
  formula = G4_SODIUM_NITRATE
  name = G4_SODIUM_NITRATE
  specific = 4
FEATURE [App::DocumentObjectGroupPython] C_element105  label="C_element : 059"  # scripted group (container) (typed FeaturePython)
  n = 14
  ref = C_element
FEATURE [App::DocumentObjectGroupPython] H_element096  label="H_element : 053"  # scripted group (container) (typed FeaturePython)
  n = 12
  ref = H_element
FEATURE [App::DocumentObjectGroupPython] G4_STILBENE  # scripted group (container) (typed FeaturePython)
  Dunit = g/cm3
  Dvalue = 0.9707
  Group = -> [C_element105,H_element096]
  conduct = 2
  density = 1
  expand = 3
  formula = G4_STILBENE
  name = G4_STILBENE
  specific = 4
FEATURE [App::DocumentObjectGroupPython] C_element106  label="C_element : 12"  # scripted group (container) (typed FeaturePython)
  n = 12
  ref = C_element
FEATURE [App::DocumentObjectGroupPython] H_element097  label="H_element : 22"  # scripted group (container) (typed FeaturePython)
  n = 22
  ref = H_element
FEATURE [App::DocumentObjectGroupPython] O_element092  label="O_element : 11"  # scripted group (container) (typed FeaturePython)
  n = 11
  ref = O_element
FEATURE [App::DocumentObjectGroupPython] G4_SUCROSE  # scripted group (container) (typed FeaturePython)
  Dunit = g/cm3
  Dvalue = 1.5805
  Group = -> [C_element106,H_element097,O_element092]
  conduct = 2
  density = 1
  expand = 3
  formula = G4_SUCROSE
  name = G4_SUCROSE
  specific = 4
FEATURE [App::DocumentObjectGroupPython] C_element107  label="C_element : 18"  # scripted group (container) (typed FeaturePython)
  n = 18
  ref = C_element
FEATURE [App::DocumentObjectGroupPython] H_element098  label="H_element : 054"  # scripted group (container) (typed FeaturePython)
  n = 14
  ref = H_element
FEATURE [App::DocumentObjectGroupPython] G4_TERPHENYL  # scripted group (container) (typed FeaturePython)
  Dunit = g/cm3
  Dvalue = 1.24
  Group = -> [C_element107,H_element098]
  conduct = 2
  density = 1
  expand = 3
  formula = G4_TERPHENYL
  name = G4_TERPHENYL
  specific = 4
FEATURE [App::DocumentObjectGroupPython] H_element099  label="H_element : 0.146"  # scripted group (container) (typed FeaturePython)
  n = 0.106
FEATURE [App::DocumentObjectGroupPython] C_element108  label="C_element : 0.883"  # scripted group (container) (typed FeaturePython)
  n = 0.099
FEATURE [App::DocumentObjectGroupPython] N_element041  label="N_element : 0.020"  # scripted group (container) (typed FeaturePython)
  n = 0.02
FEATURE [App::DocumentObjectGroupPython] O_element093  label="O_element : 0.766"  # scripted group (container) (typed FeaturePython)
  n = 0.766
FEATURE [App::DocumentObjectGroupPython] Na_element018  label="Na_element : 0.101"  # scripted group (container) (typed FeaturePython)
  n = 0.002
FEATURE [App::DocumentObjectGroupPython] P_element010  label="P_element : 0.108"  # scripted group (container) (typed FeaturePython)
  n = 0.001
FEATURE [App::DocumentObjectGroupPython] S_element021  label="S_element : 0.022"  # scripted group (container) (typed FeaturePython)
  n = 0.002
FEATURE [App::DocumentObjectGroupPython] Cl_element024  label="Cl_element : 0.002"  # scripted group (container) (typed FeaturePython)
  n = 0.002
FEATURE [App::DocumentObjectGroupPython] K_element011  label="K_element : 0.017"  # scripted group (container) (typed FeaturePython)
  n = 0.002
FEATURE [App::DocumentObjectGroupPython] G4_TESTIS_ICRP  # scripted group (container) (typed FeaturePython)
  Dunit = g/cm3
  Dvalue = 1.04
  Group = -> [H_element099,C_element108,N_element041,O_element093,Na_element018,P_element010,S_element021,Cl_element024,K_element011]
  conduct = 2
  density = 1
  expand = 3
  formula = G4_TESTIS_ICRP
  name = G4_TESTIS_ICRP
  specific = 4
FEATURE [App::DocumentObjectGroupPython] C_element109  label="C_element : 060"  # scripted group (container) (typed FeaturePython)
  n = 2
  ref = C_element
FEATURE [App::DocumentObjectGroupPython] Cl_element025  label="Cl_element : 012"  # scripted group (container) (typed FeaturePython)
  n = 4
  ref = Cl_element
FEATURE [App::DocumentObjectGroupPython] G4_TETRACHLOROETHYLENE  # scripted group (container) (typed FeaturePython)
  Dunit = g/cm3
  Dvalue = 1.625
  Group = -> [C_element109,Cl_element025]
  conduct = 2
  density = 1
  expand = 3
  formula = G4_TETRACHLOROETHYLENE
  name = G4_TETRACHLOROETHYLENE
  specific = 4
FEATURE [App::DocumentObjectGroupPython] Tl_element001  label="Tl_element : 1"  # scripted group (container) (typed FeaturePython)
  n = 1
  ref = Tl_element
FEATURE [App::DocumentObjectGroupPython] Cl_element026  label="Cl_element : 013"  # scripted group (container) (typed FeaturePython)
  n = 1
  ref = Cl_element
FEATURE [App::DocumentObjectGroupPython] G4_THALLIUM_CHLORIDE  # scripted group (container) (typed FeaturePython)
  Dunit = g/cm3
  Dvalue = 7.004
  Group = -> [Tl_element001,Cl_element026]
  conduct = 2
  density = 1
  expand = 3
  formula = G4_THALLIUM_CHLORIDE
  name = G4_THALLIUM_CHLORIDE
  specific = 4
FEATURE [App::DocumentObjectGroupPython] H_element100  label="H_element : 0.147"  # scripted group (container) (typed FeaturePython)
  n = 0.105
FEATURE [App::DocumentObjectGroupPython] C_element110  label="C_element : 0.256"  # scripted group (container) (typed FeaturePython)
  n = 0.256
FEATURE [App::DocumentObjectGroupPython] N_element042  label="N_element : 0.760"  # scripted group (container) (typed FeaturePython)
  n = 0.027
FEATURE [App::DocumentObjectGroupPython] O_element094  label="O_element : 0.602"  # scripted group (container) (typed FeaturePython)
  n = 0.602
FEATURE [App::DocumentObjectGroupPython] Na_element019  label="Na_element : 0.102"  # scripted group (container) (typed FeaturePython)
  n = 0.001
FEATURE [App::DocumentObjectGroupPython] P_element011  label="P_element : 0.109"  # scripted group (container) (typed FeaturePython)
  n = 0.002
FEATURE [App::DocumentObjectGroupPython] S_element022  label="S_element : 0.023"  # scripted group (container) (typed FeaturePython)
  n = 0.003
FEATURE [App::DocumentObjectGroupPython] Cl_element027  label="Cl_element : 0.591"  # scripted group (container) (typed FeaturePython)
  n = 0.002
FEATURE [App::DocumentObjectGroupPython] K_element012  label="K_element : 0.018"  # scripted group (container) (typed FeaturePython)
  n = 0.002
FEATURE [App::DocumentObjectGroupPython] G4_TISSUE_SOFT_ICRP  # scripted group (container) (typed FeaturePython)
  Dunit = g/cm3
  Dvalue = 1.03
  Group = -> [H_element100,C_element110,N_element042,O_element094,Na_element019,P_element011,S_element022,Cl_element027,K_element012]
  conduct = 2
  density = 1
  expand = 3
  formula = G4_TISSUE_SOFT_ICRP
  name = G4_TISSUE_SOFT_ICRP
  specific = 4
FEATURE [App::DocumentObjectGroupPython] H_element101  label="H_element : 0.148"  # scripted group (container) (typed FeaturePython)
  n = 0.101
FEATURE [App::DocumentObjectGroupPython] C_element111  label="C_element : 0.111"  # scripted group (container) (typed FeaturePython)
  n = 0.111
FEATURE [App::DocumentObjectGroupPython] N_element043  label="N_element : 0.026"  # scripted group (container) (typed FeaturePython)
  n = 0.026
FEATURE [App::DocumentObjectGroupPython] O_element095  label="O_element : 0.762"  # scripted group (container) (typed FeaturePython)
  n = 0.762
FEATURE [App::DocumentObjectGroupPython] G4_TISSUE_SOFT_ICRU_4  label="G4_TISSUE_SOFT_ICRU-4"  # scripted group (container) (typed FeaturePython)
  Dunit = g/cm3
  Dvalue = 1
  Group = -> [H_element101,C_element111,N_element043,O_element095]
  conduct = 2
  density = 1
  expand = 3
  formula = G4_TISSUE_SOFT_ICRU-4
  name = G4_TISSUE_SOFT_ICRU-4
  specific = 4
FEATURE [App::DocumentObjectGroupPython] H_element102  label="H_element : 0.149"  # scripted group (container) (typed FeaturePython)
  n = 0.101869
FEATURE [App::DocumentObjectGroupPython] C_element112  label="C_element : 0.456"  # scripted group (container) (typed FeaturePython)
  n = 0.456179
FEATURE [App::DocumentObjectGroupPython] N_element044  label="N_element : 0.761"  # scripted group (container) (typed FeaturePython)
  n = 0.035172
FEATURE [App::DocumentObjectGroupPython] O_element096  label="O_element : 0.407"  # scripted group (container) (typed FeaturePython)
  n = 0.40678
FEATURE [App::DocumentObjectGroupPython] G4_TISSUE_METHANE  label="G4_TISSUE-METHANE"  # scripted group (container) (typed FeaturePython)
  Dunit = g/cm3
  Dvalue = 0.00106409
  Group = -> [H_element102,C_element112,N_element044,O_element096]
  conduct = 2
  density = 1
  expand = 3
  formula = G4_TISSUE-METHANE
  name = G4_TISSUE-METHANE
  specific = 4
FEATURE [App::DocumentObjectGroupPython] H_element103  label="H_element : 0.103"  # scripted group (container) (typed FeaturePython)
  n = 0.102672
FEATURE [App::DocumentObjectGroupPython] C_element113  label="C_element : 0.569"  # scripted group (container) (typed FeaturePython)
  n = 0.56894
FEATURE [App::DocumentObjectGroupPython] N_element045  label="N_element : 0.762"  # scripted group (container) (typed FeaturePython)
  n = 0.035022
FEATURE [App::DocumentObjectGroupPython] O_element097  label="O_element : 0.293"  # scripted group (container) (typed FeaturePython)
  n = 0.293366
FEATURE [App::DocumentObjectGroupPython] G4_TISSUE_PROPANE  label="G4_TISSUE-PROPANE"  # scripted group (container) (typed FeaturePython)
  Dunit = g/cm3
  Dvalue = 0.00182628
  Group = -> [H_element103,C_element113,N_element045,O_element097]
  conduct = 2
  density = 1
  expand = 3
  formula = G4_TISSUE-PROPANE
  name = G4_TISSUE-PROPANE
  specific = 4
FEATURE [App::DocumentObjectGroupPython] Ti_element003  label="Ti_element : 1"  # scripted group (container) (typed FeaturePython)
  n = 1
  ref = Ti_element
FEATURE [App::DocumentObjectGroupPython] O_element098  label="O_element : 052"  # scripted group (container) (typed FeaturePython)
  n = 2
  ref = O_element
FEATURE [App::DocumentObjectGroupPython] G4_TITANIUM_DIOXIDE  # scripted group (container) (typed FeaturePython)
  Dunit = g/cm3
  Dvalue = 4.26
  Group = -> [Ti_element003,O_element098]
  conduct = 2
  density = 1
  expand = 3
  formula = G4_TITANIUM_DIOXIDE
  name = G4_TITANIUM_DIOXIDE
  specific = 4
FEATURE [App::DocumentObjectGroupPython] C_element114  label="C_element : 061"  # scripted group (container) (typed FeaturePython)
  n = 7
  ref = C_element
FEATURE [App::DocumentObjectGroupPython] H_element104  label="H_element : 055"  # scripted group (container) (typed FeaturePython)
  n = 8
  ref = H_element
FEATURE [App::DocumentObjectGroupPython] G4_TOLUENE  # scripted group (container) (typed FeaturePython)
  Dunit = g/cm3
  Dvalue = 0.8669
  Group = -> [C_element114,H_element104]
  conduct = 2
  density = 1
  expand = 3
  formula = G4_TOLUENE
  name = G4_TOLUENE
  specific = 4
FEATURE [App::DocumentObjectGroupPython] C_element115  label="C_element : 062"  # scripted group (container) (typed FeaturePython)
  n = 2
  ref = C_element
FEATURE [App::DocumentObjectGroupPython] H_element105  label="H_element : 056"  # scripted group (container) (typed FeaturePython)
  n = 1
  ref = H_element
FEATURE [App::DocumentObjectGroupPython] Cl_element028  label="Cl_element : 014"  # scripted group (container) (typed FeaturePython)
  n = 3
  ref = Cl_element
FEATURE [App::DocumentObjectGroupPython] G4_TRICHLOROETHYLENE  # scripted group (container) (typed FeaturePython)
  Dunit = g/cm3
  Dvalue = 1.46
  Group = -> [C_element115,H_element105,Cl_element028]
  conduct = 2
  density = 1
  expand = 3
  formula = G4_TRICHLOROETHYLENE
  name = G4_TRICHLOROETHYLENE
  specific = 4
FEATURE [App::DocumentObjectGroupPython] C_element116  label="C_element : 063"  # scripted group (container) (typed FeaturePython)
  n = 6
  ref = C_element
FEATURE [App::DocumentObjectGroupPython] H_element106  label="H_element : 15"  # scripted group (container) (typed FeaturePython)
  n = 15
  ref = H_element
FEATURE [App::DocumentObjectGroupPython] O_element099  label="O_element : 053"  # scripted group (container) (typed FeaturePython)
  n = 4
  ref = O_element
FEATURE [App::DocumentObjectGroupPython] P_element012  label="P_element : 1"  # scripted group (container) (typed FeaturePython)
  n = 1
  ref = P_element
FEATURE [App::DocumentObjectGroupPython] G4_TRIETHYL_PHOSPHATE  # scripted group (container) (typed FeaturePython)
  Dunit = g/cm3
  Dvalue = 1.07
  Group = -> [C_element116,H_element106,O_element099,P_element012]
  conduct = 2
  density = 1
  expand = 3
  formula = G4_TRIETHYL_PHOSPHATE
  name = G4_TRIETHYL_PHOSPHATE
  specific = 4
FEATURE [App::DocumentObjectGroupPython] W_element003  label="W_element : 003"  # scripted group (container) (typed FeaturePython)
  n = 1
  ref = W_element
FEATURE [App::DocumentObjectGroupPython] F_element017  label="F_element : 6"  # scripted group (container) (typed FeaturePython)
  n = 6
  ref = F_element
FEATURE [App::DocumentObjectGroupPython] G4_TUNGSTEN_HEXAFLUORIDE  # scripted group (container) (typed FeaturePython)
  Dunit = g/cm3
  Dvalue = 2.4
  Group = -> [W_element003,F_element017]
  conduct = 2
  density = 1
  expand = 3
  formula = G4_TUNGSTEN_HEXAFLUORIDE
  name = G4_TUNGSTEN_HEXAFLUORIDE
  specific = 4
FEATURE [App::DocumentObjectGroupPython] U_element001  label="U_element : 1"  # scripted group (container) (typed FeaturePython)
  n = 1
  ref = U_element
FEATURE [App::DocumentObjectGroupPython] C_element117  label="C_element : 064"  # scripted group (container) (typed FeaturePython)
  n = 2
  ref = C_element
FEATURE [App::DocumentObjectGroupPython] G4_URANIUM_DICARBIDE  # scripted group (container) (typed FeaturePython)
  Dunit = g/cm3
  Dvalue = 11.28
  Group = -> [U_element001,C_element117]
  conduct = 2
  density = 1
  expand = 3
  formula = G4_URANIUM_DICARBIDE
  name = G4_URANIUM_DICARBIDE
  specific = 4
FEATURE [App::DocumentObjectGroupPython] U_element002  label="U_element : 002"  # scripted group (container) (typed FeaturePython)
  n = 1
  ref = U_element
FEATURE [App::DocumentObjectGroupPython] C_element118  label="C_element : 065"  # scripted group (container) (typed FeaturePython)
  n = 1
  ref = C_element
FEATURE [App::DocumentObjectGroupPython] G4_URANIUM_MONOCARBIDE  # scripted group (container) (typed FeaturePython)
  Dunit = g/cm3
  Dvalue = 13.63
  Group = -> [U_element002,C_element118]
  conduct = 2
  density = 1
  expand = 3
  formula = G4_URANIUM_MONOCARBIDE
  name = G4_URANIUM_MONOCARBIDE
  specific = 4
FEATURE [App::DocumentObjectGroupPython] U_element003  label="U_element : 003"  # scripted group (container) (typed FeaturePython)
  n = 1
  ref = U_element
FEATURE [App::DocumentObjectGroupPython] O_element100  label="O_element : 054"  # scripted group (container) (typed FeaturePython)
  n = 2
  ref = O_element
FEATURE [App::DocumentObjectGroupPython] G4_URANIUM_OXIDE  # scripted group (container) (typed FeaturePython)
  Dunit = g/cm3
  Dvalue = 10.96
  Group = -> [U_element003,O_element100]
  conduct = 2
  density = 1
  expand = 3
  formula = G4_URANIUM_OXIDE
  name = G4_URANIUM_OXIDE
  specific = 4
FEATURE [App::DocumentObjectGroupPython] C_element119  label="C_element : 066"  # scripted group (container) (typed FeaturePython)
  n = 1
  ref = C_element
FEATURE [App::DocumentObjectGroupPython] H_element107  label="H_element : 057"  # scripted group (container) (typed FeaturePython)
  n = 4
  ref = H_element
FEATURE [App::DocumentObjectGroupPython] N_element046  label="N_element : 019"  # scripted group (container) (typed FeaturePython)
  n = 2
  ref = N_element
FEATURE [App::DocumentObjectGroupPython] O_element101  label="O_element : 055"  # scripted group (container) (typed FeaturePython)
  n = 1
  ref = O_element
FEATURE [App::DocumentObjectGroupPython] G4_UREA  # scripted group (container) (typed FeaturePython)
  Dunit = g/cm3
  Dvalue = 1.323
  Group = -> [C_element119,H_element107,N_element046,O_element101]
  conduct = 2
  density = 1
  expand = 3
  formula = G4_UREA
  name = G4_UREA
  specific = 4
FEATURE [App::DocumentObjectGroupPython] C_element120  label="C_element : 067"  # scripted group (container) (typed FeaturePython)
  n = 5
  ref = C_element
FEATURE [App::DocumentObjectGroupPython] H_element108  label="H_element : 058"  # scripted group (container) (typed FeaturePython)
  n = 11
  ref = H_element
FEATURE [App::DocumentObjectGroupPython] N_element047  label="N_element : 020"  # scripted group (container) (typed FeaturePython)
  n = 1
  ref = N_element
FEATURE [App::DocumentObjectGroupPython] O_element102  label="O_element : 056"  # scripted group (container) (typed FeaturePython)
  n = 2
  ref = O_element
FEATURE [App::DocumentObjectGroupPython] G4_VALINE  # scripted group (container) (typed FeaturePython)
  Dunit = g/cm3
  Dvalue = 1.23
  Group = -> [C_element120,H_element108,N_element047,O_element102]
  conduct = 2
  density = 1
  expand = 3
  formula = G4_VALINE
  name = G4_VALINE
  specific = 4
FEATURE [App::DocumentObjectGroupPython] H_element109  label="H_element : 0.009"  # scripted group (container) (typed FeaturePython)
  n = 0.009417
FEATURE [App::DocumentObjectGroupPython] C_element121  label="C_element : 0.281"  # scripted group (container) (typed FeaturePython)
  n = 0.280555
FEATURE [App::DocumentObjectGroupPython] F_element018  label="F_element : 0.710"  # scripted group (container) (typed FeaturePython)
  n = 0.710028
FEATURE [App::DocumentObjectGroupPython] G4_VITON  # scripted group (container) (typed FeaturePython)
  Dunit = g/cm3
  Dvalue = 1.8
  Group = -> [H_element109,C_element121,F_element018]
  conduct = 2
  density = 1
  expand = 3
  formula = G4_VITON
  name = G4_VITON
  specific = 4
FEATURE [App::DocumentObjectGroupPython] H_element110  label="H_element : 059"  # scripted group (container) (typed FeaturePython)
  n = 2
  ref = H_element
FEATURE [App::DocumentObjectGroupPython] O_element103  label="O_element : 057"  # scripted group (container) (typed FeaturePython)
  n = 1
  ref = O_element
FEATURE [App::DocumentObjectGroupPython] G4_WATER  # scripted group (container) (typed FeaturePython)
  Dunit = g/cm3
  Dvalue = 1
  Group = -> [H_element110,O_element103]
  conduct = 2
  density = 1
  expand = 3
  formula = G4_WATER
  name = G4_WATER
  specific = 4
FEATURE [App::DocumentObjectGroupPython] H_element111  label="H_element : 060"  # scripted group (container) (typed FeaturePython)
  n = 2
  ref = H_element
FEATURE [App::DocumentObjectGroupPython] O_element104  label="O_element : 058"  # scripted group (container) (typed FeaturePython)
  n = 1
  ref = O_element
FEATURE [App::DocumentObjectGroupPython] G4_WATER_VAPOR  # scripted group (container) (typed FeaturePython)
  Dunit = g/cm3
  Dvalue = 0.000756182
  Group = -> [H_element111,O_element104]
  conduct = 2
  density = 1
  expand = 3
  formula = G4_WATER_VAPOR
  name = G4_WATER_VAPOR
  specific = 4
FEATURE [App::DocumentObjectGroupPython] C_element122  label="C_element : 068"  # scripted group (container) (typed FeaturePython)
  n = 8
  ref = C_element
FEATURE [App::DocumentObjectGroupPython] H_element112  label="H_element : 061"  # scripted group (container) (typed FeaturePython)
  n = 10
  ref = H_element
FEATURE [App::DocumentObjectGroupPython] G4_XYLENE  # scripted group (container) (typed FeaturePython)
  Dunit = g/cm3
  Dvalue = 0.87
  Group = -> [C_element122,H_element112]
  conduct = 2
  density = 1
  expand = 3
  formula = G4_XYLENE
  name = G4_XYLENE
  specific = 4
FEATURE [App::DocumentObjectGroupPython] C_element123  label="C_element : 069"  # scripted group (container) (typed FeaturePython)
  n = 1
  ref = C_element
FEATURE [App::DocumentObjectGroupPython] G4_GRAPHITE  # scripted group (container) (typed FeaturePython)
  Dunit = g/cm3
  Dvalue = 2.21
  Group = -> [C_element123]
  conduct = 2
  density = 1
  expand = 3
  formula = G4_GRAPHITE
  name = G4_GRAPHITE
  specific = 4
FEATURE [App::DocumentObjectGroupPython] NIST  # scripted group (container) (typed FeaturePython)
  Group = -> [G4_A_150_TISSUE,G4_ACETONE,G4_ACETYLENE,G4_ADENINE,G4_ADIPOSE_TISSUE_ICRP,G4_AIR,G4_ALANINE,G4_ALUMINUM_OXIDE,G4_AMBER,G4_AMMONIA,G4_ANILINE,G4_ANTHRACENE,G4_B_100_BONE,G4_BAKELITE,G4_BARIUM_FLUORIDE,G4_BARIUM_SULFATE,G4_BENZENE,G4_BERYLLIUM_OXIDE,G4_BGO,G4_BLOOD_ICRP,G4_BONE_COMPACT_ICRU,G4_BONE_CORTICAL_ICRP,G4_BORON_CARBIDE,G4_BORON_OXIDE,G4_BRAIN_ICRP,G4_BUTANE,G4_N_BUTYL_ALCOHOL,G4_C_552,+152 more]
FEATURE [App::DocumentObjectGroupPython] H_element113  label="H_element : 062"  # scripted group (container) (typed FeaturePython)
  n = 1
  ref = H_element
FEATURE [App::DocumentObjectGroupPython] G4_H  # scripted group (container) (typed FeaturePython)
  Dunit = g/cm3
  Dvalue = 8.3748e-05
  Group = -> [H_element113]
  conduct = 2
  density = 1
  expand = 3
  formula = H
  name = G4_H
  specific = 4
FEATURE [App::DocumentObjectGroupPython] He_element001  label="He_element : 1"  # scripted group (container) (typed FeaturePython)
  n = 1
  ref = He_element
FEATURE [App::DocumentObjectGroupPython] G4_He  # scripted group (container) (typed FeaturePython)
  Dunit = g/cm3
  Dvalue = 0.000166322
  Group = -> [He_element001]
  conduct = 2
  density = 1
  expand = 3
  formula = He
  name = G4_He
  specific = 4
FEATURE [App::DocumentObjectGroupPython] Li_element008  label="Li_element : 008"  # scripted group (container) (typed FeaturePython)
  n = 1
  ref = Li_element
FEATURE [App::DocumentObjectGroupPython] G4_Li  # scripted group (container) (typed FeaturePython)
  Dunit = g/cm3
  Dvalue = 0.534
  Group = -> [Li_element008]
  conduct = 2
  density = 1
  expand = 3
  formula = Li
  name = G4_Li
  specific = 4
FEATURE [App::DocumentObjectGroupPython] Be_element002  label="Be_element : 002"  # scripted group (container) (typed FeaturePython)
  n = 1
  ref = Be_element
FEATURE [App::DocumentObjectGroupPython] G4_Be  # scripted group (container) (typed FeaturePython)
  Dunit = g/cm3
  Dvalue = 1.848
  Group = -> [Be_element002]
  conduct = 2
  density = 1
  expand = 3
  formula = Be
  name = G4_Be
  specific = 4
FEATURE [App::DocumentObjectGroupPython] B_element007  label="B_element : 007"  # scripted group (container) (typed FeaturePython)
  n = 1
  ref = B_element
FEATURE [App::DocumentObjectGroupPython] G4_B  # scripted group (container) (typed FeaturePython)
  Dunit = g/cm3
  Dvalue = 2.37
  Group = -> [B_element007]
  conduct = 2
  density = 1
  expand = 3
  formula = B
  name = G4_B
  specific = 4
FEATURE [App::DocumentObjectGroupPython] C_element124  label="C_element : 070"  # scripted group (container) (typed FeaturePython)
  n = 1
  ref = C_element
FEATURE [App::DocumentObjectGroupPython] G4_C  # scripted group (container) (typed FeaturePython)
  Dunit = g/cm3
  Dvalue = 2
  Group = -> [C_element124]
  conduct = 2
  density = 1
  expand = 3
  formula = C
  name = G4_C
  specific = 4
FEATURE [App::DocumentObjectGroupPython] N_element048  label="N_element : 021"  # scripted group (container) (typed FeaturePython)
  n = 1
  ref = N_element
FEATURE [App::DocumentObjectGroupPython] G4_N  # scripted group (container) (typed FeaturePython)
  Dunit = g/cm3
  Dvalue = 0.0011652
  Group = -> [N_element048]
  conduct = 2
  density = 1
  expand = 3
  formula = N
  name = G4_N
  specific = 4
FEATURE [App::DocumentObjectGroupPython] O_element105  label="O_element : 059"  # scripted group (container) (typed FeaturePython)
  n = 1
  ref = O_element
FEATURE [App::DocumentObjectGroupPython] G4_O  # scripted group (container) (typed FeaturePython)
  Dunit = g/cm3
  Dvalue = 0.00133151
  Group = -> [O_element105]
  conduct = 2
  density = 1
  expand = 3
  formula = O
  name = G4_O
  specific = 4
FEATURE [App::DocumentObjectGroupPython] F_element019  label="F_element : 008"  # scripted group (container) (typed FeaturePython)
  n = 1
  ref = F_element
FEATURE [App::DocumentObjectGroupPython] G4_F  # scripted group (container) (typed FeaturePython)
  Dunit = g/cm3
  Dvalue = 0.00158029
  Group = -> [F_element019]
  conduct = 2
  density = 1
  expand = 3
  formula = F
  name = G4_F
  specific = 4
FEATURE [App::DocumentObjectGroupPython] Ne_element001  label="Ne_element : 1"  # scripted group (container) (typed FeaturePython)
  n = 1
  ref = Ne_element
FEATURE [App::DocumentObjectGroupPython] G4_Ne  # scripted group (container) (typed FeaturePython)
  Dunit = g/cm3
  Dvalue = 0.000838505
  Group = -> [Ne_element001]
  conduct = 2
  density = 1
  expand = 3
  formula = Ne
  name = G4_Ne
  specific = 4
FEATURE [App::DocumentObjectGroupPython] Na_element020  label="Na_element : 005"  # scripted group (container) (typed FeaturePython)
  n = 1
  ref = Na_element
FEATURE [App::DocumentObjectGroupPython] G4_Na  # scripted group (container) (typed FeaturePython)
  Dunit = g/cm3
  Dvalue = 0.971
  Group = -> [Na_element020]
  conduct = 2
  density = 1
  expand = 3
  formula = Na
  name = G4_Na
  specific = 4
FEATURE [App::DocumentObjectGroupPython] Mg_element011  label="Mg_element : 005"  # scripted group (container) (typed FeaturePython)
  n = 1
  ref = Mg_element
FEATURE [App::DocumentObjectGroupPython] G4_Mg  # scripted group (container) (typed FeaturePython)
  Dunit = g/cm3
  Dvalue = 1.74
  Group = -> [Mg_element011]
  conduct = 2
  density = 1
  expand = 3
  formula = Mg
  name = G4_Mg
  specific = 4
FEATURE [App::DocumentObjectGroupPython] Al_element004  label="Al_element : 1"  # scripted group (container) (typed FeaturePython)
  n = 1
  ref = Al_element
FEATURE [App::DocumentObjectGroupPython] G4_Al  # scripted group (container) (typed FeaturePython)
  Dunit = g/cm3
  Dvalue = 2.699
  Group = -> [Al_element004]
  conduct = 2
  density = 1
  expand = 3
  formula = Al
  name = G4_Al
  specific = 4
FEATURE [App::DocumentObjectGroupPython] Si_element007  label="Si_element : 002"  # scripted group (container) (typed FeaturePython)
  n = 1
  ref = Si_element
FEATURE [App::DocumentObjectGroupPython] G4_Si  # scripted group (container) (typed FeaturePython)
  Dunit = g/cm3
  Dvalue = 2.33
  Group = -> [Si_element007]
  conduct = 2
  density = 1
  expand = 3
  formula = Si
  name = G4_Si
  specific = 4
FEATURE [App::DocumentObjectGroupPython] P_element013  label="P_element : 002"  # scripted group (container) (typed FeaturePython)
  n = 1
  ref = P_element
FEATURE [App::DocumentObjectGroupPython] G4_P  # scripted group (container) (typed FeaturePython)
  Dunit = g/cm3
  Dvalue = 2.2
  Group = -> [P_element013]
  conduct = 2
  density = 1
  expand = 3
  formula = P
  name = G4_P
  specific = 4
FEATURE [App::DocumentObjectGroupPython] S_element023  label="S_element : 007"  # scripted group (container) (typed FeaturePython)
  n = 1
  ref = S_element
FEATURE [App::DocumentObjectGroupPython] G4_S  # scripted group (container) (typed FeaturePython)
  Dunit = g/cm3
  Dvalue = 2
  Group = -> [S_element023]
  conduct = 2
  density = 1
  expand = 3
  formula = S
  name = G4_S
  specific = 4
FEATURE [App::DocumentObjectGroupPython] Cl_element029  label="Cl_element : 015"  # scripted group (container) (typed FeaturePython)
  n = 1
  ref = Cl_element
FEATURE [App::DocumentObjectGroupPython] G4_Cl  # scripted group (container) (typed FeaturePython)
  Dunit = g/cm3
  Dvalue = 0.00299473
  Group = -> [Cl_element029]
  conduct = 2
  density = 1
  expand = 3
  formula = Cl
  name = G4_Cl
  specific = 4
FEATURE [App::DocumentObjectGroupPython] Ar_element002  label="Ar_element : 1"  # scripted group (container) (typed FeaturePython)
  n = 1
  ref = Ar_element
FEATURE [App::DocumentObjectGroupPython] G4_Ar  # scripted group (container) (typed FeaturePython)
  Dunit = g/cm3
  Dvalue = 0.00166201
  Group = -> [Ar_element002]
  conduct = 2
  density = 1
  expand = 3
  formula = Ar
  name = G4_Ar
  specific = 4
FEATURE [App::DocumentObjectGroupPython] K_element013  label="K_element : 003"  # scripted group (container) (typed FeaturePython)
  n = 1
  ref = K_element
FEATURE [App::DocumentObjectGroupPython] G4_K  # scripted group (container) (typed FeaturePython)
  Dunit = g/cm3
  Dvalue = 0.862
  Group = -> [K_element013]
  conduct = 2
  density = 1
  expand = 3
  formula = K
  name = G4_K
  specific = 4
FEATURE [App::DocumentObjectGroupPython] Ca_element014  label="Ca_element : 007"  # scripted group (container) (typed FeaturePython)
  n = 1
  ref = Ca_element
FEATURE [App::DocumentObjectGroupPython] G4_Ca  # scripted group (container) (typed FeaturePython)
  Dunit = g/cm3
  Dvalue = 1.55
  Group = -> [Ca_element014]
  conduct = 2
  density = 1
  expand = 3
  formula = Ca
  name = G4_Ca
  specific = 4
FEATURE [App::DocumentObjectGroupPython] Sc_element001  label="Sc_element : 1"  # scripted group (container) (typed FeaturePython)
  n = 1
  ref = Sc_element
FEATURE [App::DocumentObjectGroupPython] G4_Sc  # scripted group (container) (typed FeaturePython)
  Dunit = g/cm3
  Dvalue = 2.989
  Group = -> [Sc_element001]
  conduct = 2
  density = 1
  expand = 3
  formula = Sc
  name = G4_Sc
  specific = 4
FEATURE [App::DocumentObjectGroupPython] Ti_element004  label="Ti_element : 002"  # scripted group (container) (typed FeaturePython)
  n = 1
  ref = Ti_element
FEATURE [App::DocumentObjectGroupPython] G4_Ti  # scripted group (container) (typed FeaturePython)
  Dunit = g/cm3
  Dvalue = 4.54
  Group = -> [Ti_element004]
  conduct = 2
  density = 1
  expand = 3
  formula = Ti
  name = G4_Ti
  specific = 4
FEATURE [App::DocumentObjectGroupPython] V_element001  label="V_element : 1"  # scripted group (container) (typed FeaturePython)
  n = 1
  ref = V_element
FEATURE [App::DocumentObjectGroupPython] G4_V  # scripted group (container) (typed FeaturePython)
  Dunit = g/cm3
  Dvalue = 6.11
  Group = -> [V_element001]
  conduct = 2
  density = 1
  expand = 3
  formula = V
  name = G4_V
  specific = 4
FEATURE [App::DocumentObjectGroupPython] Cr_element001  label="Cr_element : 1"  # scripted group (container) (typed FeaturePython)
  n = 1
  ref = Cr_element
FEATURE [App::DocumentObjectGroupPython] G4_Cr  # scripted group (container) (typed FeaturePython)
  Dunit = g/cm3
  Dvalue = 7.18
  Group = -> [Cr_element001]
  conduct = 2
  density = 1
  expand = 3
  formula = Cr
  name = G4_Cr
  specific = 4
FEATURE [App::DocumentObjectGroupPython] Mn_element001  label="Mn_element : 1"  # scripted group (container) (typed FeaturePython)
  n = 1
  ref = Mn_element
FEATURE [App::DocumentObjectGroupPython] G4_Mn  # scripted group (container) (typed FeaturePython)
  Dunit = g/cm3
  Dvalue = 7.44
  Group = -> [Mn_element001]
  conduct = 2
  density = 1
  expand = 3
  formula = Mn
  name = G4_Mn
  specific = 4
FEATURE [App::DocumentObjectGroupPython] Fe_element007  label="Fe_element : 004"  # scripted group (container) (typed FeaturePython)
  n = 1
  ref = Fe_element
FEATURE [App::DocumentObjectGroupPython] G4_Fe  # scripted group (container) (typed FeaturePython)
  Dunit = g/cm3
  Dvalue = 7.874
  Group = -> [Fe_element007]
  conduct = 2
  density = 1
  expand = 3
  formula = Fe
  name = G4_Fe
  specific = 4
FEATURE [App::DocumentObjectGroupPython] Co_element001  label="Co_element : 1"  # scripted group (container) (typed FeaturePython)
  n = 1
  ref = Co_element
FEATURE [App::DocumentObjectGroupPython] G4_Co  # scripted group (container) (typed FeaturePython)
  Dunit = g/cm3
  Dvalue = 8.9
  Group = -> [Co_element001]
  conduct = 2
  density = 1
  expand = 3
  formula = Co
  name = G4_Co
  specific = 4
FEATURE [App::DocumentObjectGroupPython] Ni_element001  label="Ni_element : 1"  # scripted group (container) (typed FeaturePython)
  n = 1
  ref = Ni_element
FEATURE [App::DocumentObjectGroupPython] G4_Ni  # scripted group (container) (typed FeaturePython)
  Dunit = g/cm3
  Dvalue = 8.902
  Group = -> [Ni_element001]
  conduct = 2
  density = 1
  expand = 3
  formula = Ni
  name = G4_Ni
  specific = 4
FEATURE [App::DocumentObjectGroupPython] Cu_element001  label="Cu_element : 1"  # scripted group (container) (typed FeaturePython)
  n = 1
  ref = Cu_element
FEATURE [App::DocumentObjectGroupPython] G4_Cu  # scripted group (container) (typed FeaturePython)
  Dunit = g/cm3
  Dvalue = 8.96
  Group = -> [Cu_element001]
  conduct = 2
  density = 1
  expand = 3
  formula = Cu
  name = G4_Cu
  specific = 4
FEATURE [App::DocumentObjectGroupPython] Zn_element001  label="Zn_element : 1"  # scripted group (container) (typed FeaturePython)
  n = 1
  ref = Zn_element
FEATURE [App::DocumentObjectGroupPython] G4_Zn  # scripted group (container) (typed FeaturePython)
  Dunit = g/cm3
  Dvalue = 7.133
  Group = -> [Zn_element001]
  conduct = 2
  density = 1
  expand = 3
  formula = Zn
  name = G4_Zn
  specific = 4
FEATURE [App::DocumentObjectGroupPython] Ga_element002  label="Ga_element : 002"  # scripted group (container) (typed FeaturePython)
  n = 1
  ref = Ga_element
FEATURE [App::DocumentObjectGroupPython] G4_Ga  # scripted group (container) (typed FeaturePython)
  Dunit = g/cm3
  Dvalue = 5.904
  Group = -> [Ga_element002]
  conduct = 2
  density = 1
  expand = 3
  formula = Ga
  name = G4_Ga
  specific = 4
FEATURE [App::DocumentObjectGroupPython] Ge_element002  label="Ge_element : 1"  # scripted group (container) (typed FeaturePython)
  n = 1
  ref = Ge_element
FEATURE [App::DocumentObjectGroupPython] G4_Ge  # scripted group (container) (typed FeaturePython)
  Dunit = g/cm3
  Dvalue = 5.323
  Group = -> [Ge_element002]
  conduct = 2
  density = 1
  expand = 3
  formula = Ge
  name = G4_Ge
  specific = 4
FEATURE [App::DocumentObjectGroupPython] As_element003  label="As_element : 002"  # scripted group (container) (typed FeaturePython)
  n = 1
  ref = As_element
FEATURE [App::DocumentObjectGroupPython] G4_As  # scripted group (container) (typed FeaturePython)
  Dunit = g/cm3
  Dvalue = 5.73
  Group = -> [As_element003]
  conduct = 2
  density = 1
  expand = 3
  formula = As
  name = G4_As
  specific = 4
FEATURE [App::DocumentObjectGroupPython] Se_element001  label="Se_element : 1"  # scripted group (container) (typed FeaturePython)
  n = 1
  ref = Se_element
FEATURE [App::DocumentObjectGroupPython] G4_Se  # scripted group (container) (typed FeaturePython)
  Dunit = g/cm3
  Dvalue = 4.5
  Group = -> [Se_element001]
  conduct = 2
  density = 1
  expand = 3
  formula = Se
  name = G4_Se
  specific = 4
FEATURE [App::DocumentObjectGroupPython] Br_element007  label="Br_element : 004"  # scripted group (container) (typed FeaturePython)
  n = 1
  ref = Br_element
FEATURE [App::DocumentObjectGroupPython] G4_Br  # scripted group (container) (typed FeaturePython)
  Dunit = g/cm3
  Dvalue = 0.0070721
  Group = -> [Br_element007]
  conduct = 2
  density = 1
  expand = 3
  formula = Br
  name = G4_Br
  specific = 4
FEATURE [App::DocumentObjectGroupPython] Kr_element001  label="Kr_element : 1"  # scripted group (container) (typed FeaturePython)
  n = 1
  ref = Kr_element
FEATURE [App::DocumentObjectGroupPython] G4_Kr  # scripted group (container) (typed FeaturePython)
  Dunit = g/cm3
  Dvalue = 0.00347832
  Group = -> [Kr_element001]
  conduct = 2
  density = 1
  expand = 3
  formula = Kr
  name = G4_Kr
  specific = 4
FEATURE [App::DocumentObjectGroupPython] Rb_element001  label="Rb_element : 1"  # scripted group (container) (typed FeaturePython)
  n = 1
  ref = Rb_element
FEATURE [App::DocumentObjectGroupPython] G4_Rb  # scripted group (container) (typed FeaturePython)
  Dunit = g/cm3
  Dvalue = 1.532
  Group = -> [Rb_element001]
  conduct = 2
  density = 1
  expand = 3
  formula = Rb
  name = G4_Rb
  specific = 4
FEATURE [App::DocumentObjectGroupPython] Sr_element001  label="Sr_element : 1"  # scripted group (container) (typed FeaturePython)
  n = 1
  ref = Sr_element
FEATURE [App::DocumentObjectGroupPython] G4_Sr  # scripted group (container) (typed FeaturePython)
  Dunit = g/cm3
  Dvalue = 2.54
  Group = -> [Sr_element001]
  conduct = 2
  density = 1
  expand = 3
  formula = Sr
  name = G4_Sr
  specific = 4
FEATURE [App::DocumentObjectGroupPython] Y_element001  label="Y_element : 1"  # scripted group (container) (typed FeaturePython)
  n = 1
  ref = Y_element
FEATURE [App::DocumentObjectGroupPython] G4_Y  # scripted group (container) (typed FeaturePython)
  Dunit = g/cm3
  Dvalue = 4.469
  Group = -> [Y_element001]
  conduct = 2
  density = 1
  expand = 3
  formula = Y
  name = G4_Y
  specific = 4
FEATURE [App::DocumentObjectGroupPython] Zr_element001  label="Zr_element : 1"  # scripted group (container) (typed FeaturePython)
  n = 1
  ref = Zr_element
FEATURE [App::DocumentObjectGroupPython] G4_Zr  # scripted group (container) (typed FeaturePython)
  Dunit = g/cm3
  Dvalue = 6.506
  Group = -> [Zr_element001]
  conduct = 2
  density = 1
  expand = 3
  formula = Zr
  name = G4_Zr
  specific = 4
FEATURE [App::DocumentObjectGroupPython] Nb_element001  label="Nb_element : 1"  # scripted group (container) (typed FeaturePython)
  n = 1
  ref = Nb_element
FEATURE [App::DocumentObjectGroupPython] G4_Nb  # scripted group (container) (typed FeaturePython)
  Dunit = g/cm3
  Dvalue = 8.57
  Group = -> [Nb_element001]
  conduct = 2
  density = 1
  expand = 3
  formula = Nb
  name = G4_Nb
  specific = 4
FEATURE [App::DocumentObjectGroupPython] Mo_element001  label="Mo_element : 1"  # scripted group (container) (typed FeaturePython)
  n = 1
  ref = Mo_element
FEATURE [App::DocumentObjectGroupPython] G4_Mo  # scripted group (container) (typed FeaturePython)
  Dunit = g/cm3
  Dvalue = 10.22
  Group = -> [Mo_element001]
  conduct = 2
  density = 1
  expand = 3
  formula = Mo
  name = G4_Mo
  specific = 4
FEATURE [App::DocumentObjectGroupPython] Tc_element001  label="Tc_element : 1"  # scripted group (container) (typed FeaturePython)
  n = 1
  ref = Tc_element
FEATURE [App::DocumentObjectGroupPython] G4_Tc  # scripted group (container) (typed FeaturePython)
  Dunit = g/cm3
  Dvalue = 11.5
  Group = -> [Tc_element001]
  conduct = 2
  density = 1
  expand = 3
  formula = Tc
  name = G4_Tc
  specific = 4
FEATURE [App::DocumentObjectGroupPython] Ru_element001  label="Ru_element : 1"  # scripted group (container) (typed FeaturePython)
  n = 1
  ref = Ru_element
FEATURE [App::DocumentObjectGroupPython] G4_Ru  # scripted group (container) (typed FeaturePython)
  Dunit = g/cm3
  Dvalue = 12.41
  Group = -> [Ru_element001]
  conduct = 2
  density = 1
  expand = 3
  formula = Ru
  name = G4_Ru
  specific = 4
FEATURE [App::DocumentObjectGroupPython] Rh_element001  label="Rh_element : 1"  # scripted group (container) (typed FeaturePython)
  n = 1
  ref = Rh_element
FEATURE [App::DocumentObjectGroupPython] G4_Rh  # scripted group (container) (typed FeaturePython)
  Dunit = g/cm3
  Dvalue = 12.41
  Group = -> [Rh_element001]
  conduct = 2
  density = 1
  expand = 3
  formula = Rh
  name = G4_Rh
  specific = 4
FEATURE [App::DocumentObjectGroupPython] Pd_element001  label="Pd_element : 1"  # scripted group (container) (typed FeaturePython)
  n = 1
  ref = Pd_element
FEATURE [App::DocumentObjectGroupPython] G4_Pd  # scripted group (container) (typed FeaturePython)
  Dunit = g/cm3
  Dvalue = 12.02
  Group = -> [Pd_element001]
  conduct = 2
  density = 1
  expand = 3
  formula = Pd
  name = G4_Pd
  specific = 4
FEATURE [App::DocumentObjectGroupPython] Ag_element006  label="Ag_element : 004"  # scripted group (container) (typed FeaturePython)
  n = 1
  ref = Ag_element
FEATURE [App::DocumentObjectGroupPython] G4_Ag  # scripted group (container) (typed FeaturePython)
  Dunit = g/cm3
  Dvalue = 10.5
  Group = -> [Ag_element006]
  conduct = 2
  density = 1
  expand = 3
  formula = Ag
  name = G4_Ag
  specific = 4
FEATURE [App::DocumentObjectGroupPython] Cd_element003  label="Cd_element : 003"  # scripted group (container) (typed FeaturePython)
  n = 1
  ref = Cd_element
FEATURE [App::DocumentObjectGroupPython] G4_Cd  # scripted group (container) (typed FeaturePython)
  Dunit = g/cm3
  Dvalue = 8.65
  Group = -> [Cd_element003]
  conduct = 2
  density = 1
  expand = 3
  formula = Cd
  name = G4_Cd
  specific = 4
FEATURE [App::DocumentObjectGroupPython] In_element001  label="In_element : 1"  # scripted group (container) (typed FeaturePython)
  n = 1
  ref = In_element
FEATURE [App::DocumentObjectGroupPython] G4_In  # scripted group (container) (typed FeaturePython)
  Dunit = g/cm3
  Dvalue = 7.31
  Group = -> [In_element001]
  conduct = 2
  density = 1
  expand = 3
  formula = In
  name = G4_In
  specific = 4
FEATURE [App::DocumentObjectGroupPython] Sn_element001  label="Sn_element : 1"  # scripted group (container) (typed FeaturePython)
  n = 1
  ref = Sn_element
FEATURE [App::DocumentObjectGroupPython] G4_Sn  # scripted group (container) (typed FeaturePython)
  Dunit = g/cm3
  Dvalue = 7.31
  Group = -> [Sn_element001]
  conduct = 2
  density = 1
  expand = 3
  formula = Sn
  name = G4_Sn
  specific = 4
FEATURE [App::DocumentObjectGroupPython] Sb_element001  label="Sb_element : 1"  # scripted group (container) (typed FeaturePython)
  n = 1
  ref = Sb_element
FEATURE [App::DocumentObjectGroupPython] G4_Sb  # scripted group (container) (typed FeaturePython)
  Dunit = g/cm3
  Dvalue = 6.691
  Group = -> [Sb_element001]
  conduct = 2
  density = 1
  expand = 3
  formula = Sb
  name = G4_Sb
  specific = 4
FEATURE [App::DocumentObjectGroupPython] Te_element002  label="Te_element : 002"  # scripted group (container) (typed FeaturePython)
  n = 1
  ref = Te_element
FEATURE [App::DocumentObjectGroupPython] G4_Te  # scripted group (container) (typed FeaturePython)
  Dunit = g/cm3
  Dvalue = 6.24
  Group = -> [Te_element002]
  conduct = 2
  density = 1
  expand = 3
  formula = Te
  name = G4_Te
  specific = 4
FEATURE [App::DocumentObjectGroupPython] I_element010  label="I_element : 006"  # scripted group (container) (typed FeaturePython)
  n = 1
  ref = I_element
FEATURE [App::DocumentObjectGroupPython] G4_I  # scripted group (container) (typed FeaturePython)
  Dunit = g/cm3
  Dvalue = 4.93
  Group = -> [I_element010]
  conduct = 2
  density = 1
  expand = 3
  formula = I
  name = G4_I
  specific = 4
FEATURE [App::DocumentObjectGroupPython] Xe_element001  label="Xe_element : 1"  # scripted group (container) (typed FeaturePython)
  n = 1
  ref = Xe_element
FEATURE [App::DocumentObjectGroupPython] G4_Xe  # scripted group (container) (typed FeaturePython)
  Dunit = g/cm3
  Dvalue = 0.00548536
  Group = -> [Xe_element001]
  conduct = 2
  density = 1
  expand = 3
  formula = Xe
  name = G4_Xe
  specific = 4
FEATURE [App::DocumentObjectGroupPython] Cs_element003  label="Cs_element : 003"  # scripted group (container) (typed FeaturePython)
  n = 1
  ref = Cs_element
FEATURE [App::DocumentObjectGroupPython] G4_Cs  # scripted group (container) (typed FeaturePython)
  Dunit = g/cm3
  Dvalue = 1.873
  Group = -> [Cs_element003]
  conduct = 2
  density = 1
  expand = 3
  formula = Cs
  name = G4_Cs
  specific = 4
FEATURE [App::DocumentObjectGroupPython] Ba_element003  label="Ba_element : 003"  # scripted group (container) (typed FeaturePython)
  n = 1
  ref = Ba_element
FEATURE [App::DocumentObjectGroupPython] G4_Ba  # scripted group (container) (typed FeaturePython)
  Dunit = g/cm3
  Dvalue = 3.5
  Group = -> [Ba_element003]
  conduct = 2
  density = 1
  expand = 3
  formula = Ba
  name = G4_Ba
  specific = 4
FEATURE [App::DocumentObjectGroupPython] La_element003  label="La_element : 003"  # scripted group (container) (typed FeaturePython)
  n = 1
  ref = La_element
FEATURE [App::DocumentObjectGroupPython] G4_La  # scripted group (container) (typed FeaturePython)
  Dunit = g/cm3
  Dvalue = 6.154
  Group = -> [La_element003]
  conduct = 2
  density = 1
  expand = 3
  formula = La
  name = G4_La
  specific = 4
FEATURE [App::DocumentObjectGroupPython] Ce_element002  label="Ce_element : 1"  # scripted group (container) (typed FeaturePython)
  n = 1
  ref = Ce_element
FEATURE [App::DocumentObjectGroupPython] G4_Ce  # scripted group (container) (typed FeaturePython)
  Dunit = g/cm3
  Dvalue = 6.657
  Group = -> [Ce_element002]
  conduct = 2
  density = 1
  expand = 3
  formula = Ce
  name = G4_Ce
  specific = 4
FEATURE [App::DocumentObjectGroupPython] Pr_element001  label="Pr_element : 1"  # scripted group (container) (typed FeaturePython)
  n = 1
  ref = Pr_element
FEATURE [App::DocumentObjectGroupPython] G4_Pr  # scripted group (container) (typed FeaturePython)
  Dunit = g/cm3
  Dvalue = 6.71
  Group = -> [Pr_element001]
  conduct = 2
  density = 1
  expand = 3
  formula = Pr
  name = G4_Pr
  specific = 4
FEATURE [App::DocumentObjectGroupPython] Nd_element001  label="Nd_element : 1"  # scripted group (container) (typed FeaturePython)
  n = 1
  ref = Nd_element
FEATURE [App::DocumentObjectGroupPython] G4_Nd  # scripted group (container) (typed FeaturePython)
  Dunit = g/cm3
  Dvalue = 6.9
  Group = -> [Nd_element001]
  conduct = 2
  density = 1
  expand = 3
  formula = Nd
  name = G4_Nd
  specific = 4
FEATURE [App::DocumentObjectGroupPython] Pm_element001  label="Pm_element : 1"  # scripted group (container) (typed FeaturePython)
  n = 1
  ref = Pm_element
FEATURE [App::DocumentObjectGroupPython] G4_Pm  # scripted group (container) (typed FeaturePython)
  Dunit = g/cm3
  Dvalue = 7.22
  Group = -> [Pm_element001]
  conduct = 2
  density = 1
  expand = 3
  formula = Pm
  name = G4_Pm
  specific = 4
FEATURE [App::DocumentObjectGroupPython] Sm_element001  label="Sm_element : 1"  # scripted group (container) (typed FeaturePython)
  n = 1
  ref = Sm_element
FEATURE [App::DocumentObjectGroupPython] G4_Sm  # scripted group (container) (typed FeaturePython)
  Dunit = g/cm3
  Dvalue = 7.46
  Group = -> [Sm_element001]
  conduct = 2
  density = 1
  expand = 3
  formula = Sm
  name = G4_Sm
  specific = 4
FEATURE [App::DocumentObjectGroupPython] Eu_element001  label="Eu_element : 1"  # scripted group (container) (typed FeaturePython)
  n = 1
  ref = Eu_element
FEATURE [App::DocumentObjectGroupPython] G4_Eu  # scripted group (container) (typed FeaturePython)
  Dunit = g/cm3
  Dvalue = 5.243
  Group = -> [Eu_element001]
  conduct = 2
  density = 1
  expand = 3
  formula = Eu
  name = G4_Eu
  specific = 4
FEATURE [App::DocumentObjectGroupPython] Gd_element002  label="Gd_element : 1"  # scripted group (container) (typed FeaturePython)
  n = 1
  ref = Gd_element
FEATURE [App::DocumentObjectGroupPython] G4_Gd  # scripted group (container) (typed FeaturePython)
  Dunit = g/cm3
  Dvalue = 7.9004
  Group = -> [Gd_element002]
  conduct = 2
  density = 1
  expand = 3
  formula = Gd
  name = G4_Gd
  specific = 4
FEATURE [App::DocumentObjectGroupPython] Tb_element001  label="Tb_element : 1"  # scripted group (container) (typed FeaturePython)
  n = 1
  ref = Tb_element
FEATURE [App::DocumentObjectGroupPython] G4_Tb  # scripted group (container) (typed FeaturePython)
  Dunit = g/cm3
  Dvalue = 8.229
  Group = -> [Tb_element001]
  conduct = 2
  density = 1
  expand = 3
  formula = Tb
  name = G4_Tb
  specific = 4
FEATURE [App::DocumentObjectGroupPython] Dy_element001  label="Dy_element : 1"  # scripted group (container) (typed FeaturePython)
  n = 1
  ref = Dy_element
FEATURE [App::DocumentObjectGroupPython] G4_Dy  # scripted group (container) (typed FeaturePython)
  Dunit = g/cm3
  Dvalue = 8.55
  Group = -> [Dy_element001]
  conduct = 2
  density = 1
  expand = 3
  formula = Dy
  name = G4_Dy
  specific = 4
FEATURE [App::DocumentObjectGroupPython] Ho_element001  label="Ho_element : 1"  # scripted group (container) (typed FeaturePython)
  n = 1
  ref = Ho_element
FEATURE [App::DocumentObjectGroupPython] G4_Ho  # scripted group (container) (typed FeaturePython)
  Dunit = g/cm3
  Dvalue = 8.795
  Group = -> [Ho_element001]
  conduct = 2
  density = 1
  expand = 3
  formula = Ho
  name = G4_Ho
  specific = 4
FEATURE [App::DocumentObjectGroupPython] Er_element001  label="Er_element : 1"  # scripted group (container) (typed FeaturePython)
  n = 1
  ref = Er_element
FEATURE [App::DocumentObjectGroupPython] G4_Er  # scripted group (container) (typed FeaturePython)
  Dunit = g/cm3
  Dvalue = 9.066
  Group = -> [Er_element001]
  conduct = 2
  density = 1
  expand = 3
  formula = Er
  name = G4_Er
  specific = 4
FEATURE [App::DocumentObjectGroupPython] Tm_element001  label="Tm_element : 1"  # scripted group (container) (typed FeaturePython)
  n = 1
  ref = Tm_element
FEATURE [App::DocumentObjectGroupPython] G4_Tm  # scripted group (container) (typed FeaturePython)
  Dunit = g/cm3
  Dvalue = 9.321
  Group = -> [Tm_element001]
  conduct = 2
  density = 1
  expand = 3
  formula = Tm
  name = G4_Tm
  specific = 4
FEATURE [App::DocumentObjectGroupPython] Yb_element001  label="Yb_element : 1"  # scripted group (container) (typed FeaturePython)
  n = 1
  ref = Yb_element
FEATURE [App::DocumentObjectGroupPython] G4_Yb  # scripted group (container) (typed FeaturePython)
  Dunit = g/cm3
  Dvalue = 6.73
  Group = -> [Yb_element001]
  conduct = 2
  density = 1
  expand = 3
  formula = Yb
  name = G4_Yb
  specific = 4
FEATURE [App::DocumentObjectGroupPython] Lu_element001  label="Lu_element : 1"  # scripted group (container) (typed FeaturePython)
  n = 1
  ref = Lu_element
FEATURE [App::DocumentObjectGroupPython] G4_Lu  # scripted group (container) (typed FeaturePython)
  Dunit = g/cm3
  Dvalue = 9.84
  Group = -> [Lu_element001]
  conduct = 2
  density = 1
  expand = 3
  formula = Lu
  name = G4_Lu
  specific = 4
FEATURE [App::DocumentObjectGroupPython] Hf_element001  label="Hf_element : 1"  # scripted group (container) (typed FeaturePython)
  n = 1
  ref = Hf_element
FEATURE [App::DocumentObjectGroupPython] G4_Hf  # scripted group (container) (typed FeaturePython)
  Dunit = g/cm3
  Dvalue = 13.31
  Group = -> [Hf_element001]
  conduct = 2
  density = 1
  expand = 3
  formula = Hf
  name = G4_Hf
  specific = 4
FEATURE [App::DocumentObjectGroupPython] Ta_element001  label="Ta_element : 1"  # scripted group (container) (typed FeaturePython)
  n = 1
  ref = Ta_element
FEATURE [App::DocumentObjectGroupPython] G4_Ta  # scripted group (container) (typed FeaturePython)
  Dunit = g/cm3
  Dvalue = 16.654
  Group = -> [Ta_element001]
  conduct = 2
  density = 1
  expand = 3
  formula = Ta
  name = G4_Ta
  specific = 4
FEATURE [App::DocumentObjectGroupPython] W_element004  label="W_element : 004"  # scripted group (container) (typed FeaturePython)
  n = 1
  ref = W_element
FEATURE [App::DocumentObjectGroupPython] G4_W  # scripted group (container) (typed FeaturePython)
  Dunit = g/cm3
  Dvalue = 19.3
  Group = -> [W_element004]
  conduct = 2
  density = 1
  expand = 3
  formula = W
  name = G4_W
  specific = 4
FEATURE [App::DocumentObjectGroupPython] Re_element001  label="Re_element : 1"  # scripted group (container) (typed FeaturePython)
  n = 1
  ref = Re_element
FEATURE [App::DocumentObjectGroupPython] G4_Re  # scripted group (container) (typed FeaturePython)
  Dunit = g/cm3
  Dvalue = 21.02
  Group = -> [Re_element001]
  conduct = 2
  density = 1
  expand = 3
  formula = Re
  name = G4_Re
  specific = 4
FEATURE [App::DocumentObjectGroupPython] Os_element001  label="Os_element : 1"  # scripted group (container) (typed FeaturePython)
  n = 1
  ref = Os_element
FEATURE [App::DocumentObjectGroupPython] G4_Os  # scripted group (container) (typed FeaturePython)
  Dunit = g/cm3
  Dvalue = 22.57
  Group = -> [Os_element001]
  conduct = 2
  density = 1
  expand = 3
  formula = Os
  name = G4_Os
  specific = 4
FEATURE [App::DocumentObjectGroupPython] Ir_element001  label="Ir_element : 1"  # scripted group (container) (typed FeaturePython)
  n = 1
  ref = Ir_element
FEATURE [App::DocumentObjectGroupPython] G4_Ir  # scripted group (container) (typed FeaturePython)
  Dunit = g/cm3
  Dvalue = 22.42
  Group = -> [Ir_element001]
  conduct = 2
  density = 1
  expand = 3
  formula = Ir
  name = G4_Ir
  specific = 4
FEATURE [App::DocumentObjectGroupPython] Pt_element001  label="Pt_element : 1"  # scripted group (container) (typed FeaturePython)
  n = 1
  ref = Pt_element
FEATURE [App::DocumentObjectGroupPython] G4_Pt  # scripted group (container) (typed FeaturePython)
  Dunit = g/cm3
  Dvalue = 21.45
  Group = -> [Pt_element001]
  conduct = 2
  density = 1
  expand = 3
  formula = Pt
  name = G4_Pt
  specific = 4
FEATURE [App::DocumentObjectGroupPython] Au_element001  label="Au_element : 1"  # scripted group (container) (typed FeaturePython)
  n = 1
  ref = Au_element
FEATURE [App::DocumentObjectGroupPython] G4_Au  # scripted group (container) (typed FeaturePython)
  Dunit = g/cm3
  Dvalue = 19.32
  Group = -> [Au_element001]
  conduct = 2
  density = 1
  expand = 3
  formula = Au
  name = G4_Au
  specific = 4
FEATURE [App::DocumentObjectGroupPython] Hg_element002  label="Hg_element : 002"  # scripted group (container) (typed FeaturePython)
  n = 1
  ref = Hg_element
FEATURE [App::DocumentObjectGroupPython] G4_Hg  # scripted group (container) (typed FeaturePython)
  Dunit = g/cm3
  Dvalue = 13.546
  Group = -> [Hg_element002]
  conduct = 2
  density = 1
  expand = 3
  formula = Hg
  name = G4_Hg
  specific = 4
FEATURE [App::DocumentObjectGroupPython] Tl_element002  label="Tl_element : 002"  # scripted group (container) (typed FeaturePython)
  n = 1
  ref = Tl_element
FEATURE [App::DocumentObjectGroupPython] G4_Tl  # scripted group (container) (typed FeaturePython)
  Dunit = g/cm3
  Dvalue = 11.72
  Group = -> [Tl_element002]
  conduct = 2
  density = 1
  expand = 3
  formula = Tl
  name = G4_Tl
  specific = 4
FEATURE [App::DocumentObjectGroupPython] Pb_element003  label="Pb_element : 1"  # scripted group (container) (typed FeaturePython)
  n = 1
  ref = Pb_element
FEATURE [App::DocumentObjectGroupPython] G4_Pb  # scripted group (container) (typed FeaturePython)
  Dunit = g/cm3
  Dvalue = 11.35
  Group = -> [Pb_element003]
  conduct = 2
  density = 1
  expand = 3
  formula = Pb
  name = G4_Pb
  specific = 4
FEATURE [App::DocumentObjectGroupPython] Bi_element002  label="Bi_element : 1"  # scripted group (container) (typed FeaturePython)
  n = 1
  ref = Bi_element
FEATURE [App::DocumentObjectGroupPython] G4_Bi  # scripted group (container) (typed FeaturePython)
  Dunit = g/cm3
  Dvalue = 9.747
  Group = -> [Bi_element002]
  conduct = 2
  density = 1
  expand = 3
  formula = Bi
  name = G4_Bi
  specific = 4
FEATURE [App::DocumentObjectGroupPython] Po_element001  label="Po_element : 1"  # scripted group (container) (typed FeaturePython)
  n = 1
  ref = Po_element
FEATURE [App::DocumentObjectGroupPython] G4_Po  # scripted group (container) (typed FeaturePython)
  Dunit = g/cm3
  Dvalue = 9.32
  Group = -> [Po_element001]
  conduct = 2
  density = 1
  expand = 3
  formula = Po
  name = G4_Po
  specific = 4
FEATURE [App::DocumentObjectGroupPython] At_element001  label="At_element : 1"  # scripted group (container) (typed FeaturePython)
  n = 1
  ref = At_element
FEATURE [App::DocumentObjectGroupPython] G4_At  # scripted group (container) (typed FeaturePython)
  Dunit = g/cm3
  Dvalue = 9.32
  Group = -> [At_element001]
  conduct = 2
  density = 1
  expand = 3
  formula = At
  name = G4_At
  specific = 4
FEATURE [App::DocumentObjectGroupPython] Rn_element001  label="Rn_element : 1"  # scripted group (container) (typed FeaturePython)
  n = 1
  ref = Rn_element
FEATURE [App::DocumentObjectGroupPython] G4_Rn  # scripted group (container) (typed FeaturePython)
  Dunit = g/cm3
  Dvalue = 0.00900662
  Group = -> [Rn_element001]
  conduct = 2
  density = 1
  expand = 3
  formula = Rn
  name = G4_Rn
  specific = 4
FEATURE [App::DocumentObjectGroupPython] Fr_element001  label="Fr_element : 1"  # scripted group (container) (typed FeaturePython)
  n = 1
  ref = Fr_element
FEATURE [App::DocumentObjectGroupPython] G4_Fr  # scripted group (container) (typed FeaturePython)
  Dunit = g/cm3
  Dvalue = 1
  Group = -> [Fr_element001]
  conduct = 2
  density = 1
  expand = 3
  formula = Fr
  name = G4_Fr
  specific = 4
FEATURE [App::DocumentObjectGroupPython] Ra_element001  label="Ra_element : 1"  # scripted group (container) (typed FeaturePython)
  n = 1
  ref = Ra_element
FEATURE [App::DocumentObjectGroupPython] G4_Ra  # scripted group (container) (typed FeaturePython)
  Dunit = g/cm3
  Dvalue = 5
  Group = -> [Ra_element001]
  conduct = 2
  density = 1
  expand = 3
  formula = Ra
  name = G4_Ra
  specific = 4
FEATURE [App::DocumentObjectGroupPython] Ac_element001  label="Ac_element : 1"  # scripted group (container) (typed FeaturePython)
  n = 1
  ref = Ac_element
FEATURE [App::DocumentObjectGroupPython] G4_Ac  # scripted group (container) (typed FeaturePython)
  Dunit = g/cm3
  Dvalue = 10.07
  Group = -> [Ac_element001]
  conduct = 2
  density = 1
  expand = 3
  formula = Ac
  name = G4_Ac
  specific = 4
FEATURE [App::DocumentObjectGroupPython] Th_element001  label="Th_element : 1"  # scripted group (container) (typed FeaturePython)
  n = 1
  ref = Th_element
FEATURE [App::DocumentObjectGroupPython] G4_Th  # scripted group (container) (typed FeaturePython)
  Dunit = g/cm3
  Dvalue = 11.72
  Group = -> [Th_element001]
  conduct = 2
  density = 1
  expand = 3
  formula = Th
  name = G4_Th
  specific = 4
FEATURE [App::DocumentObjectGroupPython] Pa_element001  label="Pa_element : 1"  # scripted group (container) (typed FeaturePython)
  n = 1
  ref = Pa_element
FEATURE [App::DocumentObjectGroupPython] G4_Pa  # scripted group (container) (typed FeaturePython)
  Dunit = g/cm3
  Dvalue = 15.37
  Group = -> [Pa_element001]
  conduct = 2
  density = 1
  expand = 3
  formula = Pa
  name = G4_Pa
  specific = 4
FEATURE [App::DocumentObjectGroupPython] U_element004  label="U_element : 004"  # scripted group (container) (typed FeaturePython)
  n = 1
  ref = U_element
FEATURE [App::DocumentObjectGroupPython] G4_U  # scripted group (container) (typed FeaturePython)
  Dunit = g/cm3
  Dvalue = 18.95
  Group = -> [U_element004]
  conduct = 2
  density = 1
  expand = 3
  formula = U
  name = G4_U
  specific = 4
FEATURE [App::DocumentObjectGroupPython] Np_element001  label="Np_element : 1"  # scripted group (container) (typed FeaturePython)
  n = 1
  ref = Np_element
FEATURE [App::DocumentObjectGroupPython] G4_Np  # scripted group (container) (typed FeaturePython)
  Dunit = g/cm3
  Dvalue = 20.25
  Group = -> [Np_element001]
  conduct = 2
  density = 1
  expand = 3
  formula = Np
  name = G4_Np
  specific = 4
FEATURE [App::DocumentObjectGroupPython] Pu_element002  label="Pu_element : 002"  # scripted group (container) (typed FeaturePython)
  n = 1
  ref = Pu_element
FEATURE [App::DocumentObjectGroupPython] G4_Pu  # scripted group (container) (typed FeaturePython)
  Dunit = g/cm3
  Dvalue = 19.84
  Group = -> [Pu_element002]
  conduct = 2
  density = 1
  expand = 3
  formula = Pu
  name = G4_Pu
  specific = 4
FEATURE [App::DocumentObjectGroupPython] Am_element001  label="Am_element : 1"  # scripted group (container) (typed FeaturePython)
  n = 1
  ref = Am_element
FEATURE [App::DocumentObjectGroupPython] G4_Am  # scripted group (container) (typed FeaturePython)
  Dunit = g/cm3
  Dvalue = 13.67
  Group = -> [Am_element001]
  conduct = 2
  density = 1
  expand = 3
  formula = Am
  name = G4_Am
  specific = 4
FEATURE [App::DocumentObjectGroupPython] Cm_element001  label="Cm_element : 1"  # scripted group (container) (typed FeaturePython)
  n = 1
  ref = Cm_element
FEATURE [App::DocumentObjectGroupPython] G4_Cm  # scripted group (container) (typed FeaturePython)
  Dunit = g/cm3
  Dvalue = 13.51
  Group = -> [Cm_element001]
  conduct = 2
  density = 1
  expand = 3
  formula = Cm
  name = G4_Cm
  specific = 4
FEATURE [App::DocumentObjectGroupPython] Bk_element001  label="Bk_element : 1"  # scripted group (container) (typed FeaturePython)
  n = 1
  ref = Bk_element
FEATURE [App::DocumentObjectGroupPython] G4_Bk  # scripted group (container) (typed FeaturePython)
  Dunit = g/cm3
  Dvalue = 14
  Group = -> [Bk_element001]
  conduct = 2
  density = 1
  expand = 3
  formula = Bk
  name = G4_Bk
  specific = 4
FEATURE [App::DocumentObjectGroupPython] Cf_element001  label="Cf_element : 1"  # scripted group (container) (typed FeaturePython)
  n = 1
  ref = Cf_element
FEATURE [App::DocumentObjectGroupPython] G4_Cf  # scripted group (container) (typed FeaturePython)
  Dunit = g/cm3
  Dvalue = 10
  Group = -> [Cf_element001]
  conduct = 2
  density = 1
  expand = 3
  formula = Cf
  name = G4_Cf
  specific = 4
FEATURE [App::DocumentObjectGroupPython] Element  # scripted group (container) (typed FeaturePython)
  Group = -> [G4_H,G4_He,G4_Li,G4_Be,G4_B,G4_C,G4_N,G4_O,G4_F,G4_Ne,G4_Na,G4_Mg,G4_Al,G4_Si,G4_P,G4_S,G4_Cl,G4_Ar,G4_K,G4_Ca,G4_Sc,G4_Ti,G4_V,G4_Cr,G4_Mn,G4_Fe,G4_Co,G4_Ni,G4_Cu,G4_Zn,G4_Ga,G4_Ge,G4_As,G4_Se,G4_Br,G4_Kr,G4_Rb,G4_Sr,G4_Y,G4_Zr,G4_Nb,G4_Mo,G4_Tc,G4_Ru,G4_Rh,G4_Pd,G4_Ag,G4_Cd,G4_In,G4_Sn,G4_Sb,G4_Te,G4_I,G4_Xe,G4_Cs,G4_Ba,G4_La,G4_Ce,G4_Pr,G4_Nd,G4_Pm,G4_Sm,G4_Eu,G4_Gd,G4_Tb,G4_Dy,G4_Ho,G4_Er,+30 more]
FEATURE [App::DocumentObjectGroupPython] H_element114  label="H_element : 063"  # scripted group (container) (typed FeaturePython)
  n = 2
  ref = H_element
FEATURE [App::DocumentObjectGroupPython] G4_lH2  # scripted group (container) (typed FeaturePython)
  Dunit = g/cm3
  Dvalue = 0.0708
  Group = -> [H_element114]
  conduct = 2
  density = 1
  expand = 3
  formula = G4_lH2
  name = G4_lH2
  specific = 4
FEATURE [App::DocumentObjectGroupPython] N_element049  label="N_element : 022"  # scripted group (container) (typed FeaturePython)
  n = 2
  ref = N_element
FEATURE [App::DocumentObjectGroupPython] G4_lN2  # scripted group (container) (typed FeaturePython)
  Dunit = g/cm3
  Dvalue = 0.807
  Group = -> [N_element049]
  conduct = 2
  density = 1
  expand = 3
  formula = G4_lN2
  name = G4_lN2
  specific = 4
FEATURE [App::DocumentObjectGroupPython] O_element106  label="O_element : 060"  # scripted group (container) (typed FeaturePython)
  n = 2
  ref = O_element
FEATURE [App::DocumentObjectGroupPython] G4_lO2  # scripted group (container) (typed FeaturePython)
  Dunit = g/cm3
  Dvalue = 1.141
  Group = -> [O_element106]
  conduct = 2
  density = 1
  expand = 3
  formula = G4_lO2
  name = G4_lO2
  specific = 4
FEATURE [App::DocumentObjectGroupPython] Ar  label="Ar : 1"  # scripted group (container) (typed FeaturePython)
  n = 1
  ref = Ar
FEATURE [App::DocumentObjectGroupPython] G4_lAr  # scripted group (container) (typed FeaturePython)
  Dunit = g/cm3
  Dvalue = 1.396
  Group = -> [Ar]
  conduct = 2
  density = 1
  expand = 3
  formula = G4_lAr
  name = G4_lAr
  specific = 4
FEATURE [App::DocumentObjectGroupPython] Br  label="Br : 1"  # scripted group (container) (typed FeaturePython)
  n = 1
  ref = Br
FEATURE [App::DocumentObjectGroupPython] G4_lBr  # scripted group (container) (typed FeaturePython)
  Dunit = g/cm3
  Dvalue = 3.1028
  Group = -> [Br]
  conduct = 2
  density = 1
  expand = 3
  formula = G4_lBr
  name = G4_lBr
  specific = 4
FEATURE [App::DocumentObjectGroupPython] Kr  label="Kr : 1"  # scripted group (container) (typed FeaturePython)
  n = 1
  ref = Kr
FEATURE [App::DocumentObjectGroupPython] G4_lKr  # scripted group (container) (typed FeaturePython)
  Dunit = g/cm3
  Dvalue = 2.418
  Group = -> [Kr]
  conduct = 2
  density = 1
  expand = 3
  formula = G4_lKr
  name = G4_lKr
  specific = 4
FEATURE [App::DocumentObjectGroupPython] Xe  label="Xe : 1"  # scripted group (container) (typed FeaturePython)
  n = 1
  ref = Xe
FEATURE [App::DocumentObjectGroupPython] G4_lXe  # scripted group (container) (typed FeaturePython)
  Dunit = g/cm3
  Dvalue = 2.953
  Group = -> [Xe]
  conduct = 2
  density = 1
  expand = 3
  formula = G4_lXe
  name = G4_lXe
  specific = 4
FEATURE [App::DocumentObjectGroupPython] O_element107  label="O_element : 061"  # scripted group (container) (typed FeaturePython)
  n = 4
  ref = O_element
FEATURE [App::DocumentObjectGroupPython] Pb_element004  label="Pb_element : 002"  # scripted group (container) (typed FeaturePython)
  n = 1
  ref = Pb_element
FEATURE [App::DocumentObjectGroupPython] W_element005  label="W_element : 005"  # scripted group (container) (typed FeaturePython)
  n = 1
  ref = W_element
FEATURE [App::DocumentObjectGroupPython] G4_PbWO4  # scripted group (container) (typed FeaturePython)
  Dunit = g/cm3
  Dvalue = 8.28
  Group = -> [O_element107,Pb_element004,W_element005]
  conduct = 2
  density = 1
  expand = 3
  formula = G4_PbWO4
  name = G4_PbWO4
  specific = 4
FEATURE [App::DocumentObjectGroupPython] alactic  label="alactic : 1"  # scripted group (container) (typed FeaturePython)
  n = 1
  ref = alactic
FEATURE [App::DocumentObjectGroupPython] G4_Galactic  # scripted group (container) (typed FeaturePython)
  Dunit = g/cm3
  Dvalue = 0
  Group = -> [alactic]
  conduct = 2
  density = 1
  expand = 3
  formula = G4_Galactic
  name = G4_Galactic
  specific = 4
FEATURE [App::DocumentObjectGroupPython] RAPHITE_POROUS  label="RAPHITE_POROUS : 1"  # scripted group (container) (typed FeaturePython)
  n = 1
  ref = RAPHITE_POROUS
FEATURE [App::DocumentObjectGroupPython] G4_GRAPHITE_POROUS  # scripted group (container) (typed FeaturePython)
  Dunit = g/cm3
  Dvalue = 1.7
  Group = -> [RAPHITE_POROUS]
  conduct = 2
  density = 1
  expand = 3
  formula = G4_GRAPHITE_POROUS
  name = G4_GRAPHITE_POROUS
  specific = 4
FEATURE [App::DocumentObjectGroupPython] H_element115  label="H_element : 0.150"  # scripted group (container) (typed FeaturePython)
  n = 0.080538
FEATURE [App::DocumentObjectGroupPython] C_element125  label="C_element : 0.600"  # scripted group (container) (typed FeaturePython)
  n = 0.599848
FEATURE [App::DocumentObjectGroupPython] O_element108  label="O_element : 0.320"  # scripted group (container) (typed FeaturePython)
  n = 0.319614
FEATURE [App::DocumentObjectGroupPython] G4_LUCITE  # scripted group (container) (typed FeaturePython)
  Dunit = g/cm3
  Dvalue = 1.19
  Group = -> [H_element115,C_element125,O_element108]
  conduct = 2
  density = 1
  expand = 3
  formula = G4_LUCITE
  name = G4_LUCITE
  specific = 4
FEATURE [App::DocumentObjectGroupPython] Cu_element002  label="Cu_element : 62"  # scripted group (container) (typed FeaturePython)
  n = 62
  ref = Cu_element
FEATURE [App::DocumentObjectGroupPython] Zn_element002  label="Zn_element : 35"  # scripted group (container) (typed FeaturePython)
  n = 35
  ref = Zn_element
FEATURE [App::DocumentObjectGroupPython] Pb_element005  label="Pb_element : 3"  # scripted group (container) (typed FeaturePython)
  n = 3
  ref = Pb_element
FEATURE [App::DocumentObjectGroupPython] G4_BRASS  # scripted group (container) (typed FeaturePython)
  Dunit = g/cm3
  Dvalue = 8.52
  Group = -> [Cu_element002,Zn_element002,Pb_element005]
  conduct = 2
  density = 1
  expand = 3
  formula = G4_BRASS
  name = G4_BRASS
  specific = 4
FEATURE [App::DocumentObjectGroupPython] Cu_element003  label="Cu_element : 89"  # scripted group (container) (typed FeaturePython)
  n = 89
  ref = Cu_element
FEATURE [App::DocumentObjectGroupPython] Zn_element003  label="Zn_element : 9"  # scripted group (container) (typed FeaturePython)
  n = 9
  ref = Zn_element
FEATURE [App::DocumentObjectGroupPython] Pb_element006  label="Pb_element : 2"  # scripted group (container) (typed FeaturePython)
  n = 2
  ref = Pb_element
FEATURE [App::DocumentObjectGroupPython] G4_BRONZE  # scripted group (container) (typed FeaturePython)
  Dunit = g/cm3
  Dvalue = 8.82
  Group = -> [Cu_element003,Zn_element003,Pb_element006]
  conduct = 2
  density = 1
  expand = 3
  formula = G4_BRONZE
  name = G4_BRONZE
  specific = 4
FEATURE [App::DocumentObjectGroupPython] Fe_element008  label="Fe_element : 74"  # scripted group (container) (typed FeaturePython)
  n = 74
  ref = Fe_element
FEATURE [App::DocumentObjectGroupPython] Cr_element002  label="Cr_element : 18"  # scripted group (container) (typed FeaturePython)
  n = 18
  ref = Cr_element
FEATURE [App::DocumentObjectGroupPython] Ni_element002  label="Ni_element : 8"  # scripted group (container) (typed FeaturePython)
  n = 8
  ref = Ni_element
FEATURE [App::DocumentObjectGroupPython] G4_STAINLESS_STEEL  label="G4_STAINLESS-STEEL"  # scripted group (container) (typed FeaturePython)
  Dunit = g/cm3
  Dvalue = 8
  Group = -> [Fe_element008,Cr_element002,Ni_element002]
  conduct = 2
  density = 1
  expand = 3
  formula = G4_STAINLESS-STEEL
  name = G4_STAINLESS-STEEL
  specific = 4
FEATURE [App::DocumentObjectGroupPython] H_element116  label="H_element : 064"  # scripted group (container) (typed FeaturePython)
  n = 18
  ref = H_element
FEATURE [App::DocumentObjectGroupPython] C_element126  label="C_element : 071"  # scripted group (container) (typed FeaturePython)
  n = 12
  ref = C_element
FEATURE [App::DocumentObjectGroupPython] O_element109  label="O_element : 062"  # scripted group (container) (typed FeaturePython)
  n = 7
  ref = O_element
FEATURE [App::DocumentObjectGroupPython] G4_CR39  # scripted group (container) (typed FeaturePython)
  Dunit = g/cm3
  Dvalue = 1.32
  Group = -> [H_element116,C_element126,O_element109]
  conduct = 2
  density = 1
  expand = 3
  formula = G4_CR39
  name = G4_CR39
  specific = 4
FEATURE [App::DocumentObjectGroupPython] H_element117  label="H_element : 38"  # scripted group (container) (typed FeaturePython)
  n = 38
  ref = H_element
FEATURE [App::DocumentObjectGroupPython] C_element127  label="C_element : 072"  # scripted group (container) (typed FeaturePython)
  n = 18
  ref = C_element
FEATURE [App::DocumentObjectGroupPython] O_element110  label="O_element : 063"  # scripted group (container) (typed FeaturePython)
  n = 1
  ref = O_element
FEATURE [App::DocumentObjectGroupPython] G4_OCTADECANOL  # scripted group (container) (typed FeaturePython)
  Dunit = g/cm3
  Dvalue = 0.812
  Group = -> [H_element117,C_element127,O_element110]
  conduct = 2
  density = 1
  expand = 3
  formula = G4_OCTADECANOL
  name = G4_OCTADECANOL
  specific = 4
FEATURE [App::DocumentObjectGroupPython] HEP  # scripted group (container) (typed FeaturePython)
  Group = -> [G4_lH2,G4_lN2,G4_lO2,G4_lAr,G4_lBr,G4_lKr,G4_lXe,G4_PbWO4,G4_Galactic,G4_GRAPHITE_POROUS,G4_LUCITE,G4_BRASS,G4_BRONZE,G4_STAINLESS_STEEL,G4_CR39,G4_OCTADECANOL]
FEATURE [App::DocumentObjectGroupPython] C_element128  label="C_element : 073"  # scripted group (container) (typed FeaturePython)
  n = 14
  ref = C_element
FEATURE [App::DocumentObjectGroupPython] H_element118  label="H_element : 065"  # scripted group (container) (typed FeaturePython)
  n = 10
  ref = H_element
FEATURE [App::DocumentObjectGroupPython] O_element111  label="O_element : 064"  # scripted group (container) (typed FeaturePython)
  n = 2
  ref = O_element
FEATURE [App::DocumentObjectGroupPython] N_element050  label="N_element : 023"  # scripted group (container) (typed FeaturePython)
  n = 2
  ref = N_element
FEATURE [App::DocumentObjectGroupPython] G4_KEVLAR  # scripted group (container) (typed FeaturePython)
  Dunit = g/cm3
  Dvalue = 1.44
  Group = -> [C_element128,H_element118,O_element111,N_element050]
  conduct = 2
  density = 1
  expand = 3
  formula = G4_KEVLAR
  name = G4_KEVLAR
  specific = 4
FEATURE [App::DocumentObjectGroupPython] C_element129  label="C_element : 074"  # scripted group (container) (typed FeaturePython)
  n = 10
  ref = C_element
FEATURE [App::DocumentObjectGroupPython] H_element119  label="H_element : 066"  # scripted group (container) (typed FeaturePython)
  n = 8
  ref = H_element
FEATURE [App::DocumentObjectGroupPython] O_element112  label="O_element : 065"  # scripted group (container) (typed FeaturePython)
  n = 4
  ref = O_element
FEATURE [App::DocumentObjectGroupPython] G4_DACRON  # scripted group (container) (typed FeaturePython)
  Dunit = g/cm3
  Dvalue = 1.4
  Group = -> [C_element129,H_element119,O_element112]
  conduct = 2
  density = 1
  expand = 3
  formula = G4_DACRON
  name = G4_DACRON
  specific = 4
FEATURE [App::DocumentObjectGroupPython] C_element130  label="C_element : 075"  # scripted group (container) (typed FeaturePython)
  n = 4
  ref = C_element
FEATURE [App::DocumentObjectGroupPython] H_element120  label="H_element : 067"  # scripted group (container) (typed FeaturePython)
  n = 5
  ref = H_element
FEATURE [App::DocumentObjectGroupPython] Cl_element030  label="Cl_element : 016"  # scripted group (container) (typed FeaturePython)
  n = 1
  ref = Cl_element
FEATURE [App::DocumentObjectGroupPython] G4_NEOPRENE  # scripted group (container) (typed FeaturePython)
  Dunit = g/cm3
  Dvalue = 1.23
  Group = -> [C_element130,H_element120,Cl_element030]
  conduct = 2
  density = 1
  expand = 3
  formula = G4_NEOPRENE
  name = G4_NEOPRENE
  specific = 4
FEATURE [App::DocumentObjectGroupPython] Space  # scripted group (container) (typed FeaturePython)
  Group = -> [G4_KEVLAR,G4_DACRON,G4_NEOPRENE]
FEATURE [App::DocumentObjectGroupPython] H_element121  label="H_element : 068"  # scripted group (container) (typed FeaturePython)
  n = 5
  ref = H_element
FEATURE [App::DocumentObjectGroupPython] C_element131  label="C_element : 076"  # scripted group (container) (typed FeaturePython)
  n = 4
  ref = C_element
FEATURE [App::DocumentObjectGroupPython] N_element051  label="N_element : 3"  # scripted group (container) (typed FeaturePython)
  n = 3
  ref = N_element
FEATURE [App::DocumentObjectGroupPython] O_element113  label="O_element : 066"  # scripted group (container) (typed FeaturePython)
  n = 1
  ref = O_element
FEATURE [App::DocumentObjectGroupPython] G4_CYTOSINE  # scripted group (container) (typed FeaturePython)
  Dunit = g/cm3
  Dvalue = 1.55
  Group = -> [H_element121,C_element131,N_element051,O_element113]
  conduct = 2
  density = 1
  expand = 3
  formula = G4_CYTOSINE
  name = G4_CYTOSINE
  specific = 4
FEATURE [App::DocumentObjectGroupPython] H_element122  label="H_element : 069"  # scripted group (container) (typed FeaturePython)
  n = 6
  ref = H_element
FEATURE [App::DocumentObjectGroupPython] C_element132  label="C_element : 077"  # scripted group (container) (typed FeaturePython)
  n = 5
  ref = C_element
FEATURE [App::DocumentObjectGroupPython] N_element052  label="N_element : 024"  # scripted group (container) (typed FeaturePython)
  n = 2
  ref = N_element
FEATURE [App::DocumentObjectGroupPython] O_element114  label="O_element : 067"  # scripted group (container) (typed FeaturePython)
  n = 2
  ref = O_element
FEATURE [App::DocumentObjectGroupPython] G4_THYMINE  # scripted group (container) (typed FeaturePython)
  Dunit = g/cm3
  Dvalue = 1.23
  Group = -> [H_element122,C_element132,N_element052,O_element114]
  conduct = 2
  density = 1
  expand = 3
  formula = G4_THYMINE
  name = G4_THYMINE
  specific = 4
FEATURE [App::DocumentObjectGroupPython] H_element123  label="H_element : 070"  # scripted group (container) (typed FeaturePython)
  n = 4
  ref = H_element
FEATURE [App::DocumentObjectGroupPython] C_element133  label="C_element : 078"  # scripted group (container) (typed FeaturePython)
  n = 4
  ref = C_element
FEATURE [App::DocumentObjectGroupPython] N_element053  label="N_element : 025"  # scripted group (container) (typed FeaturePython)
  n = 2
  ref = N_element
FEATURE [App::DocumentObjectGroupPython] O_element115  label="O_element : 068"  # scripted group (container) (typed FeaturePython)
  n = 2
  ref = O_element
FEATURE [App::DocumentObjectGroupPython] G4_URACIL  # scripted group (container) (typed FeaturePython)
  Dunit = g/cm3
  Dvalue = 1.32
  Group = -> [H_element123,C_element133,N_element053,O_element115]
  conduct = 2
  density = 1
  expand = 3
  formula = G4_URACIL
  name = G4_URACIL
  specific = 4
FEATURE [App::DocumentObjectGroupPython] H_element124  label="H_element : 071"  # scripted group (container) (typed FeaturePython)
  n = 4
  ref = H_element
FEATURE [App::DocumentObjectGroupPython] C_element134  label="C_element : 079"  # scripted group (container) (typed FeaturePython)
  n = 5
  ref = C_element
FEATURE [App::DocumentObjectGroupPython] N_element054  label="N_element : 026"  # scripted group (container) (typed FeaturePython)
  n = 5
  ref = N_element
FEATURE [App::DocumentObjectGroupPython] G4_DNA_ADENINE  # scripted group (container) (typed FeaturePython)
  Dunit = g/cm3
  Dvalue = 1
  Group = -> [H_element124,C_element134,N_element054]
  conduct = 2
  density = 1
  expand = 3
  formula = G4_DNA_ADENINE
  name = G4_DNA_ADENINE
  specific = 4
FEATURE [App::DocumentObjectGroupPython] H_element125  label="H_element : 072"  # scripted group (container) (typed FeaturePython)
  n = 4
  ref = H_element
FEATURE [App::DocumentObjectGroupPython] C_element135  label="C_element : 080"  # scripted group (container) (typed FeaturePython)
  n = 5
  ref = C_element
FEATURE [App::DocumentObjectGroupPython] N_element055  label="N_element : 027"  # scripted group (container) (typed FeaturePython)
  n = 5
  ref = N_element
FEATURE [App::DocumentObjectGroupPython] O_element116  label="O_element : 069"  # scripted group (container) (typed FeaturePython)
  n = 1
  ref = O_element
FEATURE [App::DocumentObjectGroupPython] G4_DNA_GUANINE  # scripted group (container) (typed FeaturePython)
  Dunit = g/cm3
  Dvalue = 1
  Group = -> [H_element125,C_element135,N_element055,O_element116]
  conduct = 2
  density = 1
  expand = 3
  formula = G4_DNA_GUANINE
  name = G4_DNA_GUANINE
  specific = 4
FEATURE [App::DocumentObjectGroupPython] H_element126  label="H_element : 073"  # scripted group (container) (typed FeaturePython)
  n = 4
  ref = H_element
FEATURE [App::DocumentObjectGroupPython] C_element136  label="C_element : 081"  # scripted group (container) (typed FeaturePython)
  n = 4
  ref = C_element
FEATURE [App::DocumentObjectGroupPython] N_element056  label="N_element : 028"  # scripted group (container) (typed FeaturePython)
  n = 3
  ref = N_element
FEATURE [App::DocumentObjectGroupPython] O_element117  label="O_element : 070"  # scripted group (container) (typed FeaturePython)
  n = 1
  ref = O_element
FEATURE [App::DocumentObjectGroupPython] G4_DNA_CYTOSINE  # scripted group (container) (typed FeaturePython)
  Dunit = g/cm3
  Dvalue = 1
  Group = -> [H_element126,C_element136,N_element056,O_element117]
  conduct = 2
  density = 1
  expand = 3
  formula = G4_DNA_CYTOSINE
  name = G4_DNA_CYTOSINE
  specific = 4
FEATURE [App::DocumentObjectGroupPython] H_element127  label="H_element : 074"  # scripted group (container) (typed FeaturePython)
  n = 5
  ref = H_element
FEATURE [App::DocumentObjectGroupPython] C_element137  label="C_element : 082"  # scripted group (container) (typed FeaturePython)
  n = 5
  ref = C_element
FEATURE [App::DocumentObjectGroupPython] N_element057  label="N_element : 029"  # scripted group (container) (typed FeaturePython)
  n = 2
  ref = N_element
FEATURE [App::DocumentObjectGroupPython] O_element118  label="O_element : 071"  # scripted group (container) (typed FeaturePython)
  n = 2
  ref = O_element
FEATURE [App::DocumentObjectGroupPython] G4_DNA_THYMINE  # scripted group (container) (typed FeaturePython)
  Dunit = g/cm3
  Dvalue = 1
  Group = -> [H_element127,C_element137,N_element057,O_element118]
  conduct = 2
  density = 1
  expand = 3
  formula = G4_DNA_THYMINE
  name = G4_DNA_THYMINE
  specific = 4
FEATURE [App::DocumentObjectGroupPython] H_element128  label="H_element : 075"  # scripted group (container) (typed FeaturePython)
  n = 3
  ref = H_element
FEATURE [App::DocumentObjectGroupPython] C_element138  label="C_element : 083"  # scripted group (container) (typed FeaturePython)
  n = 4
  ref = C_element
FEATURE [App::DocumentObjectGroupPython] N_element058  label="N_element : 030"  # scripted group (container) (typed FeaturePython)
  n = 2
  ref = N_element
FEATURE [App::DocumentObjectGroupPython] O_element119  label="O_element : 072"  # scripted group (container) (typed FeaturePython)
  n = 2
  ref = O_element
FEATURE [App::DocumentObjectGroupPython] G4_DNA_URACIL  # scripted group (container) (typed FeaturePython)
  Dunit = g/cm3
  Dvalue = 1
  Group = -> [H_element128,C_element138,N_element058,O_element119]
  conduct = 2
  density = 1
  expand = 3
  formula = G4_DNA_URACIL
  name = G4_DNA_URACIL
  specific = 4
FEATURE [App::DocumentObjectGroupPython] H_element129  label="H_element : 076"  # scripted group (container) (typed FeaturePython)
  n = 10
  ref = H_element
FEATURE [App::DocumentObjectGroupPython] C_element139  label="C_element : 084"  # scripted group (container) (typed FeaturePython)
  n = 10
  ref = C_element
FEATURE [App::DocumentObjectGroupPython] N_element059  label="N_element : 031"  # scripted group (container) (typed FeaturePython)
  n = 5
  ref = N_element
FEATURE [App::DocumentObjectGroupPython] O_element120  label="O_element : 073"  # scripted group (container) (typed FeaturePython)
  n = 4
  ref = O_element
FEATURE [App::DocumentObjectGroupPython] G4_DNA_ADENOSINE  # scripted group (container) (typed FeaturePython)
  Dunit = g/cm3
  Dvalue = 1
  Group = -> [H_element129,C_element139,N_element059,O_element120]
  conduct = 2
  density = 1
  expand = 3
  formula = G4_DNA_ADENOSINE
  name = G4_DNA_ADENOSINE
  specific = 4
FEATURE [App::DocumentObjectGroupPython] H_element130  label="H_element : 077"  # scripted group (container) (typed FeaturePython)
  n = 10
  ref = H_element
FEATURE [App::DocumentObjectGroupPython] C_element140  label="C_element : 085"  # scripted group (container) (typed FeaturePython)
  n = 10
  ref = C_element
FEATURE [App::DocumentObjectGroupPython] N_element060  label="N_element : 032"  # scripted group (container) (typed FeaturePython)
  n = 5
  ref = N_element
FEATURE [App::DocumentObjectGroupPython] O_element121  label="O_element : 074"  # scripted group (container) (typed FeaturePython)
  n = 5
  ref = O_element
FEATURE [App::DocumentObjectGroupPython] G4_DNA_GUANOSINE  # scripted group (container) (typed FeaturePython)
  Dunit = g/cm3
  Dvalue = 1
  Group = -> [H_element130,C_element140,N_element060,O_element121]
  conduct = 2
  density = 1
  expand = 3
  formula = G4_DNA_GUANOSINE
  name = G4_DNA_GUANOSINE
  specific = 4
FEATURE [App::DocumentObjectGroupPython] H_element131  label="H_element : 078"  # scripted group (container) (typed FeaturePython)
  n = 10
  ref = H_element
FEATURE [App::DocumentObjectGroupPython] C_element141  label="C_element : 086"  # scripted group (container) (typed FeaturePython)
  n = 9
  ref = C_element
FEATURE [App::DocumentObjectGroupPython] N_element061  label="N_element : 033"  # scripted group (container) (typed FeaturePython)
  n = 3
  ref = N_element
FEATURE [App::DocumentObjectGroupPython] O_element122  label="O_element : 075"  # scripted group (container) (typed FeaturePython)
  n = 5
  ref = O_element
FEATURE [App::DocumentObjectGroupPython] G4_DNA_CYTIDINE  # scripted group (container) (typed FeaturePython)
  Dunit = g/cm3
  Dvalue = 1
  Group = -> [H_element131,C_element141,N_element061,O_element122]
  conduct = 2
  density = 1
  expand = 3
  formula = G4_DNA_CYTIDINE
  name = G4_DNA_CYTIDINE
  specific = 4
FEATURE [App::DocumentObjectGroupPython] H_element132  label="H_element : 079"  # scripted group (container) (typed FeaturePython)
  n = 9
  ref = H_element
FEATURE [App::DocumentObjectGroupPython] C_element142  label="C_element : 087"  # scripted group (container) (typed FeaturePython)
  n = 9
  ref = C_element
FEATURE [App::DocumentObjectGroupPython] N_element062  label="N_element : 034"  # scripted group (container) (typed FeaturePython)
  n = 2
  ref = N_element
FEATURE [App::DocumentObjectGroupPython] O_element123  label="O_element : 076"  # scripted group (container) (typed FeaturePython)
  n = 6
  ref = O_element
FEATURE [App::DocumentObjectGroupPython] G4_DNA_URIDINE  # scripted group (container) (typed FeaturePython)
  Dunit = g/cm3
  Dvalue = 1
  Group = -> [H_element132,C_element142,N_element062,O_element123]
  conduct = 2
  density = 1
  expand = 3
  formula = G4_DNA_URIDINE
  name = G4_DNA_URIDINE
  specific = 4
FEATURE [App::DocumentObjectGroupPython] H_element133  label="H_element : 080"  # scripted group (container) (typed FeaturePython)
  n = 11
  ref = H_element
FEATURE [App::DocumentObjectGroupPython] C_element143  label="C_element : 088"  # scripted group (container) (typed FeaturePython)
  n = 10
  ref = C_element
FEATURE [App::DocumentObjectGroupPython] N_element063  label="N_element : 035"  # scripted group (container) (typed FeaturePython)
  n = 2
  ref = N_element
FEATURE [App::DocumentObjectGroupPython] O_element124  label="O_element : 077"  # scripted group (container) (typed FeaturePython)
  n = 6
  ref = O_element
FEATURE [App::DocumentObjectGroupPython] G4_DNA_METHYLURIDINE  # scripted group (container) (typed FeaturePython)
  Dunit = g/cm3
  Dvalue = 1
  Group = -> [H_element133,C_element143,N_element063,O_element124]
  conduct = 2
  density = 1
  expand = 3
  formula = G4_DNA_METHYLURIDINE
  name = G4_DNA_METHYLURIDINE
  specific = 4
FEATURE [App::DocumentObjectGroupPython] P_element014  label="P_element : 003"  # scripted group (container) (typed FeaturePython)
  n = 1
  ref = P_element
FEATURE [App::DocumentObjectGroupPython] O_element125  label="O_element : 078"  # scripted group (container) (typed FeaturePython)
  n = 3
  ref = O_element
FEATURE [App::DocumentObjectGroupPython] G4_DNA_MONOPHOSPHATE  # scripted group (container) (typed FeaturePython)
  Dunit = g/cm3
  Dvalue = 1
  Group = -> [P_element014,O_element125]
  conduct = 2
  density = 1
  expand = 3
  formula = G4_DNA_MONOPHOSPHATE
  name = G4_DNA_MONOPHOSPHATE
  specific = 4
FEATURE [App::DocumentObjectGroupPython] H_element134  label="H_element : 081"  # scripted group (container) (typed FeaturePython)
  n = 10
  ref = H_element
FEATURE [App::DocumentObjectGroupPython] C_element144  label="C_element : 089"  # scripted group (container) (typed FeaturePython)
  n = 10
  ref = C_element
FEATURE [App::DocumentObjectGroupPython] N_element064  label="N_element : 036"  # scripted group (container) (typed FeaturePython)
  n = 5
  ref = N_element
FEATURE [App::DocumentObjectGroupPython] O_element126  label="O_element : 079"  # scripted group (container) (typed FeaturePython)
  n = 7
  ref = O_element
FEATURE [App::DocumentObjectGroupPython] P_element015  label="P_element : 004"  # scripted group (container) (typed FeaturePython)
  n = 1
  ref = P_element
FEATURE [App::DocumentObjectGroupPython] G4_DNA_A  # scripted group (container) (typed FeaturePython)
  Dunit = g/cm3
  Dvalue = 1
  Group = -> [H_element134,C_element144,N_element064,O_element126,P_element015]
  conduct = 2
  density = 1
  expand = 3
  formula = G4_DNA_A
  name = G4_DNA_A
  specific = 4
FEATURE [App::DocumentObjectGroupPython] H_element135  label="H_element : 082"  # scripted group (container) (typed FeaturePython)
  n = 10
  ref = H_element
FEATURE [App::DocumentObjectGroupPython] C_element145  label="C_element : 090"  # scripted group (container) (typed FeaturePython)
  n = 10
  ref = C_element
FEATURE [App::DocumentObjectGroupPython] N_element065  label="N_element : 037"  # scripted group (container) (typed FeaturePython)
  n = 5
  ref = N_element
FEATURE [App::DocumentObjectGroupPython] O_element127  label="O_element : 8"  # scripted group (container) (typed FeaturePython)
  n = 8
  ref = O_element
FEATURE [App::DocumentObjectGroupPython] P_element016  label="P_element : 005"  # scripted group (container) (typed FeaturePython)
  n = 1
  ref = P_element
FEATURE [App::DocumentObjectGroupPython] G4_DNA_G  # scripted group (container) (typed FeaturePython)
  Dunit = g/cm3
  Dvalue = 1
  Group = -> [H_element135,C_element145,N_element065,O_element127,P_element016]
  conduct = 2
  density = 1
  expand = 3
  formula = G4_DNA_G
  name = G4_DNA_G
  specific = 4
FEATURE [App::DocumentObjectGroupPython] H_element136  label="H_element : 083"  # scripted group (container) (typed FeaturePython)
  n = 10
  ref = H_element
FEATURE [App::DocumentObjectGroupPython] C_element146  label="C_element : 091"  # scripted group (container) (typed FeaturePython)
  n = 9
  ref = C_element
FEATURE [App::DocumentObjectGroupPython] N_element066  label="N_element : 038"  # scripted group (container) (typed FeaturePython)
  n = 3
  ref = N_element
FEATURE [App::DocumentObjectGroupPython] O_element128  label="O_element : 080"  # scripted group (container) (typed FeaturePython)
  n = 8
  ref = O_element
FEATURE [App::DocumentObjectGroupPython] P_element017  label="P_element : 006"  # scripted group (container) (typed FeaturePython)
  n = 1
  ref = P_element
FEATURE [App::DocumentObjectGroupPython] G4_DNA_C  # scripted group (container) (typed FeaturePython)
  Dunit = g/cm3
  Dvalue = 1
  Group = -> [H_element136,C_element146,N_element066,O_element128,P_element017]
  conduct = 2
  density = 1
  expand = 3
  formula = G4_DNA_C
  name = G4_DNA_C
  specific = 4
FEATURE [App::DocumentObjectGroupPython] H_element137  label="H_element : 084"  # scripted group (container) (typed FeaturePython)
  n = 9
  ref = H_element
FEATURE [App::DocumentObjectGroupPython] C_element147  label="C_element : 092"  # scripted group (container) (typed FeaturePython)
  n = 9
  ref = C_element
FEATURE [App::DocumentObjectGroupPython] N_element067  label="N_element : 039"  # scripted group (container) (typed FeaturePython)
  n = 2
  ref = N_element
FEATURE [App::DocumentObjectGroupPython] O_element129  label="O_element : 9"  # scripted group (container) (typed FeaturePython)
  n = 9
  ref = O_element
FEATURE [App::DocumentObjectGroupPython] P_element018  label="P_element : 007"  # scripted group (container) (typed FeaturePython)
  n = 1
  ref = P_element
FEATURE [App::DocumentObjectGroupPython] G4_DNA_U  # scripted group (container) (typed FeaturePython)
  Dunit = g/cm3
  Dvalue = 1
  Group = -> [H_element137,C_element147,N_element067,O_element129,P_element018]
  conduct = 2
  density = 1
  expand = 3
  formula = G4_DNA_U
  name = G4_DNA_U
  specific = 4
FEATURE [App::DocumentObjectGroupPython] H_element138  label="H_element : 085"  # scripted group (container) (typed FeaturePython)
  n = 11
  ref = H_element
FEATURE [App::DocumentObjectGroupPython] C_element148  label="C_element : 093"  # scripted group (container) (typed FeaturePython)
  n = 10
  ref = C_element
FEATURE [App::DocumentObjectGroupPython] N_element068  label="N_element : 040"  # scripted group (container) (typed FeaturePython)
  n = 2
  ref = N_element
FEATURE [App::DocumentObjectGroupPython] O_element130  label="O_element : 081"  # scripted group (container) (typed FeaturePython)
  n = 9
  ref = O_element
FEATURE [App::DocumentObjectGroupPython] P_element019  label="P_element : 008"  # scripted group (container) (typed FeaturePython)
  n = 1
  ref = P_element
FEATURE [App::DocumentObjectGroupPython] G4_DNA_MU  # scripted group (container) (typed FeaturePython)
  Dunit = g/cm3
  Dvalue = 1
  Group = -> [H_element138,C_element148,N_element068,O_element130,P_element019]
  conduct = 2
  density = 1
  expand = 3
  formula = G4_DNA_MU
  name = G4_DNA_MU
  specific = 4
FEATURE [App::DocumentObjectGroupPython] BioChemical  # scripted group (container) (typed FeaturePython)
  Group = -> [G4_CYTOSINE,G4_THYMINE,G4_URACIL,G4_DNA_ADENINE,G4_DNA_GUANINE,G4_DNA_CYTOSINE,G4_DNA_THYMINE,G4_DNA_URACIL,G4_DNA_ADENOSINE,G4_DNA_GUANOSINE,G4_DNA_CYTIDINE,G4_DNA_URIDINE,G4_DNA_METHYLURIDINE,G4_DNA_MONOPHOSPHATE,G4_DNA_A,G4_DNA_G,G4_DNA_C,G4_DNA_U,G4_DNA_MU]
FEATURE [App::DocumentObjectGroupPython] G4Materials  # scripted group (container) (typed FeaturePython)
  Group = -> [NIST,Element,HEP,Space,BioChemical]
  version = 1
FEATURE [App::DocumentObjectGroupPython] Geant4  # scripted group (container) (typed FeaturePython)
  Group = -> [G4Isotopes,G4Elements,G4Materials]
FEATURE [App::DocumentObjectGroupPython] Materials  # scripted group (container) (typed FeaturePython)
  Group = -> [Geant4]
FEATURE [Part::FeaturePython] GDMLBox_WorldBox  # WARN: FeaturePython — macro-defined, semantics opaque (R4)
  lunit = 2
  material = 5
  x = 200
  y = 200
  z = 200
FEATURE [Part::FeaturePython] GDMLSphere_Sphere  # WARN: FeaturePython — macro-defined, semantics opaque (R4)
  aunit = 0
  deltaphi = 2.02
  deltatheta = 2.02
  lunit = 2
  material = 18
  rmax = 20
  rmin = 10
  startphi = 0
  starttheta = 0
FEATURE [App::Part] LV_Sphere
  Group = -> [GDMLSphere_Sphere]
  Origin = -> Origin002
  Placement = pos=(30,0,0) rot=(0,0,1;0rad)
FEATURE [Part::FeaturePython] GDMLTorus_Torus  # WARN: FeaturePython — macro-defined, semantics opaque (R4)
  aunit = deg
  deltaphi = 360
  lunit = 2
  material = 5
  rmax = 5
  rmin = 0
  rtor = 10
  startphi = 10
FEATURE [App::Part] LV_Torus
  Group = -> [GDMLTorus_Torus]
  Origin = -> Origin003
FEATURE [App::Part] Part
  Group = -> [LV_Sphere,LV_Torus]
  Origin = -> Origin001
FEATURE [Part::FeaturePython] Array  # Draft array (typed FeaturePython)
  Angle = 360
  ArrayType = 0
  Axis = (0,0,1)
  Base = -> Part
  Center = (0,0,0)
  Count = 4
  Fuse = false
  IntervalAxis = (0,0,0)
  IntervalX = (80,0,0)
  IntervalY = (0,80,0)
  IntervalZ = (0,0,100)
  NumberCircles = 3
  NumberPolar = 5
  NumberX = 2
  NumberY = 2
  NumberZ = 1
  Placement = pos=(-49,-28,0) rot=(0,0,1;0rad)
  RadialDistance = 50
  Symmetry = 1
  TangentialDistance = 25
  material = 261
FEATURE [App::Part] Part001
  Group = -> [Part,Array]
  Origin = -> Origin004
FEATURE [App::Part] worldVOL
  Group = -> [GDMLBox_WorldBox,Part001]
  Origin = -> Origin
